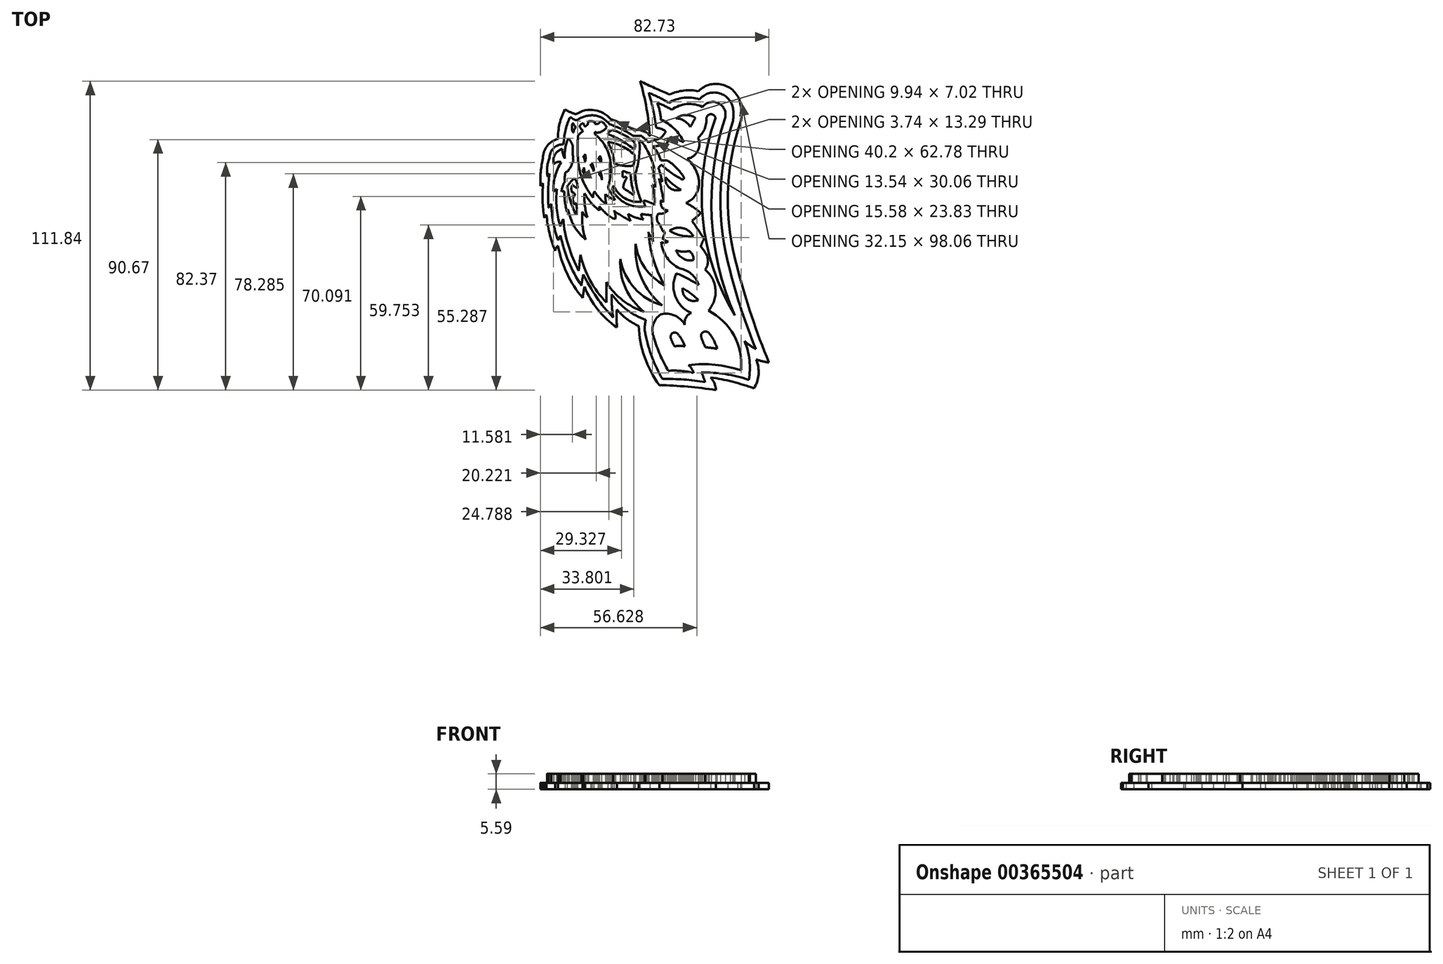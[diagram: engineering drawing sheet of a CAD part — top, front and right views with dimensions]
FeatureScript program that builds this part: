
annotation { "Feature Type Name" : "Feature", "Feature Type Description" : "" }
export const myFeature = defineFeature(function(context is Context, id is Id, definition is map)
    precondition{}
    {
        {
            var Q0;
            Q0=qCreatedBy(makeId("Top.planeOp"),FACE);
            var sketch = newSketch(context, id + "F0", { "sketchPlane" : qUnion([Q0])});
            skLineSegment(sketch, "E0", {"start": v(-9.68, 4.6) * mm, "end": v(-12.98, 4.6) * mm});
            skLineSegment(sketch, "E1", {"start": v(-7.81, 9.13) * mm, "end": v(-5.14, 8.87) * mm});
            skLineSegment(sketch, "E2", {"start": v(-0.46, 12.2) * mm, "end": v(0.77, 11.72) * mm});
            skLineSegment(sketch, "E3", {"start": v(5.28, 13.32) * mm, "end": v(5.62, 12.76) * mm});
            skArc(sketch, "E4", {"start": v(10.1, 12.03) * mm, "mid": v(7.78, 13.04) * mm, "end": v(5.28, 13.32) * mm});
            skArc(sketch, "E5", {"start": v(5.62, 12.76) * mm, "mid": v(2.55, 12.78) * mm, "end": v(-0.46, 12.2) * mm});
            skArc(sketch, "E6", {"start": v(0.77, 11.72) * mm, "mid": v(-3.65, 10.85) * mm, "end": v(-7.81, 9.13) * mm});
            skArc(sketch, "E7", {"start": v(-5.14, 8.87) * mm, "mid": v(-9.36, 7.3) * mm, "end": v(-12.98, 4.6) * mm});
            skArc(sketch, "E8", {"start": v(-9.68, 4.6) * mm, "mid": v(-12.64, 1.92) * mm, "end": v(-14.53, -1.6) * mm});
            skArc(sketch, "E9", {"start": v(-5.85, 2.3) * mm, "mid": v(-10.68, 1.43) * mm, "end": v(-14.53, -1.6) * mm});
            skArc(sketch, "E10", {"start": v(-5.85, 2.3) * mm, "mid": v(-10.66, -0.03) * mm, "end": v(-13.45, -4.58) * mm});
            skArc(sketch, "E11", {"start": v(-3.37, -0.22) * mm, "mid": v(-8.94, -1.17) * mm, "end": v(-13.45, -4.58) * mm});
            skArc(sketch, "E12", {"start": v(-3.37, -0.22) * mm, "mid": v(-7.34, -1.75) * mm, "end": v(-10.14, -4.94) * mm});
            skArc(sketch, "E13", {"start": v(-1.42, -2.32) * mm, "mid": v(-5.93, -3.13) * mm, "end": v(-10.14, -4.94) * mm});
            skArc(sketch, "E14", {"start": v(-1.42, -2.32) * mm, "mid": v(-2.2, -2.67) * mm, "end": v(-2.98, -3.05) * mm});
            skArc(sketch, "E15", {"start": v(-2.98, -3.05) * mm, "mid": v(-0.82, -2.97) * mm, "end": v(1.35, -2.86) * mm});
            skArc(sketch, "E16", {"start": v(1.55, -1.16) * mm, "mid": v(1.44, -2) * mm, "end": v(1.35, -2.86) * mm});
            skArc(sketch, "E17", {"start": v(1.55, -1.16) * mm, "mid": v(1.07, -1.21) * mm, "end": v(0.68, -1.5) * mm});
            skArc(sketch, "E18", {"start": v(1.55, 1.01) * mm, "mid": v(0.98, -0.2) * mm, "end": v(0.68, -1.5) * mm});
            skArc(sketch, "E19", {"start": v(1.55, 1.01) * mm, "mid": v(0.97, 0.86) * mm, "end": v(0.44, 0.6) * mm});
            skArc(sketch, "E20", {"start": v(2.1, 3.35) * mm, "mid": v(1.2, 2.02) * mm, "end": v(0.44, 0.6) * mm});
            skArc(sketch, "E21", {"start": v(0.68, 3.16) * mm, "mid": v(1.4, 3.13) * mm, "end": v(2.1, 3.35) * mm});
            skArc(sketch, "E22", {"start": v(2.8, 5.75) * mm, "mid": v(1.6, 4.58) * mm, "end": v(0.68, 3.16) * mm});
            skArc(sketch, "E23", {"start": v(2.8, 5.75) * mm, "mid": v(2.45, 5.77) * mm, "end": v(2.1, 5.75) * mm});
            skArc(sketch, "E24", {"start": v(4.98, 8.2) * mm, "mid": v(3.41, 7.12) * mm, "end": v(2.1, 5.75) * mm});
            skArc(sketch, "E25", {"start": v(4.98, 8.2) * mm, "mid": v(3, 8.16) * mm, "end": v(1.05, 7.73) * mm});
            skArc(sketch, "E26", {"start": v(1.94, 8.53) * mm, "mid": v(1.4, 8.23) * mm, "end": v(1.05, 7.73) * mm});
            skArc(sketch, "E27", {"start": v(1.94, 8.53) * mm, "mid": v(-0.37, 8.53) * mm, "end": v(-2.64, 8.02) * mm});
            skArc(sketch, "E28", {"start": v(2.29, 10.88) * mm, "mid": v(-0.43, 9.9) * mm, "end": v(-2.64, 8.02) * mm});
            skArc(sketch, "E29", {"start": v(2.29, 10.88) * mm, "mid": v(2.09, 10.98) * mm, "end": v(1.88, 11.07) * mm});
            skArc(sketch, "E30", {"start": v(5.25, 11.51) * mm, "mid": v(3.55, 11.41) * mm, "end": v(1.88, 11.07) * mm});
            skArc(sketch, "E31", {"start": v(5.25, 11.51) * mm, "mid": v(5.3, 11.75) * mm, "end": v(5.25, 11.98) * mm});
            skArc(sketch, "E32", {"start": v(6.95, 11.43) * mm, "mid": v(6.13, 11.8) * mm, "end": v(5.25, 11.98) * mm});
            skArc(sketch, "E33", {"start": v(8.33, 11.35) * mm, "mid": v(7.64, 11.45) * mm, "end": v(6.95, 11.43) * mm});
            skArc(sketch, "E34", {"start": v(8.55, 10.96) * mm, "mid": v(8.5, 11.2) * mm, "end": v(8.33, 11.35) * mm});
            skArc(sketch, "E35", {"start": v(8.55, 10.96) * mm, "mid": v(9.41, 10.45) * mm, "end": v(10.33, 10.05) * mm});
            skArc(sketch, "E36", {"start": v(12.82, 10.15) * mm, "mid": v(11.58, 10.13) * mm, "end": v(10.33, 10.05) * mm});
            skArc(sketch, "E37", {"start": v(12.82, 10.15) * mm, "mid": v(13.46, 10.44) * mm, "end": v(14, 10.88) * mm});
            skArc(sketch, "E38", {"start": v(14, 10.88) * mm, "mid": v(12.37, 11.37) * mm, "end": v(10.67, 11.43) * mm});
            skArc(sketch, "E39", {"start": v(12.27, 11.86) * mm, "mid": v(11.45, 11.74) * mm, "end": v(10.67, 11.43) * mm});
            skArc(sketch, "E40", {"start": v(10.1, 12.03) * mm, "mid": v(10.1, 12.7) * mm, "end": v(9.75, 13.25) * mm});
            skArc(sketch, "E41", {"start": v(12.27, 11.86) * mm, "mid": v(11.3, 13.08) * mm, "end": v(9.75, 13.25) * mm});
            skArc(sketch, "E42", {"start": v(16.51, 10.14) * mm, "mid": v(15.71, 10.28) * mm, "end": v(14.93, 10.05) * mm});
            skArc(sketch, "E43", {"start": v(16.17, 9.93) * mm, "mid": v(16.36, 10) * mm, "end": v(16.51, 10.14) * mm});
            skArc(sketch, "E44", {"start": v(15.52, 9.9) * mm, "mid": v(15.85, 9.7) * mm, "end": v(16.17, 9.93) * mm});
            skArc(sketch, "E45", {"start": v(14.93, 10.05) * mm, "mid": v(15.22, 9.95) * mm, "end": v(15.52, 9.9) * mm});
            skArc(sketch, "E46", {"start": v(6.07, 11.05) * mm, "mid": v(3.67, 10.5) * mm, "end": v(1.42, 9.55) * mm});
            skArc(sketch, "E47", {"start": v(7.46, 9.83) * mm, "mid": v(6.81, 10.5) * mm, "end": v(6.07, 11.05) * mm});
            skArc(sketch, "E48", {"start": v(5.83, 9.35) * mm, "mid": v(6.7, 9.44) * mm, "end": v(7.46, 9.83) * mm});
            skArc(sketch, "E49", {"start": v(6.3, 10.05) * mm, "mid": v(6, 9.74) * mm, "end": v(5.83, 9.35) * mm});
            skArc(sketch, "E50", {"start": v(6.3, 10.05) * mm, "mid": v(6.26, 10.17) * mm, "end": v(6.18, 10.26) * mm});
            skArc(sketch, "E51", {"start": v(6.18, 10.26) * mm, "mid": v(5.66, 10.36) * mm, "end": v(5.14, 10.26) * mm});
            skArc(sketch, "E52", {"start": v(4.58, 9.85) * mm, "mid": v(4.98, 9.89) * mm, "end": v(5.14, 10.26) * mm});
            skArc(sketch, "E53", {"start": v(4.58, 9.85) * mm, "mid": v(4.31, 10.05) * mm, "end": v(3.98, 10.11) * mm});
            skArc(sketch, "E54", {"start": v(3.98, 10.11) * mm, "mid": v(3.54, 10.03) * mm, "end": v(3.14, 9.85) * mm});
            skArc(sketch, "E55", {"start": v(3.35, 9.58) * mm, "mid": v(3.26, 9.72) * mm, "end": v(3.14, 9.85) * mm});
            skArc(sketch, "E56", {"start": v(1.42, 9.55) * mm, "mid": v(2.38, 9.47) * mm, "end": v(3.35, 9.58) * mm});
            skArc(sketch, "E57", {"start": v(10.38, 9.25) * mm, "mid": v(7.14, 8.5) * mm, "end": v(4.28, 6.8) * mm});
            skArc(sketch, "E58", {"start": v(14.46, 9.25) * mm, "mid": v(12.42, 9.35) * mm, "end": v(10.38, 9.25) * mm});
            skArc(sketch, "E59", {"start": v(15.21, 8.4) * mm, "mid": v(14.88, 8.86) * mm, "end": v(14.46, 9.25) * mm});
            skArc(sketch, "E60", {"start": v(16.06, 9.01) * mm, "mid": v(15.59, 8.77) * mm, "end": v(15.21, 8.4) * mm});
            skArc(sketch, "E61", {"start": v(16.54, 8.4) * mm, "mid": v(16.35, 8.74) * mm, "end": v(16.06, 9.01) * mm});
            skArc(sketch, "E62", {"start": v(16.54, 8.4) * mm, "mid": v(16.21, 8.27) * mm, "end": v(15.92, 8.08) * mm});
            skArc(sketch, "E63", {"start": v(16.29, 7.63) * mm, "mid": v(16.12, 7.87) * mm, "end": v(15.92, 8.08) * mm});
            skArc(sketch, "E64", {"start": v(16.8, 7.55) * mm, "mid": v(16.55, 7.62) * mm, "end": v(16.29, 7.63) * mm});
            skArc(sketch, "E65", {"start": v(16.71, 6.51) * mm, "mid": v(16.84, 7.03) * mm, "end": v(16.8, 7.55) * mm});
            skArc(sketch, "E66", {"start": v(16.38, 6.52) * mm, "mid": v(16.55, 6.5) * mm, "end": v(16.71, 6.51) * mm});
            skArc(sketch, "E67", {"start": v(16.38, 6.52) * mm, "mid": v(16.39, 6.2) * mm, "end": v(16.43, 5.9) * mm});
            skArc(sketch, "E68", {"start": v(16.8, 5.4) * mm, "mid": v(16.65, 5.68) * mm, "end": v(16.43, 5.9) * mm});
            skArc(sketch, "E69", {"start": v(15.82, 4.56) * mm, "mid": v(16.37, 4.92) * mm, "end": v(16.8, 5.4) * mm});
            skArc(sketch, "E70", {"start": v(14.95, 6.1) * mm, "mid": v(15.2, 5.23) * mm, "end": v(15.82, 4.56) * mm});
            skArc(sketch, "E71", {"start": v(15.03, 6.33) * mm, "mid": v(14.95, 6.24) * mm, "end": v(14.95, 6.1) * mm});
            skArc(sketch, "E72", {"start": v(15.03, 6.33) * mm, "mid": v(15.02, 6.48) * mm, "end": v(14.88, 6.51) * mm});
            skArc(sketch, "E73", {"start": v(14.88, 6.51) * mm, "mid": v(14.73, 6.48) * mm, "end": v(14.61, 6.38) * mm});
            skArc(sketch, "E74", {"start": v(9.25, 3.89) * mm, "mid": v(12.22, 4.51) * mm, "end": v(14.61, 6.38) * mm});
            skArc(sketch, "E75", {"start": v(5.98, 4.3) * mm, "mid": v(7.6, 3.98) * mm, "end": v(9.25, 3.89) * mm});
            skArc(sketch, "E76", {"start": v(5.98, 4.3) * mm, "mid": v(5.63, 4.2) * mm, "end": v(5.3, 4.04) * mm});
            skArc(sketch, "E77", {"start": v(3.85, 3.19) * mm, "mid": v(4.59, 3.6) * mm, "end": v(5.3, 4.04) * mm});
            skArc(sketch, "E78", {"start": v(4.81, 4.79) * mm, "mid": v(4.27, 4.02) * mm, "end": v(3.85, 3.19) * mm});
            skArc(sketch, "E79", {"start": v(4.81, 4.79) * mm, "mid": v(4, 4.75) * mm, "end": v(3.19, 4.62) * mm});
            skArc(sketch, "E80", {"start": v(5.3, 6.55) * mm, "mid": v(4.13, 5.7) * mm, "end": v(3.19, 4.62) * mm});
            skArc(sketch, "E81", {"start": v(5.3, 6.55) * mm, "mid": v(4.81, 6.76) * mm, "end": v(4.28, 6.8) * mm});
            skArc(sketch, "E82", {"start": v(7.73, 8.16) * mm, "mid": v(8.25, 8.34) * mm, "end": v(8.74, 8.56) * mm});
            skArc(sketch, "E83", {"start": v(8.74, 8.56) * mm, "mid": v(8.94, 8.35) * mm, "end": v(9.23, 8.31) * mm});
            skArc(sketch, "E84", {"start": v(7.73, 8.16) * mm, "mid": v(8.49, 8.18) * mm, "end": v(9.23, 8.31) * mm});
            skArc(sketch, "E85", {"start": v(10.14, 8.12) * mm, "mid": v(10.6, 8.2) * mm, "end": v(11.03, 8.42) * mm});
            skArc(sketch, "E86", {"start": v(11.03, 8.42) * mm, "mid": v(11.18, 8.22) * mm, "end": v(11.42, 8.12) * mm});
            skArc(sketch, "E87", {"start": v(10.14, 8.12) * mm, "mid": v(10.78, 8.02) * mm, "end": v(11.42, 8.12) * mm});
            skArc(sketch, "E88", {"start": v(7.17, 5.33) * mm, "mid": v(7.9, 5.4) * mm, "end": v(8.6, 5.6) * mm});
            skArc(sketch, "E89", {"start": v(8.17, 5.86) * mm, "mid": v(8.38, 5.72) * mm, "end": v(8.6, 5.6) * mm});
            skArc(sketch, "E90", {"start": v(7.17, 5.33) * mm, "mid": v(7.72, 5.51) * mm, "end": v(8.17, 5.86) * mm});
            skArc(sketch, "E91", {"start": v(9.96, 5.53) * mm, "mid": v(10.4, 5.7) * mm, "end": v(10.77, 5.98) * mm});
            skArc(sketch, "E92", {"start": v(10.77, 5.98) * mm, "mid": v(10.9, 5.75) * mm, "end": v(11.15, 5.66) * mm});
            skArc(sketch, "E93", {"start": v(9.96, 5.53) * mm, "mid": v(10.57, 5.48) * mm, "end": v(11.15, 5.66) * mm});
            skArc(sketch, "E94", {"start": v(8.6, 6.68) * mm, "mid": v(9.14, 6.93) * mm, "end": v(9.65, 7.2) * mm});
            skArc(sketch, "E95", {"start": v(9.65, 7.2) * mm, "mid": v(9.74, 7.05) * mm, "end": v(9.88, 6.95) * mm});
            skArc(sketch, "E96", {"start": v(8.6, 6.68) * mm, "mid": v(9.26, 6.73) * mm, "end": v(9.88, 6.95) * mm});
            skArc(sketch, "E97", {"start": v(5.52, 3.63) * mm, "mid": v(3.3, 1.34) * mm, "end": v(2.8, -1.81) * mm});
            skArc(sketch, "E98", {"start": v(3.7, -1.49) * mm, "mid": v(3.25, -1.64) * mm, "end": v(2.8, -1.81) * mm});
            skArc(sketch, "E99", {"start": v(3.64, -2.08) * mm, "mid": v(3.72, -1.79) * mm, "end": v(3.7, -1.49) * mm});
            skArc(sketch, "E100", {"start": v(3.08, -3.32) * mm, "mid": v(3.39, -2.71) * mm, "end": v(3.64, -2.08) * mm});
            skArc(sketch, "E101", {"start": v(3.08, -3.32) * mm, "mid": v(4.74, -3.29) * mm, "end": v(6.35, -2.9) * mm});
            skArc(sketch, "E102", {"start": v(5.9, -3.45) * mm, "mid": v(6.2, -3.23) * mm, "end": v(6.35, -2.9) * mm});
            skArc(sketch, "E103", {"start": v(5.9, -3.45) * mm, "mid": v(7.63, -3.3) * mm, "end": v(9.31, -2.9) * mm});
            skArc(sketch, "E104", {"start": v(9.1, -3.27) * mm, "mid": v(9.24, -3.1) * mm, "end": v(9.31, -2.9) * mm});
            skArc(sketch, "E105", {"start": v(9.1, -3.27) * mm, "mid": v(11.43, -2.43) * mm, "end": v(13.54, -1.16) * mm});
            skArc(sketch, "E106", {"start": v(13.54, -1.16) * mm, "mid": v(13.58, -1) * mm, "end": v(13.54, -0.84) * mm});
            skArc(sketch, "E107", {"start": v(8.15, -0.14) * mm, "mid": v(10.81, -0.75) * mm, "end": v(13.54, -0.84) * mm});
            skArc(sketch, "E108", {"start": v(8.15, -0.14) * mm, "mid": v(5.82, -0.44) * mm, "end": v(3.58, -1.16) * mm});
            skArc(sketch, "E109", {"start": v(6.23, 3.41) * mm, "mid": v(4.15, 1.56) * mm, "end": v(3.58, -1.16) * mm});
            skArc(sketch, "E110", {"start": v(6.23, 3.41) * mm, "mid": v(5.89, 3.57) * mm, "end": v(5.52, 3.63) * mm});
            skArc(sketch, "E111", {"start": v(4.7, 0.16) * mm, "mid": v(5.28, 0.98) * mm, "end": v(5.8, 1.83) * mm});
            skArc(sketch, "E112", {"start": v(4.93, 0) * mm, "mid": v(4.86, 0.15) * mm, "end": v(4.7, 0.16) * mm});
            skArc(sketch, "E113", {"start": v(8.24, 0.59) * mm, "mid": v(6.56, 0.46) * mm, "end": v(4.93, 0) * mm});
            skArc(sketch, "E114", {"start": v(8.6, 1.67) * mm, "mid": v(8.37, 1.15) * mm, "end": v(8.24, 0.59) * mm});
            skArc(sketch, "E115", {"start": v(8.6, 1.67) * mm, "mid": v(8.6, 1.81) * mm, "end": v(8.55, 1.94) * mm});
            skArc(sketch, "E116", {"start": v(8.55, 1.94) * mm, "mid": v(8.1, 1.96) * mm, "end": v(7.66, 1.92) * mm});
            skArc(sketch, "E117", {"start": v(7.66, 1.92) * mm, "mid": v(7.63, 1.7) * mm, "end": v(7.7, 1.47) * mm});
            skArc(sketch, "E118", {"start": v(7.33, 1.33) * mm, "mid": v(7.55, 1.31) * mm, "end": v(7.7, 1.47) * mm});
            skArc(sketch, "E119", {"start": v(7.33, 1.33) * mm, "mid": v(6.6, 1.7) * mm, "end": v(5.8, 1.83) * mm});
            skArc(sketch, "E120", {"start": v(9.88, 3.3) * mm, "mid": v(11.73, 3.65) * mm, "end": v(13.45, 4.39) * mm});
            skArc(sketch, "E121", {"start": v(11.33, 0) * mm, "mid": v(12.7, 2.04) * mm, "end": v(13.45, 4.39) * mm});
            skArc(sketch, "E122", {"start": v(9.52, 0.16) * mm, "mid": v(10.42, -0.02) * mm, "end": v(11.33, 0) * mm});
            skArc(sketch, "E123", {"start": v(9.88, 3.3) * mm, "mid": v(9.5, 1.76) * mm, "end": v(9.52, 0.16) * mm});
            skArc(sketch, "E124", {"start": v(12.2, 0) * mm, "mid": v(13.62, 2.1) * mm, "end": v(14.72, 4.39) * mm});
            skArc(sketch, "E125", {"start": v(15.39, 3.63) * mm, "mid": v(15.11, 4.06) * mm, "end": v(14.72, 4.39) * mm});
            skArc(sketch, "E126", {"start": v(13.45, 0.07) * mm, "mid": v(14.61, 1.75) * mm, "end": v(15.39, 3.63) * mm});
            skArc(sketch, "E127", {"start": v(12.2, 0) * mm, "mid": v(12.83, -0.13) * mm, "end": v(13.45, 0.07) * mm});
            skArc(sketch, "E128", {"start": v(13.02, 11.85) * mm, "mid": v(12.36, 13.32) * mm, "end": v(10.87, 13.95) * mm});
            skArc(sketch, "E129", {"start": v(10.87, 13.95) * mm, "mid": v(9.33, 14.32) * mm, "end": v(7.74, 14.28) * mm});
            skArc(sketch, "E130", {"start": v(8.16, 13.95) * mm, "mid": v(7.98, 14.16) * mm, "end": v(7.74, 14.28) * mm});
            skArc(sketch, "E131", {"start": v(8.16, 13.95) * mm, "mid": v(5.37, 14.2) * mm, "end": v(2.56, 14.1) * mm});
            skArc(sketch, "E132", {"start": v(3.2, 13.67) * mm, "mid": v(2.91, 13.93) * mm, "end": v(2.56, 14.1) * mm});
            skArc(sketch, "E133", {"start": v(3.2, 13.67) * mm, "mid": v(0.16, 13.34) * mm, "end": v(-2.78, 12.53) * mm});
            skArc(sketch, "E134", {"start": v(-1.98, 12.13) * mm, "mid": v(-2.37, 12.36) * mm, "end": v(-2.78, 12.53) * mm});
            skArc(sketch, "E135", {"start": v(-1.98, 12.13) * mm, "mid": v(-6.26, 10.84) * mm, "end": v(-10.2, 8.72) * mm});
            skArc(sketch, "E136", {"start": v(-8.38, 8.4) * mm, "mid": v(-9.3, 8.57) * mm, "end": v(-10.2, 8.72) * mm});
            skArc(sketch, "E137", {"start": v(-8.38, 8.4) * mm, "mid": v(-12.13, 6.22) * mm, "end": v(-15.5, 3.49) * mm});
            skArc(sketch, "E138", {"start": v(-11.68, 3.7) * mm, "mid": v(-13.6, 3.7) * mm, "end": v(-15.5, 3.49) * mm});
            skArc(sketch, "E139", {"start": v(-11.68, 3.7) * mm, "mid": v(-14.21, 1.23) * mm, "end": v(-15.86, -1.9) * mm});
            skArc(sketch, "E140", {"start": v(-24.58, -9.74) * mm, "mid": v(-24.27, -7.67) * mm, "end": v(-24.25, -5.57) * mm});
            skArc(sketch, "E141", {"start": v(-24.58, -9.74) * mm, "mid": v(-23.88, -9.42) * mm, "end": v(-23.3, -8.93) * mm});
            skArc(sketch, "E142", {"start": v(-24.17, -17.55) * mm, "mid": v(-23.26, -13.28) * mm, "end": v(-23.3, -8.93) * mm});
            skArc(sketch, "E143", {"start": v(-24.17, -17.55) * mm, "mid": v(-18.43, -16.4) * mm, "end": v(-14.35, -12.2) * mm});
            skArc(sketch, "E144", {"start": v(-14.35, -12.2) * mm, "mid": v(-10.86, -13.35) * mm, "end": v(-7.61, -11.64) * mm});
            skArc(sketch, "E145", {"start": v(-7.61, -11.64) * mm, "mid": v(-6.2, -12.12) * mm, "end": v(-4.78, -11.64) * mm});
            skArc(sketch, "E146", {"start": v(-4.78, -11.64) * mm, "mid": v(-4.29, -11.32) * mm, "end": v(-3.85, -10.94) * mm});
            skArc(sketch, "E147", {"start": v(-2.55, -11.5) * mm, "mid": v(-3.17, -11.15) * mm, "end": v(-3.85, -10.94) * mm});
            skArc(sketch, "E148", {"start": v(-2.55, -11.5) * mm, "mid": v(-1.05, -10.5) * mm, "end": v(0.45, -9.5) * mm});
            skArc(sketch, "E149", {"start": v(0.45, -9.5) * mm, "mid": v(1.07, -10.24) * mm, "end": v(1.74, -10.94) * mm});
            skArc(sketch, "E150", {"start": v(1.74, -10.94) * mm, "mid": v(2.64, -9.77) * mm, "end": v(3.37, -8.49) * mm});
            skArc(sketch, "E151", {"start": v(3.37, -8.49) * mm, "mid": v(4.6, -10) * mm, "end": v(6.43, -10.67) * mm});
            skArc(sketch, "E152", {"start": v(6.43, -10.67) * mm, "mid": v(8.75, -10.13) * mm, "end": v(10.65, -8.7) * mm});
            skArc(sketch, "E153", {"start": v(10.65, -8.7) * mm, "mid": v(11.92, -10.44) * mm, "end": v(14.08, -10.47) * mm});
            skArc(sketch, "E154", {"start": v(14.08, -10.47) * mm, "mid": v(15.54, -11.55) * mm, "end": v(17.34, -11.86) * mm});
            skArc(sketch, "E155", {"start": v(17.34, -13.36) * mm, "mid": v(17.98, -12.6) * mm, "end": v(17.34, -11.86) * mm});
            skArc(sketch, "E156", {"start": v(17.34, -13.36) * mm, "mid": v(0.74, -11.26) * mm, "end": v(-15.14, -16.54) * mm});
            skArc(sketch, "E157", {"start": v(17.28, -14.9) * mm, "mid": v(0.92, -12.72) * mm, "end": v(-15.14, -16.54) * mm});
            skArc(sketch, "E158", {"start": v(17.28, -14.9) * mm, "mid": v(19.78, -13.86) * mm, "end": v(19.16, -11.23) * mm});
            skArc(sketch, "E159", {"start": v(19.16, -11.23) * mm, "mid": v(19.65, -8.63) * mm, "end": v(18.7, -6.17) * mm});
            skArc(sketch, "E160", {"start": v(17.07, -4.37) * mm, "mid": v(17.1, -4.36) * mm, "end": v(17.13, -4.36) * mm});
            skArc(sketch, "E161", {"start": v(13.39, -8.11) * mm, "mid": v(15.58, -6.59) * mm, "end": v(17.07, -4.37) * mm});
            skArc(sketch, "E162", {"start": v(13.39, -8.11) * mm, "mid": v(13.82, -7.08) * mm, "end": v(14.23, -6.03) * mm});
            skArc(sketch, "E163", {"start": v(14.23, -6.03) * mm, "mid": v(13.74, -5.6) * mm, "end": v(13.13, -5.37) * mm});
            skArc(sketch, "E164", {"start": v(12.66, -3.05) * mm, "mid": v(12.84, -4.22) * mm, "end": v(13.13, -5.37) * mm});
            skArc(sketch, "E165", {"start": v(10.39, -4.36) * mm, "mid": v(11.6, -3.85) * mm, "end": v(12.66, -3.05) * mm});
            skArc(sketch, "E166", {"start": v(10.39, -4.36) * mm, "mid": v(10.36, -4.86) * mm, "end": v(10.39, -5.37) * mm});
            skArc(sketch, "E167", {"start": v(7.66, -8.11) * mm, "mid": v(9.19, -6.9) * mm, "end": v(10.39, -5.37) * mm});
            skArc(sketch, "E168", {"start": v(7.37, -7.66) * mm, "mid": v(7.28, -8.04) * mm, "end": v(7.66, -8.11) * mm});
            skArc(sketch, "E169", {"start": v(9.64, -4.5) * mm, "mid": v(8.39, -6) * mm, "end": v(7.37, -7.66) * mm});
            skArc(sketch, "E170", {"start": v(9.64, -4.5) * mm, "mid": v(9.43, -4.21) * mm, "end": v(9.16, -3.97) * mm});
            skArc(sketch, "E171", {"start": v(6.85, -4.6) * mm, "mid": v(8.01, -4.32) * mm, "end": v(9.16, -3.97) * mm});
            skArc(sketch, "E172", {"start": v(7.37, -4.05) * mm, "mid": v(7.07, -4.3) * mm, "end": v(6.85, -4.6) * mm});
            skArc(sketch, "E173", {"start": v(3.6, -4.84) * mm, "mid": v(5.5, -4.48) * mm, "end": v(7.37, -4.05) * mm});
            skArc(sketch, "E174", {"start": v(3.82, -4.37) * mm, "mid": v(3.66, -4.58) * mm, "end": v(3.6, -4.84) * mm});
            skArc(sketch, "E175", {"start": v(3.82, -4.37) * mm, "mid": v(3.27, -4.36) * mm, "end": v(2.73, -4.5) * mm});
            skArc(sketch, "E176", {"start": v(2.73, -4.5) * mm, "mid": v(2.32, -4.94) * mm, "end": v(2.15, -5.5) * mm});
            skArc(sketch, "E177", {"start": v(1.65, -3.97) * mm, "mid": v(1.68, -4.8) * mm, "end": v(2.15, -5.5) * mm});
            skArc(sketch, "E178", {"start": v(1.65, -3.97) * mm, "mid": v(0.81, -3.7) * mm, "end": v(0, -4.05) * mm});
            skArc(sketch, "E179", {"start": v(-1.39, -4.73) * mm, "mid": v(-0.68, -4.41) * mm, "end": v(0, -4.05) * mm});
            skArc(sketch, "E180", {"start": v(-1.39, -5.02) * mm, "mid": v(-1.36, -4.87) * mm, "end": v(-1.39, -4.73) * mm});
            skArc(sketch, "E181", {"start": v(-2.42, -4.6) * mm, "mid": v(-1.93, -4.87) * mm, "end": v(-1.39, -5.02) * mm});
            skArc(sketch, "E182", {"start": v(-2.42, -4.6) * mm, "mid": v(-2.77, -5.05) * mm, "end": v(-3, -5.56) * mm});
            skArc(sketch, "E183", {"start": v(-3.1, -4.43) * mm, "mid": v(-3.16, -5) * mm, "end": v(-3, -5.56) * mm});
            skArc(sketch, "E184", {"start": v(-3.1, -4.43) * mm, "mid": v(-5.64, -5.37) * mm, "end": v(-7.38, -7.45) * mm});
            skArc(sketch, "E185", {"start": v(-10.1, -10.6) * mm, "mid": v(-8.33, -9.38) * mm, "end": v(-7.38, -7.45) * mm});
            skArc(sketch, "E186", {"start": v(-10.1, -10.6) * mm, "mid": v(-9.1, -8.79) * mm, "end": v(-8.2, -6.91) * mm});
            skArc(sketch, "E187", {"start": v(-8.2, -6.91) * mm, "mid": v(-11.98, -6.74) * mm, "end": v(-14.72, -9.36) * mm});
            skArc(sketch, "E188", {"start": v(-14.72, -9.36) * mm, "mid": v(-15.51, -8.48) * mm, "end": v(-16.68, -8.3) * mm});
            skArc(sketch, "E189", {"start": v(-16.68, -8.3) * mm, "mid": v(-15.15, -6.62) * mm, "end": v(-14.95, -4.36) * mm});
            skArc(sketch, "E190", {"start": v(-14.95, -4.36) * mm, "mid": v(-16.66, -3.1) * mm, "end": v(-18.77, -3.22) * mm});
            skArc(sketch, "E191", {"start": v(-18.77, -3.22) * mm, "mid": v(-21.58, -4.23) * mm, "end": v(-24.25, -5.57) * mm});
            skArc(sketch, "E192", {"start": v(-18.29, -7.24) * mm, "mid": v(-18.03, -6.33) * mm, "end": v(-18.92, -6.02) * mm});
            skArc(sketch, "E193", {"start": v(-18.1, -12.31) * mm, "mid": v(-17.86, -11.37) * mm, "end": v(-18.78, -11.03) * mm});
            skArc(sketch, "E194", {"start": v(-18.78, -11.03) * mm, "mid": v(-19.6, -11.32) * mm, "end": v(-20.38, -11.68) * mm});
            skArc(sketch, "E195", {"start": v(-20.64, -13.62) * mm, "mid": v(-20.48, -12.65) * mm, "end": v(-20.38, -11.68) * mm});
            skArc(sketch, "E196", {"start": v(-20.64, -13.62) * mm, "mid": v(-19.3, -13.1) * mm, "end": v(-18.1, -12.31) * mm});
            skArc(sketch, "E197", {"start": v(-20.22, -8.34) * mm, "mid": v(-19.21, -7.87) * mm, "end": v(-18.29, -7.24) * mm});
            skArc(sketch, "E198", {"start": v(-20.22, -8.34) * mm, "mid": v(-20.16, -7.47) * mm, "end": v(-20.22, -6.61) * mm});
            skArc(sketch, "E199", {"start": v(-18.92, -6.02) * mm, "mid": v(-19.6, -6.27) * mm, "end": v(-20.22, -6.61) * mm});
            skArc(sketch, "E200", {"start": v(-10.64, -7.94) * mm, "mid": v(-12.38, -8.67) * mm, "end": v(-12.6, -10.54) * mm});
            skArc(sketch, "E201", {"start": v(-12.6, -10.54) * mm, "mid": v(-11.54, -9.3) * mm, "end": v(-10.64, -7.94) * mm});
            skArc(sketch, "E202", {"start": v(-4.4, -6.86) * mm, "mid": v(-5.75, -7.98) * mm, "end": v(-6.04, -9.7) * mm});
            skArc(sketch, "E203", {"start": v(-4.4, -6.86) * mm, "mid": v(-4.64, -7.92) * mm, "end": v(-4.52, -9) * mm});
            skArc(sketch, "E204", {"start": v(-6.04, -9.7) * mm, "mid": v(-5.17, -9.59) * mm, "end": v(-4.52, -9) * mm});
            skArc(sketch, "E205", {"start": v(-1.19, -5.8) * mm, "mid": v(-1.97, -7.67) * mm, "end": v(-2.08, -9.7) * mm});
            skArc(sketch, "E206", {"start": v(-2.08, -9.7) * mm, "mid": v(-0.77, -7.95) * mm, "end": v(-1.19, -5.8) * mm});
            skArc(sketch, "E207", {"start": v(7.61, -5.11) * mm, "mid": v(5.87, -5.82) * mm, "end": v(5.56, -7.68) * mm});
            skArc(sketch, "E208", {"start": v(7.61, -5.11) * mm, "mid": v(6.48, -6.3) * mm, "end": v(5.56, -7.68) * mm});
            skArc(sketch, "E209", {"start": v(15.87, -9.22) * mm, "mid": v(16.89, -8.22) * mm, "end": v(17.3, -6.86) * mm});
            skArc(sketch, "E210", {"start": v(17.4, -10.1) * mm, "mid": v(16.65, -9.63) * mm, "end": v(15.87, -9.22) * mm});
            skArc(sketch, "E211", {"start": v(17.4, -10.1) * mm, "mid": v(17.84, -8.46) * mm, "end": v(17.3, -6.86) * mm});
            skArc(sketch, "E212", {"start": v(17.07, -4.37) * mm, "mid": v(18.49, -4.19) * mm, "end": v(19.85, -3.77) * mm});
            skArc(sketch, "E213", {"start": v(18.7, -6.17) * mm, "mid": v(19.35, -5) * mm, "end": v(19.85, -3.77) * mm});
            skArc(sketch, "E214", {"start": v(13.02, 11.85) * mm, "mid": v(13.04, 11.74) * mm, "end": v(13.06, 11.63) * mm});
            skArc(sketch, "E215", {"start": v(17.29, 10.7) * mm, "mid": v(15.22, 11.35) * mm, "end": v(13.06, 11.63) * mm});
            skArc(sketch, "E216", {"start": v(17.33, 10.26) * mm, "mid": v(17.44, 10.49) * mm, "end": v(17.29, 10.7) * mm});
            skArc(sketch, "E217", {"start": v(17.33, 10.26) * mm, "mid": v(17.12, 9.92) * mm, "end": v(17, 9.53) * mm});
            skArc(sketch, "E218", {"start": v(17, 9.53) * mm, "mid": v(17.04, 9.33) * mm, "end": v(17.18, 9.17) * mm});
            skArc(sketch, "E219", {"start": v(17.77, 6.48) * mm, "mid": v(17.7, 7.88) * mm, "end": v(17.18, 9.17) * mm});
            skArc(sketch, "E220", {"start": v(16.33, 4.1) * mm, "mid": v(17.29, 5.15) * mm, "end": v(17.77, 6.48) * mm});
            skArc(sketch, "E221", {"start": v(14.4, 0.14) * mm, "mid": v(15.5, 2.06) * mm, "end": v(16.33, 4.1) * mm});
            skArc(sketch, "E222", {"start": v(14.4, -1.22) * mm, "mid": v(14.4, -0.54) * mm, "end": v(14.4, 0.14) * mm});
            skArc(sketch, "E223", {"start": v(14.4, -1.22) * mm, "mid": v(13.9, -1.76) * mm, "end": v(13.4, -2.31) * mm});
            skArc(sketch, "E224", {"start": v(13.4, -2.31) * mm, "mid": v(13.71, -3.32) * mm, "end": v(14.03, -4.34) * mm});
            skArc(sketch, "E225", {"start": v(14.03, -4.34) * mm, "mid": v(14.47, -4.72) * mm, "end": v(14.93, -5.07) * mm});
            skArc(sketch, "E226", {"start": v(14.93, -5.07) * mm, "mid": v(15.07, -5.1) * mm, "end": v(15.2, -5.07) * mm});
            skArc(sketch, "E227", {"start": v(15.2, -5.07) * mm, "mid": v(15.59, -4.37) * mm, "end": v(15.75, -3.6) * mm});
            skArc(sketch, "E228", {"start": v(15.75, -3.6) * mm, "mid": v(18.66, -3.11) * mm, "end": v(21.51, -2.36) * mm});
            skArc(sketch, "E229", {"start": v(19.87, -5.7) * mm, "mid": v(20.74, -4.05) * mm, "end": v(21.51, -2.36) * mm});
            skArc(sketch, "E230", {"start": v(20.45, -10.71) * mm, "mid": v(20.7, -8.14) * mm, "end": v(19.87, -5.7) * mm});
            skArc(sketch, "E231", {"start": v(19.16, -16.2) * mm, "mid": v(21.47, -13.85) * mm, "end": v(20.45, -10.71) * mm});
            skArc(sketch, "E232", {"start": v(16.74, -16.2) * mm, "mid": v(17.95, -16.3) * mm, "end": v(19.16, -16.2) * mm});
            skArc(sketch, "E233", {"start": v(16.74, -16.2) * mm, "mid": v(4.47, -14.17) * mm, "end": v(-7.86, -15.76) * mm});
            skArc(sketch, "E234", {"start": v(-7.86, -15.76) * mm, "mid": v(-14.34, -17.65) * mm, "end": v(-20.67, -19.99) * mm});
            skArc(sketch, "E235", {"start": v(-19.37, -18.13) * mm, "mid": v(-20.07, -19.03) * mm, "end": v(-20.67, -19.99) * mm});
            skArc(sketch, "E236", {"start": v(-25.73, -18.82) * mm, "mid": v(-22.5, -18.95) * mm, "end": v(-19.37, -18.13) * mm});
            skArc(sketch, "E237", {"start": v(-25.73, -18.82) * mm, "mid": v(-24.8, -14.96) * mm, "end": v(-24.52, -11) * mm});
            skArc(sketch, "E238", {"start": v(-26.1, -11.63) * mm, "mid": v(-25.29, -11.37) * mm, "end": v(-24.52, -11) * mm});
            skArc(sketch, "E239", {"start": v(-26.1, -11.63) * mm, "mid": v(-25.7, -8.14) * mm, "end": v(-25.59, -4.62) * mm});
            skArc(sketch, "E240", {"start": v(-18.2, -1.81) * mm, "mid": v(-22.01, -2.9) * mm, "end": v(-25.59, -4.62) * mm});
            skArc(sketch, "E241", {"start": v(-15.86, -1.9) * mm, "mid": v(-17.03, -1.71) * mm, "end": v(-18.2, -1.81) * mm});
            skArc(sketch, "E242", {"start": v(-14.16, 2.89) * mm, "mid": v(-15.64, 2.9) * mm, "end": v(-17.12, 2.87) * mm});
            skArc(sketch, "E243", {"start": v(-14.16, 2.89) * mm, "mid": v(-15.72, 1.25) * mm, "end": v(-16.86, -0.7) * mm});
            skArc(sketch, "E244", {"start": v(-16.86, -0.7) * mm, "mid": v(-21.99, -1.68) * mm, "end": v(-26.62, -4.1) * mm});
            skArc(sketch, "E245", {"start": v(-27.42, -13.43) * mm, "mid": v(-26.86, -8.78) * mm, "end": v(-26.62, -4.1) * mm});
            skArc(sketch, "E246", {"start": v(-27.42, -13.43) * mm, "mid": v(-26.3, -13.17) * mm, "end": v(-25.33, -12.54) * mm});
            skArc(sketch, "E247", {"start": v(-27.15, -19.7) * mm, "mid": v(-26.06, -16.17) * mm, "end": v(-25.33, -12.54) * mm});
            skArc(sketch, "E248", {"start": v(-27.15, -19.7) * mm, "mid": v(-24.8, -20.43) * mm, "end": v(-22.39, -20.03) * mm});
            skArc(sketch, "E249", {"start": v(-22.39, -20.03) * mm, "mid": v(-22.68, -21.08) * mm, "end": v(-22.9, -22.15) * mm});
            skArc(sketch, "E250", {"start": v(-7.43, -16.97) * mm, "mid": v(-15.25, -19.3) * mm, "end": v(-22.9, -22.15) * mm});
            skArc(sketch, "E251", {"start": v(16.66, -17.48) * mm, "mid": v(4.66, -15.37) * mm, "end": v(-7.43, -16.97) * mm});
            skArc(sketch, "E252", {"start": v(16.66, -17.48) * mm, "mid": v(18.1, -17.64) * mm, "end": v(19.54, -17.48) * mm});
            skArc(sketch, "E253", {"start": v(19.54, -17.48) * mm, "mid": v(22.8, -14.7) * mm, "end": v(21.78, -10.54) * mm});
            skArc(sketch, "E254", {"start": v(21.78, -10.54) * mm, "mid": v(21.87, -8.13) * mm, "end": v(21.25, -5.8) * mm});
            skArc(sketch, "E255", {"start": v(23.41, -0.97) * mm, "mid": v(22.29, -3.37) * mm, "end": v(21.25, -5.8) * mm});
            skArc(sketch, "E256", {"start": v(14.39, -2.56) * mm, "mid": v(18.94, -2) * mm, "end": v(23.41, -0.97) * mm});
            skArc(sketch, "E257", {"start": v(14.39, -2.56) * mm, "mid": v(15.26, -1.42) * mm, "end": v(15.33, 0) * mm});
            skArc(sketch, "E258", {"start": v(15.33, 0) * mm, "mid": v(16.38, 1.86) * mm, "end": v(17.15, 3.85) * mm});
            skArc(sketch, "E259", {"start": v(17.15, 3.85) * mm, "mid": v(18.66, 6.56) * mm, "end": v(17.98, 9.6) * mm});
            skArc(sketch, "E260", {"start": v(18.75, 11.41) * mm, "mid": v(18.32, 10.52) * mm, "end": v(17.98, 9.6) * mm});
            skArc(sketch, "E261", {"start": v(18.75, 11.41) * mm, "mid": v(16.4, 12.3) * mm, "end": v(13.9, 12.55) * mm});
            skArc(sketch, "E262", {"start": v(13.9, 12.55) * mm, "mid": v(12.76, 14.35) * mm, "end": v(10.74, 15.02) * mm});
            skArc(sketch, "E263", {"start": v(10.74, 15.02) * mm, "mid": v(8.46, 15.4) * mm, "end": v(6.14, 15.43) * mm});
            skArc(sketch, "E264", {"start": v(6.63, 15.02) * mm, "mid": v(6.43, 15.28) * mm, "end": v(6.14, 15.43) * mm});
            skArc(sketch, "E265", {"start": v(6.63, 15.02) * mm, "mid": v(3.78, 15.1) * mm, "end": v(0.94, 14.81) * mm});
            skArc(sketch, "E266", {"start": v(1.45, 14.45) * mm, "mid": v(1.22, 14.68) * mm, "end": v(0.94, 14.81) * mm});
            skArc(sketch, "E267", {"start": v(1.45, 14.45) * mm, "mid": v(-1.6, 13.97) * mm, "end": v(-4.52, 13) * mm});
            skArc(sketch, "E268", {"start": v(-3.7, 12.55) * mm, "mid": v(-4.05, 12.89) * mm, "end": v(-4.52, 13) * mm});
            skArc(sketch, "E269", {"start": v(-3.7, 12.55) * mm, "mid": v(-8.24, 11.07) * mm, "end": v(-12.25, 8.5) * mm});
            skArc(sketch, "E270", {"start": v(-10.42, 8.18) * mm, "mid": v(-11.33, 8.37) * mm, "end": v(-12.25, 8.5) * mm});
            skArc(sketch, "E271", {"start": v(-10.42, 8.18) * mm, "mid": v(-14.16, 6.02) * mm, "end": v(-17.12, 2.87) * mm});
            skLineSegment(sketch, "E272", {"start": v(-4.94, 16.73) * mm, "end": v(-17.06, 19.36) * mm});
            skSolve(sketch);
        }
        {
            var Q0;
            Q0=makeQuery(id+"F0.imprint","IMPRINT",FACE,{"disambiguationData":[TD([[makeQuery(id+"F0.imprint","IMPRINT",EDGE,{"derivedFrom":sQuery(id+"F0.wireOp",EDGE,"E128")}),-1.0]])]});
            var Q1;
            Q1=makeQuery(id+"F0.imprint","IMPRINT",FACE,{"disambiguationData":[TD([[makeQuery(id+"F0.imprint","IMPRINT",EDGE,{"derivedFrom":sQuery(id+"F0.wireOp",EDGE,"E193")}),1.0]])]});
            var Q2;
            Q2=makeQuery(id+"F0.imprint","IMPRINT",FACE,{"disambiguationData":[TD([[makeQuery(id+"F0.imprint","IMPRINT",EDGE,{"derivedFrom":sQuery(id+"F0.wireOp",EDGE,"E192")}),1.0]])]});
            var Q3;
            Q3=makeQuery(id+"F0.imprint","IMPRINT",FACE,{"disambiguationData":[TD([[makeQuery(id+"F0.imprint","IMPRINT",EDGE,{"derivedFrom":sQuery(id+"F0.wireOp",EDGE,"E200")}),1.0]])]});
            var Q4;
            Q4=makeQuery(id+"F0.imprint","IMPRINT",FACE,{"disambiguationData":[TD([[makeQuery(id+"F0.imprint","IMPRINT",EDGE,{"derivedFrom":sQuery(id+"F0.wireOp",EDGE,"E202")}),1.0]])]});
            var Q5;
            Q5=makeQuery(id+"F0.imprint","IMPRINT",FACE,{"disambiguationData":[TD([[makeQuery(id+"F0.imprint","IMPRINT",EDGE,{"derivedFrom":sQuery(id+"F0.wireOp",EDGE,"E205")}),1.0]])]});
            var Q6;
            Q6=makeQuery(id+"F0.imprint","IMPRINT",FACE,{"disambiguationData":[TD([[makeQuery(id+"F0.imprint","IMPRINT",EDGE,{"derivedFrom":sQuery(id+"F0.wireOp",EDGE,"E209")}),-1.0]])]});
            var Q7;
            Q7=makeQuery(id+"F0.imprint","IMPRINT",FACE,{"disambiguationData":[TD([[makeQuery(id+"F0.imprint","IMPRINT",EDGE,{"derivedFrom":sQuery(id+"F0.wireOp",EDGE,"E111")}),-1.0]])]});
            var Q8;
            Q8=makeQuery(id+"F0.imprint","IMPRINT",FACE,{"disambiguationData":[TD([[makeQuery(id+"F0.imprint","IMPRINT",EDGE,{"derivedFrom":sQuery(id+"F0.wireOp",EDGE,"E0")}),1.0]])]});
            var Q9;
            Q9=makeQuery(id+"F0.imprint","IMPRINT",FACE,{"disambiguationData":[TD([[makeQuery(id+"F0.imprint","IMPRINT",EDGE,{"derivedFrom":sQuery(id+"F0.wireOp",EDGE,"E94")}),-1.0]])]});
            var Q10;
            Q10=makeQuery(id+"F0.imprint","IMPRINT",FACE,{"disambiguationData":[TD([[makeQuery(id+"F0.imprint","IMPRINT",EDGE,{"derivedFrom":sQuery(id+"F0.wireOp",EDGE,"E85")}),-1.0]])]});
            var Q11;
            Q11=makeQuery(id+"F0.imprint","IMPRINT",FACE,{"disambiguationData":[TD([[makeQuery(id+"F0.imprint","IMPRINT",EDGE,{"derivedFrom":sQuery(id+"F0.wireOp",EDGE,"E42")}),1.0]])]});
            var Q12;
            Q12=makeQuery(id+"F0.imprint","IMPRINT",FACE,{"disambiguationData":[TD([[makeQuery(id+"F0.imprint","IMPRINT",EDGE,{"derivedFrom":sQuery(id+"F0.wireOp",EDGE,"E0")}),-1.0]])]});
            var Q13;
            Q13=makeQuery(id+"F0.imprint","IMPRINT",FACE,{"disambiguationData":[TD([[makeQuery(id+"F0.imprint","IMPRINT",EDGE,{"derivedFrom":sQuery(id+"F0.wireOp",EDGE,"E140")}),-1.0]])]});
            var Q14;
            Q14=makeQuery(id+"F0.imprint","IMPRINT",FACE,{"disambiguationData":[TD([[makeQuery(id+"F0.imprint","IMPRINT",EDGE,{"derivedFrom":sQuery(id+"F0.wireOp",EDGE,"E97")}),1.0]])]});
            var Q15;
            Q15=makeQuery(id+"F0.imprint","IMPRINT",FACE,{"disambiguationData":[TD([[makeQuery(id+"F0.imprint","IMPRINT",EDGE,{"derivedFrom":sQuery(id+"F0.wireOp",EDGE,"E57")}),1.0]])]});
            var Q16;
            Q16=makeQuery(id+"F0.imprint","IMPRINT",FACE,{"disambiguationData":[TD([[makeQuery(id+"F0.imprint","IMPRINT",EDGE,{"derivedFrom":sQuery(id+"F0.wireOp",EDGE,"E207")}),1.0]])]});
            var Q17;
            Q17=makeQuery(id+"F0.imprint","IMPRINT",FACE,{"disambiguationData":[TD([[makeQuery(id+"F0.imprint","IMPRINT",EDGE,{"derivedFrom":sQuery(id+"F0.wireOp",EDGE,"E91")}),-1.0]])]});
            var Q18;
            Q18=makeQuery(id+"F0.imprint","IMPRINT",FACE,{"disambiguationData":[TD([[makeQuery(id+"F0.imprint","IMPRINT",EDGE,{"derivedFrom":sQuery(id+"F0.wireOp",EDGE,"E88")}),1.0]])]});
            var Q19;
            Q19=makeQuery(id+"F0.imprint","IMPRINT",FACE,{"disambiguationData":[TD([[makeQuery(id+"F0.imprint","IMPRINT",EDGE,{"derivedFrom":sQuery(id+"F0.wireOp",EDGE,"E82")}),-1.0]])]});
            extrude(context, id + "F1", {"entities" : qUnion([Q0, Q1, Q2, Q3, Q4, Q5, Q6, Q7, Q8, Q9, Q10, Q11, Q12, Q13, Q14, Q15, Q16, Q17, Q18, Q19]), "depth" : 1.02 * mm});
        }
        {
            var Q0;
            Q0=makeQuery(id+"F0.imprint","IMPRINT",FACE,{"disambiguationData":[TD([[makeQuery(id+"F0.imprint","IMPRINT",EDGE,{"derivedFrom":sQuery(id+"F0.wireOp",EDGE,"E128")}),-1.0]])]});
            var Q1;
            Q1=makeQuery(id+"F0.imprint","IMPRINT",FACE,{"disambiguationData":[TD([[makeQuery(id+"F0.imprint","IMPRINT",EDGE,{"derivedFrom":sQuery(id+"F0.wireOp",EDGE,"E0")}),-1.0]])]});
            var Q2;
            Q2=makeQuery(id+"F0.imprint","IMPRINT",FACE,{"disambiguationData":[TD([[makeQuery(id+"F0.imprint","IMPRINT",EDGE,{"derivedFrom":sQuery(id+"F0.wireOp",EDGE,"E57")}),1.0]])]});
            var Q3;
            Q3=makeQuery(id+"F0.imprint","IMPRINT",FACE,{"disambiguationData":[TD([[makeQuery(id+"F0.imprint","IMPRINT",EDGE,{"derivedFrom":sQuery(id+"F0.wireOp",EDGE,"E111")}),-1.0]])]});
            var Q4;
            Q4=makeQuery(id+"F0.imprint","IMPRINT",FACE,{"disambiguationData":[TD([[makeQuery(id+"F0.imprint","IMPRINT",EDGE,{"derivedFrom":sQuery(id+"F0.wireOp",EDGE,"E97")}),1.0]])]});
            var Q5;
            Q5=makeQuery(id+"F0.imprint","IMPRINT",FACE,{"disambiguationData":[TD([[makeQuery(id+"F0.imprint","IMPRINT",EDGE,{"derivedFrom":sQuery(id+"F0.wireOp",EDGE,"E140")}),-1.0]])]});
            var Q6;
            Q6=makeQuery(id+"F0.imprint","IMPRINT",FACE,{"disambiguationData":[TD([[makeQuery(id+"F0.imprint","IMPRINT",EDGE,{"derivedFrom":sQuery(id+"F0.wireOp",EDGE,"E42")}),1.0]])]});
            extrude(context, id + "F2", {"entities" : qUnion([Q0, Q1, Q2, Q3, Q4, Q5, Q6]), "operationType" : NewBodyOperationType.ADD, "depth" : 1.04 * mm});
        }
        {
            var Q0;
            {var subQ0=sQuery(id+"F0.wireOp",EDGE,"E127");var subQ1=sQuery(id+"F0.wireOp",EDGE,"E126");var subQ2=sQuery(id+"F0.wireOp",EDGE,"E125");var subQ3=sQuery(id+"F0.wireOp",EDGE,"E124");var subQ4=sQuery(id+"F0.wireOp",EDGE,"E123");var subQ5=sQuery(id+"F0.wireOp",EDGE,"E120");var subQ6=sQuery(id+"F0.wireOp",EDGE,"E56");var subQ7=sQuery(id+"F0.wireOp",EDGE,"E55");var subQ8=sQuery(id+"F0.wireOp",EDGE,"E54");var subQ9=sQuery(id+"F0.wireOp",EDGE,"E53");var subQ10=sQuery(id+"F0.wireOp",EDGE,"E52");var subQ11=sQuery(id+"F0.wireOp",EDGE,"E51");var subQ12=sQuery(id+"F0.wireOp",EDGE,"E50");var subQ13=sQuery(id+"F0.wireOp",EDGE,"E49");var subQ14=sQuery(id+"F0.wireOp",EDGE,"E48");var subQ15=sQuery(id+"F0.wireOp",EDGE,"E47");var subQ16=sQuery(id+"F0.wireOp",EDGE,"E122");var subQ17=sQuery(id+"F0.wireOp",EDGE,"E121");var subQ18=sQuery(id+"F0.wireOp",EDGE,"E46");Q0=makeQuery(id+"F2.boolean.opBoolean","SPLIT",FACE,{"disambiguationData":[TD([makeQuery(id+"F1.opExtrude","SWEPT_FACE",FACE,{"disambiguationData":[OSD([subQ18])]})])],"derivedFrom":makeQuery(id+"F1.opExtrude","CAP_FACE",FACE,{"disambiguationData":[OSD([subQ18,subQ15,subQ14,subQ13,subQ12,subQ11,subQ10,subQ9,subQ8,subQ7,subQ6,subQ5,subQ17,subQ16,subQ4,subQ3,subQ2,subQ1,subQ0,sQuery(id+"F0.wireOp",EDGE,"E242"),sQuery(id+"F0.wireOp",EDGE,"E243"),sQuery(id+"F0.wireOp",EDGE,"E244"),sQuery(id+"F0.wireOp",EDGE,"E245"),sQuery(id+"F0.wireOp",EDGE,"E246"),sQuery(id+"F0.wireOp",EDGE,"E247"),sQuery(id+"F0.wireOp",EDGE,"E248"),sQuery(id+"F0.wireOp",EDGE,"E249"),sQuery(id+"F0.wireOp",EDGE,"E250"),sQuery(id+"F0.wireOp",EDGE,"E251"),sQuery(id+"F0.wireOp",EDGE,"E252"),sQuery(id+"F0.wireOp",EDGE,"E253"),sQuery(id+"F0.wireOp",EDGE,"E254"),sQuery(id+"F0.wireOp",EDGE,"E255"),sQuery(id+"F0.wireOp",EDGE,"E256"),sQuery(id+"F0.wireOp",EDGE,"E257"),sQuery(id+"F0.wireOp",EDGE,"E258"),sQuery(id+"F0.wireOp",EDGE,"E259"),sQuery(id+"F0.wireOp",EDGE,"E260"),sQuery(id+"F0.wireOp",EDGE,"E261"),sQuery(id+"F0.wireOp",EDGE,"E262"),sQuery(id+"F0.wireOp",EDGE,"E263"),sQuery(id+"F0.wireOp",EDGE,"E264"),sQuery(id+"F0.wireOp",EDGE,"E265"),sQuery(id+"F0.wireOp",EDGE,"E266"),sQuery(id+"F0.wireOp",EDGE,"E267"),sQuery(id+"F0.wireOp",EDGE,"E268"),sQuery(id+"F0.wireOp",EDGE,"E269"),sQuery(id+"F0.wireOp",EDGE,"E270"),sQuery(id+"F0.wireOp",EDGE,"E271")])],"isStart":false})});}
            var Q1;
            Q1=makeQuery(id+"F2.boolean.opBoolean","SPLIT",FACE,{"disambiguationData":[TD([makeQuery(id+"F2.opExtrude","SWEPT_FACE",FACE,{"disambiguationData":[OSD([sQuery(id+"F0.wireOp",EDGE,"E192")])]})])],"derivedFrom":makeQuery(id+"F1.opExtrude","CAP_FACE",FACE,{"disambiguationData":[OSD([sQuery(id+"F0.wireOp",EDGE,"E46"),sQuery(id+"F0.wireOp",EDGE,"E47"),sQuery(id+"F0.wireOp",EDGE,"E48"),sQuery(id+"F0.wireOp",EDGE,"E49"),sQuery(id+"F0.wireOp",EDGE,"E50"),sQuery(id+"F0.wireOp",EDGE,"E51"),sQuery(id+"F0.wireOp",EDGE,"E52"),sQuery(id+"F0.wireOp",EDGE,"E53"),sQuery(id+"F0.wireOp",EDGE,"E54"),sQuery(id+"F0.wireOp",EDGE,"E55"),sQuery(id+"F0.wireOp",EDGE,"E56"),sQuery(id+"F0.wireOp",EDGE,"E120"),sQuery(id+"F0.wireOp",EDGE,"E121"),sQuery(id+"F0.wireOp",EDGE,"E122"),sQuery(id+"F0.wireOp",EDGE,"E123"),sQuery(id+"F0.wireOp",EDGE,"E124"),sQuery(id+"F0.wireOp",EDGE,"E125"),sQuery(id+"F0.wireOp",EDGE,"E126"),sQuery(id+"F0.wireOp",EDGE,"E127"),sQuery(id+"F0.wireOp",EDGE,"E242"),sQuery(id+"F0.wireOp",EDGE,"E243"),sQuery(id+"F0.wireOp",EDGE,"E244"),sQuery(id+"F0.wireOp",EDGE,"E245"),sQuery(id+"F0.wireOp",EDGE,"E246"),sQuery(id+"F0.wireOp",EDGE,"E247"),sQuery(id+"F0.wireOp",EDGE,"E248"),sQuery(id+"F0.wireOp",EDGE,"E249"),sQuery(id+"F0.wireOp",EDGE,"E250"),sQuery(id+"F0.wireOp",EDGE,"E251"),sQuery(id+"F0.wireOp",EDGE,"E252"),sQuery(id+"F0.wireOp",EDGE,"E253"),sQuery(id+"F0.wireOp",EDGE,"E254"),sQuery(id+"F0.wireOp",EDGE,"E255"),sQuery(id+"F0.wireOp",EDGE,"E256"),sQuery(id+"F0.wireOp",EDGE,"E257"),sQuery(id+"F0.wireOp",EDGE,"E258"),sQuery(id+"F0.wireOp",EDGE,"E259"),sQuery(id+"F0.wireOp",EDGE,"E260"),sQuery(id+"F0.wireOp",EDGE,"E261"),sQuery(id+"F0.wireOp",EDGE,"E262"),sQuery(id+"F0.wireOp",EDGE,"E263"),sQuery(id+"F0.wireOp",EDGE,"E264"),sQuery(id+"F0.wireOp",EDGE,"E265"),sQuery(id+"F0.wireOp",EDGE,"E266"),sQuery(id+"F0.wireOp",EDGE,"E267"),sQuery(id+"F0.wireOp",EDGE,"E268"),sQuery(id+"F0.wireOp",EDGE,"E269"),sQuery(id+"F0.wireOp",EDGE,"E270"),sQuery(id+"F0.wireOp",EDGE,"E271")])],"isStart":false})});
            var Q2;
            Q2=makeQuery(id+"F2.boolean.opBoolean","SPLIT",FACE,{"disambiguationData":[TD([makeQuery(id+"F2.opExtrude","SWEPT_FACE",FACE,{"disambiguationData":[OSD([sQuery(id+"F0.wireOp",EDGE,"E193")])]})])],"derivedFrom":makeQuery(id+"F1.opExtrude","CAP_FACE",FACE,{"disambiguationData":[OSD([sQuery(id+"F0.wireOp",EDGE,"E46"),sQuery(id+"F0.wireOp",EDGE,"E47"),sQuery(id+"F0.wireOp",EDGE,"E48"),sQuery(id+"F0.wireOp",EDGE,"E49"),sQuery(id+"F0.wireOp",EDGE,"E50"),sQuery(id+"F0.wireOp",EDGE,"E51"),sQuery(id+"F0.wireOp",EDGE,"E52"),sQuery(id+"F0.wireOp",EDGE,"E53"),sQuery(id+"F0.wireOp",EDGE,"E54"),sQuery(id+"F0.wireOp",EDGE,"E55"),sQuery(id+"F0.wireOp",EDGE,"E56"),sQuery(id+"F0.wireOp",EDGE,"E120"),sQuery(id+"F0.wireOp",EDGE,"E121"),sQuery(id+"F0.wireOp",EDGE,"E122"),sQuery(id+"F0.wireOp",EDGE,"E123"),sQuery(id+"F0.wireOp",EDGE,"E124"),sQuery(id+"F0.wireOp",EDGE,"E125"),sQuery(id+"F0.wireOp",EDGE,"E126"),sQuery(id+"F0.wireOp",EDGE,"E127"),sQuery(id+"F0.wireOp",EDGE,"E242"),sQuery(id+"F0.wireOp",EDGE,"E243"),sQuery(id+"F0.wireOp",EDGE,"E244"),sQuery(id+"F0.wireOp",EDGE,"E245"),sQuery(id+"F0.wireOp",EDGE,"E246"),sQuery(id+"F0.wireOp",EDGE,"E247"),sQuery(id+"F0.wireOp",EDGE,"E248"),sQuery(id+"F0.wireOp",EDGE,"E249"),sQuery(id+"F0.wireOp",EDGE,"E250"),sQuery(id+"F0.wireOp",EDGE,"E251"),sQuery(id+"F0.wireOp",EDGE,"E252"),sQuery(id+"F0.wireOp",EDGE,"E253"),sQuery(id+"F0.wireOp",EDGE,"E254"),sQuery(id+"F0.wireOp",EDGE,"E255"),sQuery(id+"F0.wireOp",EDGE,"E256"),sQuery(id+"F0.wireOp",EDGE,"E257"),sQuery(id+"F0.wireOp",EDGE,"E258"),sQuery(id+"F0.wireOp",EDGE,"E259"),sQuery(id+"F0.wireOp",EDGE,"E260"),sQuery(id+"F0.wireOp",EDGE,"E261"),sQuery(id+"F0.wireOp",EDGE,"E262"),sQuery(id+"F0.wireOp",EDGE,"E263"),sQuery(id+"F0.wireOp",EDGE,"E264"),sQuery(id+"F0.wireOp",EDGE,"E265"),sQuery(id+"F0.wireOp",EDGE,"E266"),sQuery(id+"F0.wireOp",EDGE,"E267"),sQuery(id+"F0.wireOp",EDGE,"E268"),sQuery(id+"F0.wireOp",EDGE,"E269"),sQuery(id+"F0.wireOp",EDGE,"E270"),sQuery(id+"F0.wireOp",EDGE,"E271")])],"isStart":false})});
            var Q3;
            Q3=makeQuery(id+"F2.boolean.opBoolean","SPLIT",FACE,{"disambiguationData":[TD([makeQuery(id+"F2.opExtrude","SWEPT_FACE",FACE,{"disambiguationData":[OSD([sQuery(id+"F0.wireOp",EDGE,"E200")])]})])],"derivedFrom":makeQuery(id+"F1.opExtrude","CAP_FACE",FACE,{"disambiguationData":[OSD([sQuery(id+"F0.wireOp",EDGE,"E46"),sQuery(id+"F0.wireOp",EDGE,"E47"),sQuery(id+"F0.wireOp",EDGE,"E48"),sQuery(id+"F0.wireOp",EDGE,"E49"),sQuery(id+"F0.wireOp",EDGE,"E50"),sQuery(id+"F0.wireOp",EDGE,"E51"),sQuery(id+"F0.wireOp",EDGE,"E52"),sQuery(id+"F0.wireOp",EDGE,"E53"),sQuery(id+"F0.wireOp",EDGE,"E54"),sQuery(id+"F0.wireOp",EDGE,"E55"),sQuery(id+"F0.wireOp",EDGE,"E56"),sQuery(id+"F0.wireOp",EDGE,"E120"),sQuery(id+"F0.wireOp",EDGE,"E121"),sQuery(id+"F0.wireOp",EDGE,"E122"),sQuery(id+"F0.wireOp",EDGE,"E123"),sQuery(id+"F0.wireOp",EDGE,"E124"),sQuery(id+"F0.wireOp",EDGE,"E125"),sQuery(id+"F0.wireOp",EDGE,"E126"),sQuery(id+"F0.wireOp",EDGE,"E127"),sQuery(id+"F0.wireOp",EDGE,"E242"),sQuery(id+"F0.wireOp",EDGE,"E243"),sQuery(id+"F0.wireOp",EDGE,"E244"),sQuery(id+"F0.wireOp",EDGE,"E245"),sQuery(id+"F0.wireOp",EDGE,"E246"),sQuery(id+"F0.wireOp",EDGE,"E247"),sQuery(id+"F0.wireOp",EDGE,"E248"),sQuery(id+"F0.wireOp",EDGE,"E249"),sQuery(id+"F0.wireOp",EDGE,"E250"),sQuery(id+"F0.wireOp",EDGE,"E251"),sQuery(id+"F0.wireOp",EDGE,"E252"),sQuery(id+"F0.wireOp",EDGE,"E253"),sQuery(id+"F0.wireOp",EDGE,"E254"),sQuery(id+"F0.wireOp",EDGE,"E255"),sQuery(id+"F0.wireOp",EDGE,"E256"),sQuery(id+"F0.wireOp",EDGE,"E257"),sQuery(id+"F0.wireOp",EDGE,"E258"),sQuery(id+"F0.wireOp",EDGE,"E259"),sQuery(id+"F0.wireOp",EDGE,"E260"),sQuery(id+"F0.wireOp",EDGE,"E261"),sQuery(id+"F0.wireOp",EDGE,"E262"),sQuery(id+"F0.wireOp",EDGE,"E263"),sQuery(id+"F0.wireOp",EDGE,"E264"),sQuery(id+"F0.wireOp",EDGE,"E265"),sQuery(id+"F0.wireOp",EDGE,"E266"),sQuery(id+"F0.wireOp",EDGE,"E267"),sQuery(id+"F0.wireOp",EDGE,"E268"),sQuery(id+"F0.wireOp",EDGE,"E269"),sQuery(id+"F0.wireOp",EDGE,"E270"),sQuery(id+"F0.wireOp",EDGE,"E271")])],"isStart":false})});
            var Q4;
            Q4=makeQuery(id+"F2.boolean.opBoolean","SPLIT",FACE,{"disambiguationData":[TD([makeQuery(id+"F2.opExtrude","SWEPT_FACE",FACE,{"disambiguationData":[OSD([sQuery(id+"F0.wireOp",EDGE,"E202")])]})])],"derivedFrom":makeQuery(id+"F1.opExtrude","CAP_FACE",FACE,{"disambiguationData":[OSD([sQuery(id+"F0.wireOp",EDGE,"E46"),sQuery(id+"F0.wireOp",EDGE,"E47"),sQuery(id+"F0.wireOp",EDGE,"E48"),sQuery(id+"F0.wireOp",EDGE,"E49"),sQuery(id+"F0.wireOp",EDGE,"E50"),sQuery(id+"F0.wireOp",EDGE,"E51"),sQuery(id+"F0.wireOp",EDGE,"E52"),sQuery(id+"F0.wireOp",EDGE,"E53"),sQuery(id+"F0.wireOp",EDGE,"E54"),sQuery(id+"F0.wireOp",EDGE,"E55"),sQuery(id+"F0.wireOp",EDGE,"E56"),sQuery(id+"F0.wireOp",EDGE,"E120"),sQuery(id+"F0.wireOp",EDGE,"E121"),sQuery(id+"F0.wireOp",EDGE,"E122"),sQuery(id+"F0.wireOp",EDGE,"E123"),sQuery(id+"F0.wireOp",EDGE,"E124"),sQuery(id+"F0.wireOp",EDGE,"E125"),sQuery(id+"F0.wireOp",EDGE,"E126"),sQuery(id+"F0.wireOp",EDGE,"E127"),sQuery(id+"F0.wireOp",EDGE,"E242"),sQuery(id+"F0.wireOp",EDGE,"E243"),sQuery(id+"F0.wireOp",EDGE,"E244"),sQuery(id+"F0.wireOp",EDGE,"E245"),sQuery(id+"F0.wireOp",EDGE,"E246"),sQuery(id+"F0.wireOp",EDGE,"E247"),sQuery(id+"F0.wireOp",EDGE,"E248"),sQuery(id+"F0.wireOp",EDGE,"E249"),sQuery(id+"F0.wireOp",EDGE,"E250"),sQuery(id+"F0.wireOp",EDGE,"E251"),sQuery(id+"F0.wireOp",EDGE,"E252"),sQuery(id+"F0.wireOp",EDGE,"E253"),sQuery(id+"F0.wireOp",EDGE,"E254"),sQuery(id+"F0.wireOp",EDGE,"E255"),sQuery(id+"F0.wireOp",EDGE,"E256"),sQuery(id+"F0.wireOp",EDGE,"E257"),sQuery(id+"F0.wireOp",EDGE,"E258"),sQuery(id+"F0.wireOp",EDGE,"E259"),sQuery(id+"F0.wireOp",EDGE,"E260"),sQuery(id+"F0.wireOp",EDGE,"E261"),sQuery(id+"F0.wireOp",EDGE,"E262"),sQuery(id+"F0.wireOp",EDGE,"E263"),sQuery(id+"F0.wireOp",EDGE,"E264"),sQuery(id+"F0.wireOp",EDGE,"E265"),sQuery(id+"F0.wireOp",EDGE,"E266"),sQuery(id+"F0.wireOp",EDGE,"E267"),sQuery(id+"F0.wireOp",EDGE,"E268"),sQuery(id+"F0.wireOp",EDGE,"E269"),sQuery(id+"F0.wireOp",EDGE,"E270"),sQuery(id+"F0.wireOp",EDGE,"E271")])],"isStart":false})});
            var Q5;
            Q5=makeQuery(id+"F2.boolean.opBoolean","SPLIT",FACE,{"disambiguationData":[TD([makeQuery(id+"F2.opExtrude","SWEPT_FACE",FACE,{"disambiguationData":[OSD([sQuery(id+"F0.wireOp",EDGE,"E205")])]})])],"derivedFrom":makeQuery(id+"F1.opExtrude","CAP_FACE",FACE,{"disambiguationData":[OSD([sQuery(id+"F0.wireOp",EDGE,"E46"),sQuery(id+"F0.wireOp",EDGE,"E47"),sQuery(id+"F0.wireOp",EDGE,"E48"),sQuery(id+"F0.wireOp",EDGE,"E49"),sQuery(id+"F0.wireOp",EDGE,"E50"),sQuery(id+"F0.wireOp",EDGE,"E51"),sQuery(id+"F0.wireOp",EDGE,"E52"),sQuery(id+"F0.wireOp",EDGE,"E53"),sQuery(id+"F0.wireOp",EDGE,"E54"),sQuery(id+"F0.wireOp",EDGE,"E55"),sQuery(id+"F0.wireOp",EDGE,"E56"),sQuery(id+"F0.wireOp",EDGE,"E120"),sQuery(id+"F0.wireOp",EDGE,"E121"),sQuery(id+"F0.wireOp",EDGE,"E122"),sQuery(id+"F0.wireOp",EDGE,"E123"),sQuery(id+"F0.wireOp",EDGE,"E124"),sQuery(id+"F0.wireOp",EDGE,"E125"),sQuery(id+"F0.wireOp",EDGE,"E126"),sQuery(id+"F0.wireOp",EDGE,"E127"),sQuery(id+"F0.wireOp",EDGE,"E242"),sQuery(id+"F0.wireOp",EDGE,"E243"),sQuery(id+"F0.wireOp",EDGE,"E244"),sQuery(id+"F0.wireOp",EDGE,"E245"),sQuery(id+"F0.wireOp",EDGE,"E246"),sQuery(id+"F0.wireOp",EDGE,"E247"),sQuery(id+"F0.wireOp",EDGE,"E248"),sQuery(id+"F0.wireOp",EDGE,"E249"),sQuery(id+"F0.wireOp",EDGE,"E250"),sQuery(id+"F0.wireOp",EDGE,"E251"),sQuery(id+"F0.wireOp",EDGE,"E252"),sQuery(id+"F0.wireOp",EDGE,"E253"),sQuery(id+"F0.wireOp",EDGE,"E254"),sQuery(id+"F0.wireOp",EDGE,"E255"),sQuery(id+"F0.wireOp",EDGE,"E256"),sQuery(id+"F0.wireOp",EDGE,"E257"),sQuery(id+"F0.wireOp",EDGE,"E258"),sQuery(id+"F0.wireOp",EDGE,"E259"),sQuery(id+"F0.wireOp",EDGE,"E260"),sQuery(id+"F0.wireOp",EDGE,"E261"),sQuery(id+"F0.wireOp",EDGE,"E262"),sQuery(id+"F0.wireOp",EDGE,"E263"),sQuery(id+"F0.wireOp",EDGE,"E264"),sQuery(id+"F0.wireOp",EDGE,"E265"),sQuery(id+"F0.wireOp",EDGE,"E266"),sQuery(id+"F0.wireOp",EDGE,"E267"),sQuery(id+"F0.wireOp",EDGE,"E268"),sQuery(id+"F0.wireOp",EDGE,"E269"),sQuery(id+"F0.wireOp",EDGE,"E270"),sQuery(id+"F0.wireOp",EDGE,"E271")])],"isStart":false})});
            var Q6;
            Q6=makeQuery(id+"F2.boolean.opBoolean","SPLIT",FACE,{"disambiguationData":[TD([makeQuery(id+"F2.opExtrude","SWEPT_FACE",FACE,{"disambiguationData":[OSD([sQuery(id+"F0.wireOp",EDGE,"E207")])]})])],"derivedFrom":makeQuery(id+"F1.opExtrude","CAP_FACE",FACE,{"disambiguationData":[OSD([sQuery(id+"F0.wireOp",EDGE,"E46"),sQuery(id+"F0.wireOp",EDGE,"E47"),sQuery(id+"F0.wireOp",EDGE,"E48"),sQuery(id+"F0.wireOp",EDGE,"E49"),sQuery(id+"F0.wireOp",EDGE,"E50"),sQuery(id+"F0.wireOp",EDGE,"E51"),sQuery(id+"F0.wireOp",EDGE,"E52"),sQuery(id+"F0.wireOp",EDGE,"E53"),sQuery(id+"F0.wireOp",EDGE,"E54"),sQuery(id+"F0.wireOp",EDGE,"E55"),sQuery(id+"F0.wireOp",EDGE,"E56"),sQuery(id+"F0.wireOp",EDGE,"E120"),sQuery(id+"F0.wireOp",EDGE,"E121"),sQuery(id+"F0.wireOp",EDGE,"E122"),sQuery(id+"F0.wireOp",EDGE,"E123"),sQuery(id+"F0.wireOp",EDGE,"E124"),sQuery(id+"F0.wireOp",EDGE,"E125"),sQuery(id+"F0.wireOp",EDGE,"E126"),sQuery(id+"F0.wireOp",EDGE,"E127"),sQuery(id+"F0.wireOp",EDGE,"E242"),sQuery(id+"F0.wireOp",EDGE,"E243"),sQuery(id+"F0.wireOp",EDGE,"E244"),sQuery(id+"F0.wireOp",EDGE,"E245"),sQuery(id+"F0.wireOp",EDGE,"E246"),sQuery(id+"F0.wireOp",EDGE,"E247"),sQuery(id+"F0.wireOp",EDGE,"E248"),sQuery(id+"F0.wireOp",EDGE,"E249"),sQuery(id+"F0.wireOp",EDGE,"E250"),sQuery(id+"F0.wireOp",EDGE,"E251"),sQuery(id+"F0.wireOp",EDGE,"E252"),sQuery(id+"F0.wireOp",EDGE,"E253"),sQuery(id+"F0.wireOp",EDGE,"E254"),sQuery(id+"F0.wireOp",EDGE,"E255"),sQuery(id+"F0.wireOp",EDGE,"E256"),sQuery(id+"F0.wireOp",EDGE,"E257"),sQuery(id+"F0.wireOp",EDGE,"E258"),sQuery(id+"F0.wireOp",EDGE,"E259"),sQuery(id+"F0.wireOp",EDGE,"E260"),sQuery(id+"F0.wireOp",EDGE,"E261"),sQuery(id+"F0.wireOp",EDGE,"E262"),sQuery(id+"F0.wireOp",EDGE,"E263"),sQuery(id+"F0.wireOp",EDGE,"E264"),sQuery(id+"F0.wireOp",EDGE,"E265"),sQuery(id+"F0.wireOp",EDGE,"E266"),sQuery(id+"F0.wireOp",EDGE,"E267"),sQuery(id+"F0.wireOp",EDGE,"E268"),sQuery(id+"F0.wireOp",EDGE,"E269"),sQuery(id+"F0.wireOp",EDGE,"E270"),sQuery(id+"F0.wireOp",EDGE,"E271")])],"isStart":false})});
            var Q7;
            Q7=makeQuery(id+"F2.boolean.opBoolean","SPLIT",FACE,{"disambiguationData":[TD([makeQuery(id+"F2.opExtrude","SWEPT_FACE",FACE,{"disambiguationData":[OSD([sQuery(id+"F0.wireOp",EDGE,"E209")])]})])],"derivedFrom":makeQuery(id+"F1.opExtrude","CAP_FACE",FACE,{"disambiguationData":[OSD([sQuery(id+"F0.wireOp",EDGE,"E46"),sQuery(id+"F0.wireOp",EDGE,"E47"),sQuery(id+"F0.wireOp",EDGE,"E48"),sQuery(id+"F0.wireOp",EDGE,"E49"),sQuery(id+"F0.wireOp",EDGE,"E50"),sQuery(id+"F0.wireOp",EDGE,"E51"),sQuery(id+"F0.wireOp",EDGE,"E52"),sQuery(id+"F0.wireOp",EDGE,"E53"),sQuery(id+"F0.wireOp",EDGE,"E54"),sQuery(id+"F0.wireOp",EDGE,"E55"),sQuery(id+"F0.wireOp",EDGE,"E56"),sQuery(id+"F0.wireOp",EDGE,"E120"),sQuery(id+"F0.wireOp",EDGE,"E121"),sQuery(id+"F0.wireOp",EDGE,"E122"),sQuery(id+"F0.wireOp",EDGE,"E123"),sQuery(id+"F0.wireOp",EDGE,"E124"),sQuery(id+"F0.wireOp",EDGE,"E125"),sQuery(id+"F0.wireOp",EDGE,"E126"),sQuery(id+"F0.wireOp",EDGE,"E127"),sQuery(id+"F0.wireOp",EDGE,"E242"),sQuery(id+"F0.wireOp",EDGE,"E243"),sQuery(id+"F0.wireOp",EDGE,"E244"),sQuery(id+"F0.wireOp",EDGE,"E245"),sQuery(id+"F0.wireOp",EDGE,"E246"),sQuery(id+"F0.wireOp",EDGE,"E247"),sQuery(id+"F0.wireOp",EDGE,"E248"),sQuery(id+"F0.wireOp",EDGE,"E249"),sQuery(id+"F0.wireOp",EDGE,"E250"),sQuery(id+"F0.wireOp",EDGE,"E251"),sQuery(id+"F0.wireOp",EDGE,"E252"),sQuery(id+"F0.wireOp",EDGE,"E253"),sQuery(id+"F0.wireOp",EDGE,"E254"),sQuery(id+"F0.wireOp",EDGE,"E255"),sQuery(id+"F0.wireOp",EDGE,"E256"),sQuery(id+"F0.wireOp",EDGE,"E257"),sQuery(id+"F0.wireOp",EDGE,"E258"),sQuery(id+"F0.wireOp",EDGE,"E259"),sQuery(id+"F0.wireOp",EDGE,"E260"),sQuery(id+"F0.wireOp",EDGE,"E261"),sQuery(id+"F0.wireOp",EDGE,"E262"),sQuery(id+"F0.wireOp",EDGE,"E263"),sQuery(id+"F0.wireOp",EDGE,"E264"),sQuery(id+"F0.wireOp",EDGE,"E265"),sQuery(id+"F0.wireOp",EDGE,"E266"),sQuery(id+"F0.wireOp",EDGE,"E267"),sQuery(id+"F0.wireOp",EDGE,"E268"),sQuery(id+"F0.wireOp",EDGE,"E269"),sQuery(id+"F0.wireOp",EDGE,"E270"),sQuery(id+"F0.wireOp",EDGE,"E271")])],"isStart":false})});
            var Q8;
            Q8=makeQuery(id+"F2.opExtrude","CAP_FACE",FACE,{"disambiguationData":[OSD([sQuery(id+"F0.wireOp",EDGE,"E0"),sQuery(id+"F0.wireOp",EDGE,"E1"),sQuery(id+"F0.wireOp",EDGE,"E2"),sQuery(id+"F0.wireOp",EDGE,"E3"),sQuery(id+"F0.wireOp",EDGE,"E4"),sQuery(id+"F0.wireOp",EDGE,"E5"),sQuery(id+"F0.wireOp",EDGE,"E6"),sQuery(id+"F0.wireOp",EDGE,"E7"),sQuery(id+"F0.wireOp",EDGE,"E8"),sQuery(id+"F0.wireOp",EDGE,"E9"),sQuery(id+"F0.wireOp",EDGE,"E10"),sQuery(id+"F0.wireOp",EDGE,"E11"),sQuery(id+"F0.wireOp",EDGE,"E12"),sQuery(id+"F0.wireOp",EDGE,"E13"),sQuery(id+"F0.wireOp",EDGE,"E14"),sQuery(id+"F0.wireOp",EDGE,"E15"),sQuery(id+"F0.wireOp",EDGE,"E16"),sQuery(id+"F0.wireOp",EDGE,"E17"),sQuery(id+"F0.wireOp",EDGE,"E18"),sQuery(id+"F0.wireOp",EDGE,"E19"),sQuery(id+"F0.wireOp",EDGE,"E20"),sQuery(id+"F0.wireOp",EDGE,"E21"),sQuery(id+"F0.wireOp",EDGE,"E22"),sQuery(id+"F0.wireOp",EDGE,"E23"),sQuery(id+"F0.wireOp",EDGE,"E24"),sQuery(id+"F0.wireOp",EDGE,"E25"),sQuery(id+"F0.wireOp",EDGE,"E26"),sQuery(id+"F0.wireOp",EDGE,"E27"),sQuery(id+"F0.wireOp",EDGE,"E28"),sQuery(id+"F0.wireOp",EDGE,"E29"),sQuery(id+"F0.wireOp",EDGE,"E30"),sQuery(id+"F0.wireOp",EDGE,"E31"),sQuery(id+"F0.wireOp",EDGE,"E32"),sQuery(id+"F0.wireOp",EDGE,"E33"),sQuery(id+"F0.wireOp",EDGE,"E34"),sQuery(id+"F0.wireOp",EDGE,"E35"),sQuery(id+"F0.wireOp",EDGE,"E36"),sQuery(id+"F0.wireOp",EDGE,"E37"),sQuery(id+"F0.wireOp",EDGE,"E38"),sQuery(id+"F0.wireOp",EDGE,"E39"),sQuery(id+"F0.wireOp",EDGE,"E40"),sQuery(id+"F0.wireOp",EDGE,"E41")])],"isStart":false});
            extrude(context, id + "F3", {"entities" : qUnion([Q0, Q1, Q2, Q3, Q4, Q5, Q6, Q7]), "endBoundEntityFace" : qUnion([Q8]), "depth" : 1.52 * mm});
        }
        {
            var Q0;
            Q0=makeQuery(id+"F1.opExtrude","SWEPT_BODY",BODY,{"disambiguationData":[OSD([sQuery(id+"F0.wireOp",EDGE,"E46"),sQuery(id+"F0.wireOp",EDGE,"E47"),sQuery(id+"F0.wireOp",EDGE,"E48"),sQuery(id+"F0.wireOp",EDGE,"E49"),sQuery(id+"F0.wireOp",EDGE,"E50"),sQuery(id+"F0.wireOp",EDGE,"E51"),sQuery(id+"F0.wireOp",EDGE,"E52"),sQuery(id+"F0.wireOp",EDGE,"E53"),sQuery(id+"F0.wireOp",EDGE,"E54"),sQuery(id+"F0.wireOp",EDGE,"E55"),sQuery(id+"F0.wireOp",EDGE,"E56"),sQuery(id+"F0.wireOp",EDGE,"E120"),sQuery(id+"F0.wireOp",EDGE,"E121"),sQuery(id+"F0.wireOp",EDGE,"E122"),sQuery(id+"F0.wireOp",EDGE,"E123"),sQuery(id+"F0.wireOp",EDGE,"E124"),sQuery(id+"F0.wireOp",EDGE,"E125"),sQuery(id+"F0.wireOp",EDGE,"E126"),sQuery(id+"F0.wireOp",EDGE,"E127"),sQuery(id+"F0.wireOp",EDGE,"E242"),sQuery(id+"F0.wireOp",EDGE,"E243"),sQuery(id+"F0.wireOp",EDGE,"E244"),sQuery(id+"F0.wireOp",EDGE,"E245"),sQuery(id+"F0.wireOp",EDGE,"E246"),sQuery(id+"F0.wireOp",EDGE,"E247"),sQuery(id+"F0.wireOp",EDGE,"E248"),sQuery(id+"F0.wireOp",EDGE,"E249"),sQuery(id+"F0.wireOp",EDGE,"E250"),sQuery(id+"F0.wireOp",EDGE,"E251"),sQuery(id+"F0.wireOp",EDGE,"E252"),sQuery(id+"F0.wireOp",EDGE,"E253"),sQuery(id+"F0.wireOp",EDGE,"E254"),sQuery(id+"F0.wireOp",EDGE,"E255"),sQuery(id+"F0.wireOp",EDGE,"E256"),sQuery(id+"F0.wireOp",EDGE,"E257"),sQuery(id+"F0.wireOp",EDGE,"E258"),sQuery(id+"F0.wireOp",EDGE,"E259"),sQuery(id+"F0.wireOp",EDGE,"E260"),sQuery(id+"F0.wireOp",EDGE,"E261"),sQuery(id+"F0.wireOp",EDGE,"E262"),sQuery(id+"F0.wireOp",EDGE,"E263"),sQuery(id+"F0.wireOp",EDGE,"E264"),sQuery(id+"F0.wireOp",EDGE,"E265"),sQuery(id+"F0.wireOp",EDGE,"E266"),sQuery(id+"F0.wireOp",EDGE,"E267"),sQuery(id+"F0.wireOp",EDGE,"E268"),sQuery(id+"F0.wireOp",EDGE,"E269"),sQuery(id+"F0.wireOp",EDGE,"E270"),sQuery(id+"F0.wireOp",EDGE,"E271")])]});
            var Q1;
            {var subQ0=sQuery(id+"F0.wireOp",EDGE,"E271");var subQ1=sQuery(id+"F0.wireOp",EDGE,"E270");var subQ2=sQuery(id+"F0.wireOp",EDGE,"E269");var subQ3=sQuery(id+"F0.wireOp",EDGE,"E268");var subQ4=sQuery(id+"F0.wireOp",EDGE,"E267");var subQ5=sQuery(id+"F0.wireOp",EDGE,"E266");var subQ6=sQuery(id+"F0.wireOp",EDGE,"E265");var subQ7=sQuery(id+"F0.wireOp",EDGE,"E264");var subQ8=sQuery(id+"F0.wireOp",EDGE,"E263");var subQ9=sQuery(id+"F0.wireOp",EDGE,"E262");var subQ10=sQuery(id+"F0.wireOp",EDGE,"E261");var subQ11=sQuery(id+"F0.wireOp",EDGE,"E260");var subQ12=sQuery(id+"F0.wireOp",EDGE,"E259");var subQ13=sQuery(id+"F0.wireOp",EDGE,"E258");var subQ14=sQuery(id+"F0.wireOp",EDGE,"E257");var subQ15=sQuery(id+"F0.wireOp",EDGE,"E256");var subQ16=sQuery(id+"F0.wireOp",EDGE,"E255");var subQ17=sQuery(id+"F0.wireOp",EDGE,"E254");var subQ18=sQuery(id+"F0.wireOp",EDGE,"E253");var subQ19=sQuery(id+"F0.wireOp",EDGE,"E252");var subQ20=sQuery(id+"F0.wireOp",EDGE,"E251");var subQ21=sQuery(id+"F0.wireOp",EDGE,"E250");var subQ22=sQuery(id+"F0.wireOp",EDGE,"E249");var subQ23=sQuery(id+"F0.wireOp",EDGE,"E248");var subQ24=sQuery(id+"F0.wireOp",EDGE,"E247");var subQ25=sQuery(id+"F0.wireOp",EDGE,"E246");var subQ26=sQuery(id+"F0.wireOp",EDGE,"E245");var subQ27=sQuery(id+"F0.wireOp",EDGE,"E244");var subQ28=sQuery(id+"F0.wireOp",EDGE,"E243");var subQ29=sQuery(id+"F0.wireOp",EDGE,"E242");var subQ30=sQuery(id+"F0.wireOp",EDGE,"E127");var subQ31=sQuery(id+"F0.wireOp",EDGE,"E126");var subQ32=sQuery(id+"F0.wireOp",EDGE,"E125");var subQ33=sQuery(id+"F0.wireOp",EDGE,"E124");var subQ34=sQuery(id+"F0.wireOp",EDGE,"E123");var subQ35=sQuery(id+"F0.wireOp",EDGE,"E122");var subQ36=sQuery(id+"F0.wireOp",EDGE,"E121");var subQ37=sQuery(id+"F0.wireOp",EDGE,"E120");var subQ38=sQuery(id+"F0.wireOp",EDGE,"E56");var subQ39=sQuery(id+"F0.wireOp",EDGE,"E55");var subQ40=sQuery(id+"F0.wireOp",EDGE,"E54");var subQ41=sQuery(id+"F0.wireOp",EDGE,"E53");var subQ42=sQuery(id+"F0.wireOp",EDGE,"E52");var subQ43=sQuery(id+"F0.wireOp",EDGE,"E51");var subQ44=sQuery(id+"F0.wireOp",EDGE,"E50");var subQ45=sQuery(id+"F0.wireOp",EDGE,"E49");var subQ46=sQuery(id+"F0.wireOp",EDGE,"E48");var subQ47=sQuery(id+"F0.wireOp",EDGE,"E47");var subQ48=sQuery(id+"F0.wireOp",EDGE,"E46");Q1=makeQuery(id+"F3.opExtrude","SWEPT_BODY",BODY,{"disambiguationData":[OSD([subQ48,subQ47,subQ46,subQ45,subQ44,subQ43,subQ42,subQ41,subQ40,subQ39,subQ38,subQ37,subQ36,subQ35,subQ34,subQ33,subQ32,subQ31,subQ30,subQ29,subQ28,subQ27,subQ26,subQ25,subQ24,subQ23,subQ22,subQ21,subQ20,subQ19,subQ18,subQ17,subQ16,subQ15,subQ14,subQ13,subQ12,subQ11,subQ10,subQ9,subQ8,subQ7,subQ6,subQ5,subQ4,subQ3,subQ2,subQ1,subQ0]),TDD([makeQuery(id+"F2.boolean.opBoolean","SPLIT",FACE,{"disambiguationData":[TD([makeQuery(id+"F2.opExtrude","SWEPT_FACE",FACE,{"disambiguationData":[OSD([sQuery(id+"F0.wireOp",EDGE,"E200")])]})])],"derivedFrom":makeQuery(id+"F1.opExtrude","CAP_FACE",FACE,{"disambiguationData":[OSD([subQ48,subQ47,subQ46,subQ45,subQ44,subQ43,subQ42,subQ41,subQ40,subQ39,subQ38,subQ37,subQ36,subQ35,subQ34,subQ33,subQ32,subQ31,subQ30,subQ29,subQ28,subQ27,subQ26,subQ25,subQ24,subQ23,subQ22,subQ21,subQ20,subQ19,subQ18,subQ17,subQ16,subQ15,subQ14,subQ13,subQ12,subQ11,subQ10,subQ9,subQ8,subQ7,subQ6,subQ5,subQ4,subQ3,subQ2,subQ1,subQ0])],"isStart":false})})])]});}
            var Q2;
            {var subQ0=sQuery(id+"F0.wireOp",EDGE,"E271");var subQ1=sQuery(id+"F0.wireOp",EDGE,"E270");var subQ2=sQuery(id+"F0.wireOp",EDGE,"E269");var subQ3=sQuery(id+"F0.wireOp",EDGE,"E268");var subQ4=sQuery(id+"F0.wireOp",EDGE,"E267");var subQ5=sQuery(id+"F0.wireOp",EDGE,"E266");var subQ6=sQuery(id+"F0.wireOp",EDGE,"E265");var subQ7=sQuery(id+"F0.wireOp",EDGE,"E264");var subQ8=sQuery(id+"F0.wireOp",EDGE,"E263");var subQ9=sQuery(id+"F0.wireOp",EDGE,"E262");var subQ10=sQuery(id+"F0.wireOp",EDGE,"E261");var subQ11=sQuery(id+"F0.wireOp",EDGE,"E260");var subQ12=sQuery(id+"F0.wireOp",EDGE,"E259");var subQ13=sQuery(id+"F0.wireOp",EDGE,"E258");var subQ14=sQuery(id+"F0.wireOp",EDGE,"E257");var subQ15=sQuery(id+"F0.wireOp",EDGE,"E256");var subQ16=sQuery(id+"F0.wireOp",EDGE,"E255");var subQ17=sQuery(id+"F0.wireOp",EDGE,"E254");var subQ18=sQuery(id+"F0.wireOp",EDGE,"E253");var subQ19=sQuery(id+"F0.wireOp",EDGE,"E252");var subQ20=sQuery(id+"F0.wireOp",EDGE,"E251");var subQ21=sQuery(id+"F0.wireOp",EDGE,"E250");var subQ22=sQuery(id+"F0.wireOp",EDGE,"E249");var subQ23=sQuery(id+"F0.wireOp",EDGE,"E248");var subQ24=sQuery(id+"F0.wireOp",EDGE,"E247");var subQ25=sQuery(id+"F0.wireOp",EDGE,"E246");var subQ26=sQuery(id+"F0.wireOp",EDGE,"E245");var subQ27=sQuery(id+"F0.wireOp",EDGE,"E244");var subQ28=sQuery(id+"F0.wireOp",EDGE,"E243");var subQ29=sQuery(id+"F0.wireOp",EDGE,"E242");var subQ30=sQuery(id+"F0.wireOp",EDGE,"E127");var subQ31=sQuery(id+"F0.wireOp",EDGE,"E126");var subQ32=sQuery(id+"F0.wireOp",EDGE,"E125");var subQ33=sQuery(id+"F0.wireOp",EDGE,"E124");var subQ34=sQuery(id+"F0.wireOp",EDGE,"E123");var subQ35=sQuery(id+"F0.wireOp",EDGE,"E122");var subQ36=sQuery(id+"F0.wireOp",EDGE,"E121");var subQ37=sQuery(id+"F0.wireOp",EDGE,"E120");var subQ38=sQuery(id+"F0.wireOp",EDGE,"E56");var subQ39=sQuery(id+"F0.wireOp",EDGE,"E55");var subQ40=sQuery(id+"F0.wireOp",EDGE,"E54");var subQ41=sQuery(id+"F0.wireOp",EDGE,"E53");var subQ42=sQuery(id+"F0.wireOp",EDGE,"E52");var subQ43=sQuery(id+"F0.wireOp",EDGE,"E51");var subQ44=sQuery(id+"F0.wireOp",EDGE,"E50");var subQ45=sQuery(id+"F0.wireOp",EDGE,"E49");var subQ46=sQuery(id+"F0.wireOp",EDGE,"E48");var subQ47=sQuery(id+"F0.wireOp",EDGE,"E47");var subQ48=sQuery(id+"F0.wireOp",EDGE,"E46");Q2=makeQuery(id+"F3.opExtrude","SWEPT_BODY",BODY,{"disambiguationData":[OSD([subQ48,subQ47,subQ46,subQ45,subQ44,subQ43,subQ42,subQ41,subQ40,subQ39,subQ38,subQ37,subQ36,subQ35,subQ34,subQ33,subQ32,subQ31,subQ30,subQ29,subQ28,subQ27,subQ26,subQ25,subQ24,subQ23,subQ22,subQ21,subQ20,subQ19,subQ18,subQ17,subQ16,subQ15,subQ14,subQ13,subQ12,subQ11,subQ10,subQ9,subQ8,subQ7,subQ6,subQ5,subQ4,subQ3,subQ2,subQ1,subQ0]),TDD([makeQuery(id+"F2.boolean.opBoolean","SPLIT",FACE,{"disambiguationData":[TD([makeQuery(id+"F2.opExtrude","SWEPT_FACE",FACE,{"disambiguationData":[OSD([sQuery(id+"F0.wireOp",EDGE,"E205")])]})])],"derivedFrom":makeQuery(id+"F1.opExtrude","CAP_FACE",FACE,{"disambiguationData":[OSD([subQ48,subQ47,subQ46,subQ45,subQ44,subQ43,subQ42,subQ41,subQ40,subQ39,subQ38,subQ37,subQ36,subQ35,subQ34,subQ33,subQ32,subQ31,subQ30,subQ29,subQ28,subQ27,subQ26,subQ25,subQ24,subQ23,subQ22,subQ21,subQ20,subQ19,subQ18,subQ17,subQ16,subQ15,subQ14,subQ13,subQ12,subQ11,subQ10,subQ9,subQ8,subQ7,subQ6,subQ5,subQ4,subQ3,subQ2,subQ1,subQ0])],"isStart":false})})])]});}
            var Q3;
            {var subQ0=sQuery(id+"F0.wireOp",EDGE,"E271");var subQ1=sQuery(id+"F0.wireOp",EDGE,"E270");var subQ2=sQuery(id+"F0.wireOp",EDGE,"E269");var subQ3=sQuery(id+"F0.wireOp",EDGE,"E268");var subQ4=sQuery(id+"F0.wireOp",EDGE,"E267");var subQ5=sQuery(id+"F0.wireOp",EDGE,"E266");var subQ6=sQuery(id+"F0.wireOp",EDGE,"E265");var subQ7=sQuery(id+"F0.wireOp",EDGE,"E264");var subQ8=sQuery(id+"F0.wireOp",EDGE,"E263");var subQ9=sQuery(id+"F0.wireOp",EDGE,"E262");var subQ10=sQuery(id+"F0.wireOp",EDGE,"E261");var subQ11=sQuery(id+"F0.wireOp",EDGE,"E260");var subQ12=sQuery(id+"F0.wireOp",EDGE,"E259");var subQ13=sQuery(id+"F0.wireOp",EDGE,"E258");var subQ14=sQuery(id+"F0.wireOp",EDGE,"E257");var subQ15=sQuery(id+"F0.wireOp",EDGE,"E256");var subQ16=sQuery(id+"F0.wireOp",EDGE,"E255");var subQ17=sQuery(id+"F0.wireOp",EDGE,"E254");var subQ18=sQuery(id+"F0.wireOp",EDGE,"E253");var subQ19=sQuery(id+"F0.wireOp",EDGE,"E252");var subQ20=sQuery(id+"F0.wireOp",EDGE,"E251");var subQ21=sQuery(id+"F0.wireOp",EDGE,"E250");var subQ22=sQuery(id+"F0.wireOp",EDGE,"E249");var subQ23=sQuery(id+"F0.wireOp",EDGE,"E248");var subQ24=sQuery(id+"F0.wireOp",EDGE,"E247");var subQ25=sQuery(id+"F0.wireOp",EDGE,"E246");var subQ26=sQuery(id+"F0.wireOp",EDGE,"E245");var subQ27=sQuery(id+"F0.wireOp",EDGE,"E244");var subQ28=sQuery(id+"F0.wireOp",EDGE,"E243");var subQ29=sQuery(id+"F0.wireOp",EDGE,"E242");var subQ30=sQuery(id+"F0.wireOp",EDGE,"E127");var subQ31=sQuery(id+"F0.wireOp",EDGE,"E126");var subQ32=sQuery(id+"F0.wireOp",EDGE,"E125");var subQ33=sQuery(id+"F0.wireOp",EDGE,"E124");var subQ34=sQuery(id+"F0.wireOp",EDGE,"E123");var subQ35=sQuery(id+"F0.wireOp",EDGE,"E122");var subQ36=sQuery(id+"F0.wireOp",EDGE,"E121");var subQ37=sQuery(id+"F0.wireOp",EDGE,"E120");var subQ38=sQuery(id+"F0.wireOp",EDGE,"E56");var subQ39=sQuery(id+"F0.wireOp",EDGE,"E55");var subQ40=sQuery(id+"F0.wireOp",EDGE,"E54");var subQ41=sQuery(id+"F0.wireOp",EDGE,"E53");var subQ42=sQuery(id+"F0.wireOp",EDGE,"E52");var subQ43=sQuery(id+"F0.wireOp",EDGE,"E51");var subQ44=sQuery(id+"F0.wireOp",EDGE,"E50");var subQ45=sQuery(id+"F0.wireOp",EDGE,"E49");var subQ46=sQuery(id+"F0.wireOp",EDGE,"E48");var subQ47=sQuery(id+"F0.wireOp",EDGE,"E47");var subQ48=sQuery(id+"F0.wireOp",EDGE,"E46");Q3=makeQuery(id+"F3.opExtrude","SWEPT_BODY",BODY,{"disambiguationData":[OSD([subQ48,subQ47,subQ46,subQ45,subQ44,subQ43,subQ42,subQ41,subQ40,subQ39,subQ38,subQ37,subQ36,subQ35,subQ34,subQ33,subQ32,subQ31,subQ30,subQ29,subQ28,subQ27,subQ26,subQ25,subQ24,subQ23,subQ22,subQ21,subQ20,subQ19,subQ18,subQ17,subQ16,subQ15,subQ14,subQ13,subQ12,subQ11,subQ10,subQ9,subQ8,subQ7,subQ6,subQ5,subQ4,subQ3,subQ2,subQ1,subQ0]),TDD([makeQuery(id+"F2.boolean.opBoolean","SPLIT",FACE,{"disambiguationData":[TD([makeQuery(id+"F2.opExtrude","SWEPT_FACE",FACE,{"disambiguationData":[OSD([sQuery(id+"F0.wireOp",EDGE,"E207")])]})])],"derivedFrom":makeQuery(id+"F1.opExtrude","CAP_FACE",FACE,{"disambiguationData":[OSD([subQ48,subQ47,subQ46,subQ45,subQ44,subQ43,subQ42,subQ41,subQ40,subQ39,subQ38,subQ37,subQ36,subQ35,subQ34,subQ33,subQ32,subQ31,subQ30,subQ29,subQ28,subQ27,subQ26,subQ25,subQ24,subQ23,subQ22,subQ21,subQ20,subQ19,subQ18,subQ17,subQ16,subQ15,subQ14,subQ13,subQ12,subQ11,subQ10,subQ9,subQ8,subQ7,subQ6,subQ5,subQ4,subQ3,subQ2,subQ1,subQ0])],"isStart":false})})])]});}
            var Q4;
            {var subQ0=sQuery(id+"F0.wireOp",EDGE,"E271");var subQ1=sQuery(id+"F0.wireOp",EDGE,"E270");var subQ2=sQuery(id+"F0.wireOp",EDGE,"E269");var subQ3=sQuery(id+"F0.wireOp",EDGE,"E268");var subQ4=sQuery(id+"F0.wireOp",EDGE,"E267");var subQ5=sQuery(id+"F0.wireOp",EDGE,"E266");var subQ6=sQuery(id+"F0.wireOp",EDGE,"E265");var subQ7=sQuery(id+"F0.wireOp",EDGE,"E264");var subQ8=sQuery(id+"F0.wireOp",EDGE,"E263");var subQ9=sQuery(id+"F0.wireOp",EDGE,"E262");var subQ10=sQuery(id+"F0.wireOp",EDGE,"E261");var subQ11=sQuery(id+"F0.wireOp",EDGE,"E260");var subQ12=sQuery(id+"F0.wireOp",EDGE,"E259");var subQ13=sQuery(id+"F0.wireOp",EDGE,"E258");var subQ14=sQuery(id+"F0.wireOp",EDGE,"E257");var subQ15=sQuery(id+"F0.wireOp",EDGE,"E256");var subQ16=sQuery(id+"F0.wireOp",EDGE,"E255");var subQ17=sQuery(id+"F0.wireOp",EDGE,"E254");var subQ18=sQuery(id+"F0.wireOp",EDGE,"E253");var subQ19=sQuery(id+"F0.wireOp",EDGE,"E252");var subQ20=sQuery(id+"F0.wireOp",EDGE,"E251");var subQ21=sQuery(id+"F0.wireOp",EDGE,"E250");var subQ22=sQuery(id+"F0.wireOp",EDGE,"E249");var subQ23=sQuery(id+"F0.wireOp",EDGE,"E248");var subQ24=sQuery(id+"F0.wireOp",EDGE,"E247");var subQ25=sQuery(id+"F0.wireOp",EDGE,"E246");var subQ26=sQuery(id+"F0.wireOp",EDGE,"E245");var subQ27=sQuery(id+"F0.wireOp",EDGE,"E244");var subQ28=sQuery(id+"F0.wireOp",EDGE,"E243");var subQ29=sQuery(id+"F0.wireOp",EDGE,"E242");var subQ30=sQuery(id+"F0.wireOp",EDGE,"E127");var subQ31=sQuery(id+"F0.wireOp",EDGE,"E126");var subQ32=sQuery(id+"F0.wireOp",EDGE,"E125");var subQ33=sQuery(id+"F0.wireOp",EDGE,"E124");var subQ34=sQuery(id+"F0.wireOp",EDGE,"E123");var subQ35=sQuery(id+"F0.wireOp",EDGE,"E122");var subQ36=sQuery(id+"F0.wireOp",EDGE,"E121");var subQ37=sQuery(id+"F0.wireOp",EDGE,"E120");var subQ38=sQuery(id+"F0.wireOp",EDGE,"E56");var subQ39=sQuery(id+"F0.wireOp",EDGE,"E55");var subQ40=sQuery(id+"F0.wireOp",EDGE,"E54");var subQ41=sQuery(id+"F0.wireOp",EDGE,"E53");var subQ42=sQuery(id+"F0.wireOp",EDGE,"E52");var subQ43=sQuery(id+"F0.wireOp",EDGE,"E51");var subQ44=sQuery(id+"F0.wireOp",EDGE,"E50");var subQ45=sQuery(id+"F0.wireOp",EDGE,"E49");var subQ46=sQuery(id+"F0.wireOp",EDGE,"E48");var subQ47=sQuery(id+"F0.wireOp",EDGE,"E47");var subQ48=sQuery(id+"F0.wireOp",EDGE,"E46");Q4=makeQuery(id+"F3.opExtrude","SWEPT_BODY",BODY,{"disambiguationData":[OSD([subQ48,subQ47,subQ46,subQ45,subQ44,subQ43,subQ42,subQ41,subQ40,subQ39,subQ38,subQ37,subQ36,subQ35,subQ34,subQ33,subQ32,subQ31,subQ30,subQ29,subQ28,subQ27,subQ26,subQ25,subQ24,subQ23,subQ22,subQ21,subQ20,subQ19,subQ18,subQ17,subQ16,subQ15,subQ14,subQ13,subQ12,subQ11,subQ10,subQ9,subQ8,subQ7,subQ6,subQ5,subQ4,subQ3,subQ2,subQ1,subQ0]),TDD([makeQuery(id+"F2.boolean.opBoolean","SPLIT",FACE,{"disambiguationData":[TD([makeQuery(id+"F2.opExtrude","SWEPT_FACE",FACE,{"disambiguationData":[OSD([sQuery(id+"F0.wireOp",EDGE,"E82")])]})])],"derivedFrom":makeQuery(id+"F1.opExtrude","CAP_FACE",FACE,{"disambiguationData":[OSD([subQ48,subQ47,subQ46,subQ45,subQ44,subQ43,subQ42,subQ41,subQ40,subQ39,subQ38,subQ37,subQ36,subQ35,subQ34,subQ33,subQ32,subQ31,subQ30,subQ29,subQ28,subQ27,subQ26,subQ25,subQ24,subQ23,subQ22,subQ21,subQ20,subQ19,subQ18,subQ17,subQ16,subQ15,subQ14,subQ13,subQ12,subQ11,subQ10,subQ9,subQ8,subQ7,subQ6,subQ5,subQ4,subQ3,subQ2,subQ1,subQ0])],"isStart":false})})])]});}
            var Q5;
            {var subQ0=sQuery(id+"F0.wireOp",EDGE,"E271");var subQ1=sQuery(id+"F0.wireOp",EDGE,"E270");var subQ2=sQuery(id+"F0.wireOp",EDGE,"E269");var subQ3=sQuery(id+"F0.wireOp",EDGE,"E268");var subQ4=sQuery(id+"F0.wireOp",EDGE,"E267");var subQ5=sQuery(id+"F0.wireOp",EDGE,"E266");var subQ6=sQuery(id+"F0.wireOp",EDGE,"E265");var subQ7=sQuery(id+"F0.wireOp",EDGE,"E264");var subQ8=sQuery(id+"F0.wireOp",EDGE,"E263");var subQ9=sQuery(id+"F0.wireOp",EDGE,"E262");var subQ10=sQuery(id+"F0.wireOp",EDGE,"E261");var subQ11=sQuery(id+"F0.wireOp",EDGE,"E260");var subQ12=sQuery(id+"F0.wireOp",EDGE,"E259");var subQ13=sQuery(id+"F0.wireOp",EDGE,"E258");var subQ14=sQuery(id+"F0.wireOp",EDGE,"E257");var subQ15=sQuery(id+"F0.wireOp",EDGE,"E256");var subQ16=sQuery(id+"F0.wireOp",EDGE,"E255");var subQ17=sQuery(id+"F0.wireOp",EDGE,"E254");var subQ18=sQuery(id+"F0.wireOp",EDGE,"E253");var subQ19=sQuery(id+"F0.wireOp",EDGE,"E252");var subQ20=sQuery(id+"F0.wireOp",EDGE,"E251");var subQ21=sQuery(id+"F0.wireOp",EDGE,"E250");var subQ22=sQuery(id+"F0.wireOp",EDGE,"E249");var subQ23=sQuery(id+"F0.wireOp",EDGE,"E248");var subQ24=sQuery(id+"F0.wireOp",EDGE,"E247");var subQ25=sQuery(id+"F0.wireOp",EDGE,"E246");var subQ26=sQuery(id+"F0.wireOp",EDGE,"E245");var subQ27=sQuery(id+"F0.wireOp",EDGE,"E244");var subQ28=sQuery(id+"F0.wireOp",EDGE,"E243");var subQ29=sQuery(id+"F0.wireOp",EDGE,"E242");var subQ30=sQuery(id+"F0.wireOp",EDGE,"E127");var subQ31=sQuery(id+"F0.wireOp",EDGE,"E126");var subQ32=sQuery(id+"F0.wireOp",EDGE,"E125");var subQ33=sQuery(id+"F0.wireOp",EDGE,"E124");var subQ34=sQuery(id+"F0.wireOp",EDGE,"E123");var subQ35=sQuery(id+"F0.wireOp",EDGE,"E122");var subQ36=sQuery(id+"F0.wireOp",EDGE,"E121");var subQ37=sQuery(id+"F0.wireOp",EDGE,"E120");var subQ38=sQuery(id+"F0.wireOp",EDGE,"E56");var subQ39=sQuery(id+"F0.wireOp",EDGE,"E55");var subQ40=sQuery(id+"F0.wireOp",EDGE,"E54");var subQ41=sQuery(id+"F0.wireOp",EDGE,"E53");var subQ42=sQuery(id+"F0.wireOp",EDGE,"E52");var subQ43=sQuery(id+"F0.wireOp",EDGE,"E51");var subQ44=sQuery(id+"F0.wireOp",EDGE,"E50");var subQ45=sQuery(id+"F0.wireOp",EDGE,"E49");var subQ46=sQuery(id+"F0.wireOp",EDGE,"E48");var subQ47=sQuery(id+"F0.wireOp",EDGE,"E47");var subQ48=sQuery(id+"F0.wireOp",EDGE,"E46");Q5=makeQuery(id+"F3.opExtrude","SWEPT_BODY",BODY,{"disambiguationData":[OSD([subQ48,subQ47,subQ46,subQ45,subQ44,subQ43,subQ42,subQ41,subQ40,subQ39,subQ38,subQ37,subQ36,subQ35,subQ34,subQ33,subQ32,subQ31,subQ30,subQ29,subQ28,subQ27,subQ26,subQ25,subQ24,subQ23,subQ22,subQ21,subQ20,subQ19,subQ18,subQ17,subQ16,subQ15,subQ14,subQ13,subQ12,subQ11,subQ10,subQ9,subQ8,subQ7,subQ6,subQ5,subQ4,subQ3,subQ2,subQ1,subQ0]),TDD([makeQuery(id+"F2.boolean.opBoolean","SPLIT",FACE,{"disambiguationData":[TD([makeQuery(id+"F2.opExtrude","SWEPT_FACE",FACE,{"disambiguationData":[OSD([sQuery(id+"F0.wireOp",EDGE,"E85")])]})])],"derivedFrom":makeQuery(id+"F1.opExtrude","CAP_FACE",FACE,{"disambiguationData":[OSD([subQ48,subQ47,subQ46,subQ45,subQ44,subQ43,subQ42,subQ41,subQ40,subQ39,subQ38,subQ37,subQ36,subQ35,subQ34,subQ33,subQ32,subQ31,subQ30,subQ29,subQ28,subQ27,subQ26,subQ25,subQ24,subQ23,subQ22,subQ21,subQ20,subQ19,subQ18,subQ17,subQ16,subQ15,subQ14,subQ13,subQ12,subQ11,subQ10,subQ9,subQ8,subQ7,subQ6,subQ5,subQ4,subQ3,subQ2,subQ1,subQ0])],"isStart":false})})])]});}
            var Q6;
            {var subQ0=sQuery(id+"F0.wireOp",EDGE,"E271");var subQ1=sQuery(id+"F0.wireOp",EDGE,"E270");var subQ2=sQuery(id+"F0.wireOp",EDGE,"E269");var subQ3=sQuery(id+"F0.wireOp",EDGE,"E268");var subQ4=sQuery(id+"F0.wireOp",EDGE,"E267");var subQ5=sQuery(id+"F0.wireOp",EDGE,"E266");var subQ6=sQuery(id+"F0.wireOp",EDGE,"E265");var subQ7=sQuery(id+"F0.wireOp",EDGE,"E264");var subQ8=sQuery(id+"F0.wireOp",EDGE,"E263");var subQ9=sQuery(id+"F0.wireOp",EDGE,"E262");var subQ10=sQuery(id+"F0.wireOp",EDGE,"E261");var subQ11=sQuery(id+"F0.wireOp",EDGE,"E260");var subQ12=sQuery(id+"F0.wireOp",EDGE,"E259");var subQ13=sQuery(id+"F0.wireOp",EDGE,"E258");var subQ14=sQuery(id+"F0.wireOp",EDGE,"E257");var subQ15=sQuery(id+"F0.wireOp",EDGE,"E256");var subQ16=sQuery(id+"F0.wireOp",EDGE,"E255");var subQ17=sQuery(id+"F0.wireOp",EDGE,"E254");var subQ18=sQuery(id+"F0.wireOp",EDGE,"E253");var subQ19=sQuery(id+"F0.wireOp",EDGE,"E252");var subQ20=sQuery(id+"F0.wireOp",EDGE,"E251");var subQ21=sQuery(id+"F0.wireOp",EDGE,"E250");var subQ22=sQuery(id+"F0.wireOp",EDGE,"E249");var subQ23=sQuery(id+"F0.wireOp",EDGE,"E248");var subQ24=sQuery(id+"F0.wireOp",EDGE,"E247");var subQ25=sQuery(id+"F0.wireOp",EDGE,"E246");var subQ26=sQuery(id+"F0.wireOp",EDGE,"E245");var subQ27=sQuery(id+"F0.wireOp",EDGE,"E244");var subQ28=sQuery(id+"F0.wireOp",EDGE,"E243");var subQ29=sQuery(id+"F0.wireOp",EDGE,"E242");var subQ30=sQuery(id+"F0.wireOp",EDGE,"E127");var subQ31=sQuery(id+"F0.wireOp",EDGE,"E126");var subQ32=sQuery(id+"F0.wireOp",EDGE,"E125");var subQ33=sQuery(id+"F0.wireOp",EDGE,"E124");var subQ34=sQuery(id+"F0.wireOp",EDGE,"E123");var subQ35=sQuery(id+"F0.wireOp",EDGE,"E122");var subQ36=sQuery(id+"F0.wireOp",EDGE,"E121");var subQ37=sQuery(id+"F0.wireOp",EDGE,"E120");var subQ38=sQuery(id+"F0.wireOp",EDGE,"E56");var subQ39=sQuery(id+"F0.wireOp",EDGE,"E55");var subQ40=sQuery(id+"F0.wireOp",EDGE,"E54");var subQ41=sQuery(id+"F0.wireOp",EDGE,"E53");var subQ42=sQuery(id+"F0.wireOp",EDGE,"E52");var subQ43=sQuery(id+"F0.wireOp",EDGE,"E51");var subQ44=sQuery(id+"F0.wireOp",EDGE,"E50");var subQ45=sQuery(id+"F0.wireOp",EDGE,"E49");var subQ46=sQuery(id+"F0.wireOp",EDGE,"E48");var subQ47=sQuery(id+"F0.wireOp",EDGE,"E47");var subQ48=sQuery(id+"F0.wireOp",EDGE,"E46");Q6=makeQuery(id+"F3.opExtrude","SWEPT_BODY",BODY,{"disambiguationData":[OSD([subQ48,subQ47,subQ46,subQ45,subQ44,subQ43,subQ42,subQ41,subQ40,subQ39,subQ38,subQ37,subQ36,subQ35,subQ34,subQ33,subQ32,subQ31,subQ30,subQ29,subQ28,subQ27,subQ26,subQ25,subQ24,subQ23,subQ22,subQ21,subQ20,subQ19,subQ18,subQ17,subQ16,subQ15,subQ14,subQ13,subQ12,subQ11,subQ10,subQ9,subQ8,subQ7,subQ6,subQ5,subQ4,subQ3,subQ2,subQ1,subQ0]),TDD([makeQuery(id+"F2.boolean.opBoolean","SPLIT",FACE,{"disambiguationData":[TD([makeQuery(id+"F2.opExtrude","SWEPT_FACE",FACE,{"disambiguationData":[OSD([sQuery(id+"F0.wireOp",EDGE,"E88")])]})])],"derivedFrom":makeQuery(id+"F1.opExtrude","CAP_FACE",FACE,{"disambiguationData":[OSD([subQ48,subQ47,subQ46,subQ45,subQ44,subQ43,subQ42,subQ41,subQ40,subQ39,subQ38,subQ37,subQ36,subQ35,subQ34,subQ33,subQ32,subQ31,subQ30,subQ29,subQ28,subQ27,subQ26,subQ25,subQ24,subQ23,subQ22,subQ21,subQ20,subQ19,subQ18,subQ17,subQ16,subQ15,subQ14,subQ13,subQ12,subQ11,subQ10,subQ9,subQ8,subQ7,subQ6,subQ5,subQ4,subQ3,subQ2,subQ1,subQ0])],"isStart":false})})])]});}
            var Q7;
            {var subQ0=sQuery(id+"F0.wireOp",EDGE,"E271");var subQ1=sQuery(id+"F0.wireOp",EDGE,"E270");var subQ2=sQuery(id+"F0.wireOp",EDGE,"E269");var subQ3=sQuery(id+"F0.wireOp",EDGE,"E268");var subQ4=sQuery(id+"F0.wireOp",EDGE,"E267");var subQ5=sQuery(id+"F0.wireOp",EDGE,"E266");var subQ6=sQuery(id+"F0.wireOp",EDGE,"E265");var subQ7=sQuery(id+"F0.wireOp",EDGE,"E264");var subQ8=sQuery(id+"F0.wireOp",EDGE,"E263");var subQ9=sQuery(id+"F0.wireOp",EDGE,"E262");var subQ10=sQuery(id+"F0.wireOp",EDGE,"E261");var subQ11=sQuery(id+"F0.wireOp",EDGE,"E260");var subQ12=sQuery(id+"F0.wireOp",EDGE,"E259");var subQ13=sQuery(id+"F0.wireOp",EDGE,"E258");var subQ14=sQuery(id+"F0.wireOp",EDGE,"E257");var subQ15=sQuery(id+"F0.wireOp",EDGE,"E256");var subQ16=sQuery(id+"F0.wireOp",EDGE,"E255");var subQ17=sQuery(id+"F0.wireOp",EDGE,"E254");var subQ18=sQuery(id+"F0.wireOp",EDGE,"E253");var subQ19=sQuery(id+"F0.wireOp",EDGE,"E252");var subQ20=sQuery(id+"F0.wireOp",EDGE,"E251");var subQ21=sQuery(id+"F0.wireOp",EDGE,"E250");var subQ22=sQuery(id+"F0.wireOp",EDGE,"E249");var subQ23=sQuery(id+"F0.wireOp",EDGE,"E248");var subQ24=sQuery(id+"F0.wireOp",EDGE,"E247");var subQ25=sQuery(id+"F0.wireOp",EDGE,"E246");var subQ26=sQuery(id+"F0.wireOp",EDGE,"E245");var subQ27=sQuery(id+"F0.wireOp",EDGE,"E244");var subQ28=sQuery(id+"F0.wireOp",EDGE,"E243");var subQ29=sQuery(id+"F0.wireOp",EDGE,"E242");var subQ30=sQuery(id+"F0.wireOp",EDGE,"E127");var subQ31=sQuery(id+"F0.wireOp",EDGE,"E126");var subQ32=sQuery(id+"F0.wireOp",EDGE,"E125");var subQ33=sQuery(id+"F0.wireOp",EDGE,"E124");var subQ34=sQuery(id+"F0.wireOp",EDGE,"E123");var subQ35=sQuery(id+"F0.wireOp",EDGE,"E122");var subQ36=sQuery(id+"F0.wireOp",EDGE,"E121");var subQ37=sQuery(id+"F0.wireOp",EDGE,"E120");var subQ38=sQuery(id+"F0.wireOp",EDGE,"E56");var subQ39=sQuery(id+"F0.wireOp",EDGE,"E55");var subQ40=sQuery(id+"F0.wireOp",EDGE,"E54");var subQ41=sQuery(id+"F0.wireOp",EDGE,"E53");var subQ42=sQuery(id+"F0.wireOp",EDGE,"E52");var subQ43=sQuery(id+"F0.wireOp",EDGE,"E51");var subQ44=sQuery(id+"F0.wireOp",EDGE,"E50");var subQ45=sQuery(id+"F0.wireOp",EDGE,"E49");var subQ46=sQuery(id+"F0.wireOp",EDGE,"E48");var subQ47=sQuery(id+"F0.wireOp",EDGE,"E47");var subQ48=sQuery(id+"F0.wireOp",EDGE,"E46");Q7=makeQuery(id+"F3.opExtrude","SWEPT_BODY",BODY,{"disambiguationData":[OSD([subQ48,subQ47,subQ46,subQ45,subQ44,subQ43,subQ42,subQ41,subQ40,subQ39,subQ38,subQ37,subQ36,subQ35,subQ34,subQ33,subQ32,subQ31,subQ30,subQ29,subQ28,subQ27,subQ26,subQ25,subQ24,subQ23,subQ22,subQ21,subQ20,subQ19,subQ18,subQ17,subQ16,subQ15,subQ14,subQ13,subQ12,subQ11,subQ10,subQ9,subQ8,subQ7,subQ6,subQ5,subQ4,subQ3,subQ2,subQ1,subQ0]),TDD([makeQuery(id+"F2.boolean.opBoolean","SPLIT",FACE,{"disambiguationData":[TD([makeQuery(id+"F2.opExtrude","SWEPT_FACE",FACE,{"disambiguationData":[OSD([sQuery(id+"F0.wireOp",EDGE,"E91")])]})])],"derivedFrom":makeQuery(id+"F1.opExtrude","CAP_FACE",FACE,{"disambiguationData":[OSD([subQ48,subQ47,subQ46,subQ45,subQ44,subQ43,subQ42,subQ41,subQ40,subQ39,subQ38,subQ37,subQ36,subQ35,subQ34,subQ33,subQ32,subQ31,subQ30,subQ29,subQ28,subQ27,subQ26,subQ25,subQ24,subQ23,subQ22,subQ21,subQ20,subQ19,subQ18,subQ17,subQ16,subQ15,subQ14,subQ13,subQ12,subQ11,subQ10,subQ9,subQ8,subQ7,subQ6,subQ5,subQ4,subQ3,subQ2,subQ1,subQ0])],"isStart":false})})])]});}
            var Q8;
            {var subQ0=sQuery(id+"F0.wireOp",EDGE,"E271");var subQ1=sQuery(id+"F0.wireOp",EDGE,"E270");var subQ2=sQuery(id+"F0.wireOp",EDGE,"E269");var subQ3=sQuery(id+"F0.wireOp",EDGE,"E268");var subQ4=sQuery(id+"F0.wireOp",EDGE,"E267");var subQ5=sQuery(id+"F0.wireOp",EDGE,"E266");var subQ6=sQuery(id+"F0.wireOp",EDGE,"E265");var subQ7=sQuery(id+"F0.wireOp",EDGE,"E264");var subQ8=sQuery(id+"F0.wireOp",EDGE,"E263");var subQ9=sQuery(id+"F0.wireOp",EDGE,"E262");var subQ10=sQuery(id+"F0.wireOp",EDGE,"E261");var subQ11=sQuery(id+"F0.wireOp",EDGE,"E260");var subQ12=sQuery(id+"F0.wireOp",EDGE,"E259");var subQ13=sQuery(id+"F0.wireOp",EDGE,"E258");var subQ14=sQuery(id+"F0.wireOp",EDGE,"E257");var subQ15=sQuery(id+"F0.wireOp",EDGE,"E256");var subQ16=sQuery(id+"F0.wireOp",EDGE,"E255");var subQ17=sQuery(id+"F0.wireOp",EDGE,"E254");var subQ18=sQuery(id+"F0.wireOp",EDGE,"E253");var subQ19=sQuery(id+"F0.wireOp",EDGE,"E252");var subQ20=sQuery(id+"F0.wireOp",EDGE,"E251");var subQ21=sQuery(id+"F0.wireOp",EDGE,"E250");var subQ22=sQuery(id+"F0.wireOp",EDGE,"E249");var subQ23=sQuery(id+"F0.wireOp",EDGE,"E248");var subQ24=sQuery(id+"F0.wireOp",EDGE,"E247");var subQ25=sQuery(id+"F0.wireOp",EDGE,"E246");var subQ26=sQuery(id+"F0.wireOp",EDGE,"E245");var subQ27=sQuery(id+"F0.wireOp",EDGE,"E244");var subQ28=sQuery(id+"F0.wireOp",EDGE,"E243");var subQ29=sQuery(id+"F0.wireOp",EDGE,"E242");var subQ30=sQuery(id+"F0.wireOp",EDGE,"E127");var subQ31=sQuery(id+"F0.wireOp",EDGE,"E126");var subQ32=sQuery(id+"F0.wireOp",EDGE,"E125");var subQ33=sQuery(id+"F0.wireOp",EDGE,"E124");var subQ34=sQuery(id+"F0.wireOp",EDGE,"E123");var subQ35=sQuery(id+"F0.wireOp",EDGE,"E122");var subQ36=sQuery(id+"F0.wireOp",EDGE,"E121");var subQ37=sQuery(id+"F0.wireOp",EDGE,"E120");var subQ38=sQuery(id+"F0.wireOp",EDGE,"E56");var subQ39=sQuery(id+"F0.wireOp",EDGE,"E55");var subQ40=sQuery(id+"F0.wireOp",EDGE,"E54");var subQ41=sQuery(id+"F0.wireOp",EDGE,"E53");var subQ42=sQuery(id+"F0.wireOp",EDGE,"E52");var subQ43=sQuery(id+"F0.wireOp",EDGE,"E51");var subQ44=sQuery(id+"F0.wireOp",EDGE,"E50");var subQ45=sQuery(id+"F0.wireOp",EDGE,"E49");var subQ46=sQuery(id+"F0.wireOp",EDGE,"E48");var subQ47=sQuery(id+"F0.wireOp",EDGE,"E47");var subQ48=sQuery(id+"F0.wireOp",EDGE,"E46");Q8=makeQuery(id+"F3.opExtrude","SWEPT_BODY",BODY,{"disambiguationData":[OSD([subQ48,subQ47,subQ46,subQ45,subQ44,subQ43,subQ42,subQ41,subQ40,subQ39,subQ38,subQ37,subQ36,subQ35,subQ34,subQ33,subQ32,subQ31,subQ30,subQ29,subQ28,subQ27,subQ26,subQ25,subQ24,subQ23,subQ22,subQ21,subQ20,subQ19,subQ18,subQ17,subQ16,subQ15,subQ14,subQ13,subQ12,subQ11,subQ10,subQ9,subQ8,subQ7,subQ6,subQ5,subQ4,subQ3,subQ2,subQ1,subQ0]),TDD([makeQuery(id+"F2.boolean.opBoolean","SPLIT",FACE,{"disambiguationData":[TD([makeQuery(id+"F2.opExtrude","SWEPT_FACE",FACE,{"disambiguationData":[OSD([sQuery(id+"F0.wireOp",EDGE,"E94")])]})])],"derivedFrom":makeQuery(id+"F1.opExtrude","CAP_FACE",FACE,{"disambiguationData":[OSD([subQ48,subQ47,subQ46,subQ45,subQ44,subQ43,subQ42,subQ41,subQ40,subQ39,subQ38,subQ37,subQ36,subQ35,subQ34,subQ33,subQ32,subQ31,subQ30,subQ29,subQ28,subQ27,subQ26,subQ25,subQ24,subQ23,subQ22,subQ21,subQ20,subQ19,subQ18,subQ17,subQ16,subQ15,subQ14,subQ13,subQ12,subQ11,subQ10,subQ9,subQ8,subQ7,subQ6,subQ5,subQ4,subQ3,subQ2,subQ1,subQ0])],"isStart":false})})])]});}
            var Q9;
            {var subQ0=sQuery(id+"F0.wireOp",EDGE,"E271");var subQ1=sQuery(id+"F0.wireOp",EDGE,"E270");var subQ2=sQuery(id+"F0.wireOp",EDGE,"E269");var subQ3=sQuery(id+"F0.wireOp",EDGE,"E268");var subQ4=sQuery(id+"F0.wireOp",EDGE,"E267");var subQ5=sQuery(id+"F0.wireOp",EDGE,"E266");var subQ6=sQuery(id+"F0.wireOp",EDGE,"E265");var subQ7=sQuery(id+"F0.wireOp",EDGE,"E264");var subQ8=sQuery(id+"F0.wireOp",EDGE,"E263");var subQ9=sQuery(id+"F0.wireOp",EDGE,"E262");var subQ10=sQuery(id+"F0.wireOp",EDGE,"E261");var subQ11=sQuery(id+"F0.wireOp",EDGE,"E260");var subQ12=sQuery(id+"F0.wireOp",EDGE,"E259");var subQ13=sQuery(id+"F0.wireOp",EDGE,"E258");var subQ14=sQuery(id+"F0.wireOp",EDGE,"E257");var subQ15=sQuery(id+"F0.wireOp",EDGE,"E256");var subQ16=sQuery(id+"F0.wireOp",EDGE,"E255");var subQ17=sQuery(id+"F0.wireOp",EDGE,"E254");var subQ18=sQuery(id+"F0.wireOp",EDGE,"E253");var subQ19=sQuery(id+"F0.wireOp",EDGE,"E252");var subQ20=sQuery(id+"F0.wireOp",EDGE,"E251");var subQ21=sQuery(id+"F0.wireOp",EDGE,"E250");var subQ22=sQuery(id+"F0.wireOp",EDGE,"E249");var subQ23=sQuery(id+"F0.wireOp",EDGE,"E248");var subQ24=sQuery(id+"F0.wireOp",EDGE,"E247");var subQ25=sQuery(id+"F0.wireOp",EDGE,"E246");var subQ26=sQuery(id+"F0.wireOp",EDGE,"E245");var subQ27=sQuery(id+"F0.wireOp",EDGE,"E244");var subQ28=sQuery(id+"F0.wireOp",EDGE,"E243");var subQ29=sQuery(id+"F0.wireOp",EDGE,"E242");var subQ30=sQuery(id+"F0.wireOp",EDGE,"E127");var subQ31=sQuery(id+"F0.wireOp",EDGE,"E126");var subQ32=sQuery(id+"F0.wireOp",EDGE,"E125");var subQ33=sQuery(id+"F0.wireOp",EDGE,"E124");var subQ34=sQuery(id+"F0.wireOp",EDGE,"E123");var subQ35=sQuery(id+"F0.wireOp",EDGE,"E122");var subQ36=sQuery(id+"F0.wireOp",EDGE,"E121");var subQ37=sQuery(id+"F0.wireOp",EDGE,"E120");var subQ38=sQuery(id+"F0.wireOp",EDGE,"E56");var subQ39=sQuery(id+"F0.wireOp",EDGE,"E55");var subQ40=sQuery(id+"F0.wireOp",EDGE,"E54");var subQ41=sQuery(id+"F0.wireOp",EDGE,"E53");var subQ42=sQuery(id+"F0.wireOp",EDGE,"E52");var subQ43=sQuery(id+"F0.wireOp",EDGE,"E51");var subQ44=sQuery(id+"F0.wireOp",EDGE,"E50");var subQ45=sQuery(id+"F0.wireOp",EDGE,"E49");var subQ46=sQuery(id+"F0.wireOp",EDGE,"E48");var subQ47=sQuery(id+"F0.wireOp",EDGE,"E47");var subQ48=sQuery(id+"F0.wireOp",EDGE,"E46");Q9=makeQuery(id+"F3.opExtrude","SWEPT_BODY",BODY,{"disambiguationData":[OSD([subQ48,subQ47,subQ46,subQ45,subQ44,subQ43,subQ42,subQ41,subQ40,subQ39,subQ38,subQ37,subQ36,subQ35,subQ34,subQ33,subQ32,subQ31,subQ30,subQ29,subQ28,subQ27,subQ26,subQ25,subQ24,subQ23,subQ22,subQ21,subQ20,subQ19,subQ18,subQ17,subQ16,subQ15,subQ14,subQ13,subQ12,subQ11,subQ10,subQ9,subQ8,subQ7,subQ6,subQ5,subQ4,subQ3,subQ2,subQ1,subQ0]),TDD([makeQuery(id+"F2.boolean.opBoolean","SPLIT",FACE,{"disambiguationData":[TD([makeQuery(id+"F2.opExtrude","SWEPT_FACE",FACE,{"disambiguationData":[OSD([sQuery(id+"F0.wireOp",EDGE,"E202")])]})])],"derivedFrom":makeQuery(id+"F1.opExtrude","CAP_FACE",FACE,{"disambiguationData":[OSD([subQ48,subQ47,subQ46,subQ45,subQ44,subQ43,subQ42,subQ41,subQ40,subQ39,subQ38,subQ37,subQ36,subQ35,subQ34,subQ33,subQ32,subQ31,subQ30,subQ29,subQ28,subQ27,subQ26,subQ25,subQ24,subQ23,subQ22,subQ21,subQ20,subQ19,subQ18,subQ17,subQ16,subQ15,subQ14,subQ13,subQ12,subQ11,subQ10,subQ9,subQ8,subQ7,subQ6,subQ5,subQ4,subQ3,subQ2,subQ1,subQ0])],"isStart":false})})])]});}
            var Q10;
            {var subQ0=sQuery(id+"F0.wireOp",EDGE,"E271");var subQ1=sQuery(id+"F0.wireOp",EDGE,"E270");var subQ2=sQuery(id+"F0.wireOp",EDGE,"E269");var subQ3=sQuery(id+"F0.wireOp",EDGE,"E268");var subQ4=sQuery(id+"F0.wireOp",EDGE,"E267");var subQ5=sQuery(id+"F0.wireOp",EDGE,"E266");var subQ6=sQuery(id+"F0.wireOp",EDGE,"E265");var subQ7=sQuery(id+"F0.wireOp",EDGE,"E264");var subQ8=sQuery(id+"F0.wireOp",EDGE,"E263");var subQ9=sQuery(id+"F0.wireOp",EDGE,"E262");var subQ10=sQuery(id+"F0.wireOp",EDGE,"E261");var subQ11=sQuery(id+"F0.wireOp",EDGE,"E260");var subQ12=sQuery(id+"F0.wireOp",EDGE,"E259");var subQ13=sQuery(id+"F0.wireOp",EDGE,"E258");var subQ14=sQuery(id+"F0.wireOp",EDGE,"E257");var subQ15=sQuery(id+"F0.wireOp",EDGE,"E256");var subQ16=sQuery(id+"F0.wireOp",EDGE,"E255");var subQ17=sQuery(id+"F0.wireOp",EDGE,"E254");var subQ18=sQuery(id+"F0.wireOp",EDGE,"E253");var subQ19=sQuery(id+"F0.wireOp",EDGE,"E252");var subQ20=sQuery(id+"F0.wireOp",EDGE,"E251");var subQ21=sQuery(id+"F0.wireOp",EDGE,"E250");var subQ22=sQuery(id+"F0.wireOp",EDGE,"E249");var subQ23=sQuery(id+"F0.wireOp",EDGE,"E248");var subQ24=sQuery(id+"F0.wireOp",EDGE,"E247");var subQ25=sQuery(id+"F0.wireOp",EDGE,"E246");var subQ26=sQuery(id+"F0.wireOp",EDGE,"E245");var subQ27=sQuery(id+"F0.wireOp",EDGE,"E244");var subQ28=sQuery(id+"F0.wireOp",EDGE,"E243");var subQ29=sQuery(id+"F0.wireOp",EDGE,"E242");var subQ30=sQuery(id+"F0.wireOp",EDGE,"E127");var subQ31=sQuery(id+"F0.wireOp",EDGE,"E126");var subQ32=sQuery(id+"F0.wireOp",EDGE,"E125");var subQ33=sQuery(id+"F0.wireOp",EDGE,"E124");var subQ34=sQuery(id+"F0.wireOp",EDGE,"E123");var subQ35=sQuery(id+"F0.wireOp",EDGE,"E122");var subQ36=sQuery(id+"F0.wireOp",EDGE,"E121");var subQ37=sQuery(id+"F0.wireOp",EDGE,"E120");var subQ38=sQuery(id+"F0.wireOp",EDGE,"E56");var subQ39=sQuery(id+"F0.wireOp",EDGE,"E55");var subQ40=sQuery(id+"F0.wireOp",EDGE,"E54");var subQ41=sQuery(id+"F0.wireOp",EDGE,"E53");var subQ42=sQuery(id+"F0.wireOp",EDGE,"E52");var subQ43=sQuery(id+"F0.wireOp",EDGE,"E51");var subQ44=sQuery(id+"F0.wireOp",EDGE,"E50");var subQ45=sQuery(id+"F0.wireOp",EDGE,"E49");var subQ46=sQuery(id+"F0.wireOp",EDGE,"E48");var subQ47=sQuery(id+"F0.wireOp",EDGE,"E47");var subQ48=sQuery(id+"F0.wireOp",EDGE,"E46");Q10=makeQuery(id+"F3.opExtrude","SWEPT_BODY",BODY,{"disambiguationData":[OSD([subQ48,subQ47,subQ46,subQ45,subQ44,subQ43,subQ42,subQ41,subQ40,subQ39,subQ38,subQ37,subQ36,subQ35,subQ34,subQ33,subQ32,subQ31,subQ30,subQ29,subQ28,subQ27,subQ26,subQ25,subQ24,subQ23,subQ22,subQ21,subQ20,subQ19,subQ18,subQ17,subQ16,subQ15,subQ14,subQ13,subQ12,subQ11,subQ10,subQ9,subQ8,subQ7,subQ6,subQ5,subQ4,subQ3,subQ2,subQ1,subQ0]),TDD([makeQuery(id+"F2.boolean.opBoolean","SPLIT",FACE,{"disambiguationData":[TD([makeQuery(id+"F2.opExtrude","SWEPT_FACE",FACE,{"disambiguationData":[OSD([sQuery(id+"F0.wireOp",EDGE,"E209")])]})])],"derivedFrom":makeQuery(id+"F1.opExtrude","CAP_FACE",FACE,{"disambiguationData":[OSD([subQ48,subQ47,subQ46,subQ45,subQ44,subQ43,subQ42,subQ41,subQ40,subQ39,subQ38,subQ37,subQ36,subQ35,subQ34,subQ33,subQ32,subQ31,subQ30,subQ29,subQ28,subQ27,subQ26,subQ25,subQ24,subQ23,subQ22,subQ21,subQ20,subQ19,subQ18,subQ17,subQ16,subQ15,subQ14,subQ13,subQ12,subQ11,subQ10,subQ9,subQ8,subQ7,subQ6,subQ5,subQ4,subQ3,subQ2,subQ1,subQ0])],"isStart":false})})])]});}
            var Q11;
            {var subQ0=sQuery(id+"F0.wireOp",EDGE,"E271");var subQ1=sQuery(id+"F0.wireOp",EDGE,"E270");var subQ2=sQuery(id+"F0.wireOp",EDGE,"E269");var subQ3=sQuery(id+"F0.wireOp",EDGE,"E268");var subQ4=sQuery(id+"F0.wireOp",EDGE,"E267");var subQ5=sQuery(id+"F0.wireOp",EDGE,"E266");var subQ6=sQuery(id+"F0.wireOp",EDGE,"E265");var subQ7=sQuery(id+"F0.wireOp",EDGE,"E264");var subQ8=sQuery(id+"F0.wireOp",EDGE,"E263");var subQ9=sQuery(id+"F0.wireOp",EDGE,"E262");var subQ10=sQuery(id+"F0.wireOp",EDGE,"E261");var subQ11=sQuery(id+"F0.wireOp",EDGE,"E260");var subQ12=sQuery(id+"F0.wireOp",EDGE,"E259");var subQ13=sQuery(id+"F0.wireOp",EDGE,"E258");var subQ14=sQuery(id+"F0.wireOp",EDGE,"E257");var subQ15=sQuery(id+"F0.wireOp",EDGE,"E256");var subQ16=sQuery(id+"F0.wireOp",EDGE,"E255");var subQ17=sQuery(id+"F0.wireOp",EDGE,"E254");var subQ18=sQuery(id+"F0.wireOp",EDGE,"E253");var subQ19=sQuery(id+"F0.wireOp",EDGE,"E252");var subQ20=sQuery(id+"F0.wireOp",EDGE,"E251");var subQ21=sQuery(id+"F0.wireOp",EDGE,"E250");var subQ22=sQuery(id+"F0.wireOp",EDGE,"E249");var subQ23=sQuery(id+"F0.wireOp",EDGE,"E248");var subQ24=sQuery(id+"F0.wireOp",EDGE,"E247");var subQ25=sQuery(id+"F0.wireOp",EDGE,"E246");var subQ26=sQuery(id+"F0.wireOp",EDGE,"E245");var subQ27=sQuery(id+"F0.wireOp",EDGE,"E244");var subQ28=sQuery(id+"F0.wireOp",EDGE,"E243");var subQ29=sQuery(id+"F0.wireOp",EDGE,"E242");var subQ30=sQuery(id+"F0.wireOp",EDGE,"E127");var subQ31=sQuery(id+"F0.wireOp",EDGE,"E126");var subQ32=sQuery(id+"F0.wireOp",EDGE,"E125");var subQ33=sQuery(id+"F0.wireOp",EDGE,"E124");var subQ34=sQuery(id+"F0.wireOp",EDGE,"E123");var subQ35=sQuery(id+"F0.wireOp",EDGE,"E122");var subQ36=sQuery(id+"F0.wireOp",EDGE,"E121");var subQ37=sQuery(id+"F0.wireOp",EDGE,"E120");var subQ38=sQuery(id+"F0.wireOp",EDGE,"E56");var subQ39=sQuery(id+"F0.wireOp",EDGE,"E55");var subQ40=sQuery(id+"F0.wireOp",EDGE,"E54");var subQ41=sQuery(id+"F0.wireOp",EDGE,"E53");var subQ42=sQuery(id+"F0.wireOp",EDGE,"E52");var subQ43=sQuery(id+"F0.wireOp",EDGE,"E51");var subQ44=sQuery(id+"F0.wireOp",EDGE,"E50");var subQ45=sQuery(id+"F0.wireOp",EDGE,"E49");var subQ46=sQuery(id+"F0.wireOp",EDGE,"E48");var subQ47=sQuery(id+"F0.wireOp",EDGE,"E47");var subQ48=sQuery(id+"F0.wireOp",EDGE,"E46");Q11=makeQuery(id+"F3.opExtrude","SWEPT_BODY",BODY,{"disambiguationData":[OSD([subQ48,subQ47,subQ46,subQ45,subQ44,subQ43,subQ42,subQ41,subQ40,subQ39,subQ38,subQ37,subQ36,subQ35,subQ34,subQ33,subQ32,subQ31,subQ30,subQ29,subQ28,subQ27,subQ26,subQ25,subQ24,subQ23,subQ22,subQ21,subQ20,subQ19,subQ18,subQ17,subQ16,subQ15,subQ14,subQ13,subQ12,subQ11,subQ10,subQ9,subQ8,subQ7,subQ6,subQ5,subQ4,subQ3,subQ2,subQ1,subQ0]),TDD([makeQuery(id+"F2.boolean.opBoolean","SPLIT",FACE,{"disambiguationData":[TD([makeQuery(id+"F2.opExtrude","SWEPT_FACE",FACE,{"disambiguationData":[OSD([sQuery(id+"F0.wireOp",EDGE,"E192")])]})])],"derivedFrom":makeQuery(id+"F1.opExtrude","CAP_FACE",FACE,{"disambiguationData":[OSD([subQ48,subQ47,subQ46,subQ45,subQ44,subQ43,subQ42,subQ41,subQ40,subQ39,subQ38,subQ37,subQ36,subQ35,subQ34,subQ33,subQ32,subQ31,subQ30,subQ29,subQ28,subQ27,subQ26,subQ25,subQ24,subQ23,subQ22,subQ21,subQ20,subQ19,subQ18,subQ17,subQ16,subQ15,subQ14,subQ13,subQ12,subQ11,subQ10,subQ9,subQ8,subQ7,subQ6,subQ5,subQ4,subQ3,subQ2,subQ1,subQ0])],"isStart":false})})])]});}
            var Q12;
            {var subQ0=sQuery(id+"F0.wireOp",EDGE,"E271");var subQ1=sQuery(id+"F0.wireOp",EDGE,"E270");var subQ2=sQuery(id+"F0.wireOp",EDGE,"E269");var subQ3=sQuery(id+"F0.wireOp",EDGE,"E268");var subQ4=sQuery(id+"F0.wireOp",EDGE,"E267");var subQ5=sQuery(id+"F0.wireOp",EDGE,"E266");var subQ6=sQuery(id+"F0.wireOp",EDGE,"E265");var subQ7=sQuery(id+"F0.wireOp",EDGE,"E264");var subQ8=sQuery(id+"F0.wireOp",EDGE,"E263");var subQ9=sQuery(id+"F0.wireOp",EDGE,"E262");var subQ10=sQuery(id+"F0.wireOp",EDGE,"E261");var subQ11=sQuery(id+"F0.wireOp",EDGE,"E260");var subQ12=sQuery(id+"F0.wireOp",EDGE,"E259");var subQ13=sQuery(id+"F0.wireOp",EDGE,"E258");var subQ14=sQuery(id+"F0.wireOp",EDGE,"E257");var subQ15=sQuery(id+"F0.wireOp",EDGE,"E256");var subQ16=sQuery(id+"F0.wireOp",EDGE,"E255");var subQ17=sQuery(id+"F0.wireOp",EDGE,"E254");var subQ18=sQuery(id+"F0.wireOp",EDGE,"E253");var subQ19=sQuery(id+"F0.wireOp",EDGE,"E252");var subQ20=sQuery(id+"F0.wireOp",EDGE,"E251");var subQ21=sQuery(id+"F0.wireOp",EDGE,"E250");var subQ22=sQuery(id+"F0.wireOp",EDGE,"E249");var subQ23=sQuery(id+"F0.wireOp",EDGE,"E248");var subQ24=sQuery(id+"F0.wireOp",EDGE,"E247");var subQ25=sQuery(id+"F0.wireOp",EDGE,"E246");var subQ26=sQuery(id+"F0.wireOp",EDGE,"E245");var subQ27=sQuery(id+"F0.wireOp",EDGE,"E244");var subQ28=sQuery(id+"F0.wireOp",EDGE,"E243");var subQ29=sQuery(id+"F0.wireOp",EDGE,"E242");var subQ30=sQuery(id+"F0.wireOp",EDGE,"E127");var subQ31=sQuery(id+"F0.wireOp",EDGE,"E126");var subQ32=sQuery(id+"F0.wireOp",EDGE,"E125");var subQ33=sQuery(id+"F0.wireOp",EDGE,"E124");var subQ34=sQuery(id+"F0.wireOp",EDGE,"E123");var subQ35=sQuery(id+"F0.wireOp",EDGE,"E122");var subQ36=sQuery(id+"F0.wireOp",EDGE,"E121");var subQ37=sQuery(id+"F0.wireOp",EDGE,"E120");var subQ38=sQuery(id+"F0.wireOp",EDGE,"E56");var subQ39=sQuery(id+"F0.wireOp",EDGE,"E55");var subQ40=sQuery(id+"F0.wireOp",EDGE,"E54");var subQ41=sQuery(id+"F0.wireOp",EDGE,"E53");var subQ42=sQuery(id+"F0.wireOp",EDGE,"E52");var subQ43=sQuery(id+"F0.wireOp",EDGE,"E51");var subQ44=sQuery(id+"F0.wireOp",EDGE,"E50");var subQ45=sQuery(id+"F0.wireOp",EDGE,"E49");var subQ46=sQuery(id+"F0.wireOp",EDGE,"E48");var subQ47=sQuery(id+"F0.wireOp",EDGE,"E47");var subQ48=sQuery(id+"F0.wireOp",EDGE,"E46");Q12=makeQuery(id+"F3.opExtrude","SWEPT_BODY",BODY,{"disambiguationData":[OSD([subQ48,subQ47,subQ46,subQ45,subQ44,subQ43,subQ42,subQ41,subQ40,subQ39,subQ38,subQ37,subQ36,subQ35,subQ34,subQ33,subQ32,subQ31,subQ30,subQ29,subQ28,subQ27,subQ26,subQ25,subQ24,subQ23,subQ22,subQ21,subQ20,subQ19,subQ18,subQ17,subQ16,subQ15,subQ14,subQ13,subQ12,subQ11,subQ10,subQ9,subQ8,subQ7,subQ6,subQ5,subQ4,subQ3,subQ2,subQ1,subQ0]),TDD([makeQuery(id+"F2.boolean.opBoolean","SPLIT",FACE,{"disambiguationData":[TD([makeQuery(id+"F2.opExtrude","SWEPT_FACE",FACE,{"disambiguationData":[OSD([sQuery(id+"F0.wireOp",EDGE,"E193")])]})])],"derivedFrom":makeQuery(id+"F1.opExtrude","CAP_FACE",FACE,{"disambiguationData":[OSD([subQ48,subQ47,subQ46,subQ45,subQ44,subQ43,subQ42,subQ41,subQ40,subQ39,subQ38,subQ37,subQ36,subQ35,subQ34,subQ33,subQ32,subQ31,subQ30,subQ29,subQ28,subQ27,subQ26,subQ25,subQ24,subQ23,subQ22,subQ21,subQ20,subQ19,subQ18,subQ17,subQ16,subQ15,subQ14,subQ13,subQ12,subQ11,subQ10,subQ9,subQ8,subQ7,subQ6,subQ5,subQ4,subQ3,subQ2,subQ1,subQ0])],"isStart":false})})])]});}
            var Q13;
            {var subQ0=sQuery(id+"F0.wireOp",EDGE,"E127");var subQ1=sQuery(id+"F0.wireOp",EDGE,"E126");var subQ2=sQuery(id+"F0.wireOp",EDGE,"E125");var subQ3=sQuery(id+"F0.wireOp",EDGE,"E124");var subQ4=sQuery(id+"F0.wireOp",EDGE,"E123");var subQ5=sQuery(id+"F0.wireOp",EDGE,"E120");var subQ6=sQuery(id+"F0.wireOp",EDGE,"E56");var subQ7=sQuery(id+"F0.wireOp",EDGE,"E55");var subQ8=sQuery(id+"F0.wireOp",EDGE,"E54");var subQ9=sQuery(id+"F0.wireOp",EDGE,"E53");var subQ10=sQuery(id+"F0.wireOp",EDGE,"E52");var subQ11=sQuery(id+"F0.wireOp",EDGE,"E51");var subQ12=sQuery(id+"F0.wireOp",EDGE,"E50");var subQ13=sQuery(id+"F0.wireOp",EDGE,"E49");var subQ14=sQuery(id+"F0.wireOp",EDGE,"E48");var subQ15=sQuery(id+"F0.wireOp",EDGE,"E47");var subQ16=sQuery(id+"F0.wireOp",EDGE,"E122");var subQ17=sQuery(id+"F0.wireOp",EDGE,"E121");var subQ18=sQuery(id+"F0.wireOp",EDGE,"E46");var subQ19=sQuery(id+"F0.wireOp",EDGE,"E271");var subQ20=sQuery(id+"F0.wireOp",EDGE,"E270");var subQ21=sQuery(id+"F0.wireOp",EDGE,"E269");var subQ22=sQuery(id+"F0.wireOp",EDGE,"E268");var subQ23=sQuery(id+"F0.wireOp",EDGE,"E267");var subQ24=sQuery(id+"F0.wireOp",EDGE,"E266");var subQ25=sQuery(id+"F0.wireOp",EDGE,"E265");var subQ26=sQuery(id+"F0.wireOp",EDGE,"E264");var subQ27=sQuery(id+"F0.wireOp",EDGE,"E263");var subQ28=sQuery(id+"F0.wireOp",EDGE,"E262");var subQ29=sQuery(id+"F0.wireOp",EDGE,"E261");var subQ30=sQuery(id+"F0.wireOp",EDGE,"E260");var subQ31=sQuery(id+"F0.wireOp",EDGE,"E259");var subQ32=sQuery(id+"F0.wireOp",EDGE,"E258");var subQ33=sQuery(id+"F0.wireOp",EDGE,"E257");var subQ34=sQuery(id+"F0.wireOp",EDGE,"E256");var subQ35=sQuery(id+"F0.wireOp",EDGE,"E255");var subQ36=sQuery(id+"F0.wireOp",EDGE,"E254");var subQ37=sQuery(id+"F0.wireOp",EDGE,"E253");var subQ38=sQuery(id+"F0.wireOp",EDGE,"E252");var subQ39=sQuery(id+"F0.wireOp",EDGE,"E251");var subQ40=sQuery(id+"F0.wireOp",EDGE,"E250");var subQ41=sQuery(id+"F0.wireOp",EDGE,"E249");var subQ42=sQuery(id+"F0.wireOp",EDGE,"E248");var subQ43=sQuery(id+"F0.wireOp",EDGE,"E247");var subQ44=sQuery(id+"F0.wireOp",EDGE,"E246");var subQ45=sQuery(id+"F0.wireOp",EDGE,"E245");var subQ46=sQuery(id+"F0.wireOp",EDGE,"E244");var subQ47=sQuery(id+"F0.wireOp",EDGE,"E243");var subQ48=sQuery(id+"F0.wireOp",EDGE,"E242");Q13=makeQuery(id+"F3.opExtrude","SWEPT_BODY",BODY,{"disambiguationData":[OSD([subQ18,subQ15,subQ14,subQ13,subQ12,subQ11,subQ10,subQ9,subQ8,subQ7,subQ6,subQ5,subQ17,subQ16,subQ4,subQ3,subQ2,subQ1,subQ0,subQ48,subQ47,subQ46,subQ45,subQ44,subQ43,subQ42,subQ41,subQ40,subQ39,subQ38,subQ37,subQ36,subQ35,subQ34,subQ33,subQ32,subQ31,subQ30,subQ29,subQ28,subQ27,subQ26,subQ25,subQ24,subQ23,subQ22,subQ21,subQ20,subQ19]),TDD([makeQuery(id+"F2.boolean.opBoolean","SPLIT",FACE,{"disambiguationData":[TD([makeQuery(id+"F1.opExtrude","SWEPT_FACE",FACE,{"disambiguationData":[OSD([subQ18])]})])],"derivedFrom":makeQuery(id+"F1.opExtrude","CAP_FACE",FACE,{"disambiguationData":[OSD([subQ18,subQ15,subQ14,subQ13,subQ12,subQ11,subQ10,subQ9,subQ8,subQ7,subQ6,subQ5,subQ17,subQ16,subQ4,subQ3,subQ2,subQ1,subQ0,subQ48,subQ47,subQ46,subQ45,subQ44,subQ43,subQ42,subQ41,subQ40,subQ39,subQ38,subQ37,subQ36,subQ35,subQ34,subQ33,subQ32,subQ31,subQ30,subQ29,subQ28,subQ27,subQ26,subQ25,subQ24,subQ23,subQ22,subQ21,subQ20,subQ19])],"isStart":false})})])]});}
            var Q14;
            Q14=qCreatedBy(makeId("Origin.pointOp"),VERTEX);
            transform(context, id + "F4", {"entities" : qUnion([Q0, Q1, Q2, Q3, Q4, Q5, Q6, Q7, Q8, Q9, Q10, Q11, Q12, Q13]), "transformType" : TransformType.SCALE_UNIFORMLY, "scale" : 2.2, "scalePoint" : qUnion([Q14]), "makeCopy" : false});
        }
        {
            var Q0;
            Q0=qCreatedBy(makeId("Front.planeOp"),FACE);
            var sketch = newSketch(context, id + "F5", { "sketchPlane" : qUnion([Q0])});
            skLineSegment(sketch, "E273", {"start": v(0, 0) * mm, "end": v(0, 31.23) * mm});
            skSolve(sketch);
        }
        {
            var Q0;
            {var subQ0=sQuery(id+"F0.wireOp",EDGE,"E271");var subQ1=sQuery(id+"F0.wireOp",EDGE,"E270");var subQ2=sQuery(id+"F0.wireOp",EDGE,"E269");var subQ3=sQuery(id+"F0.wireOp",EDGE,"E268");var subQ4=sQuery(id+"F0.wireOp",EDGE,"E267");var subQ5=sQuery(id+"F0.wireOp",EDGE,"E266");var subQ6=sQuery(id+"F0.wireOp",EDGE,"E265");var subQ7=sQuery(id+"F0.wireOp",EDGE,"E264");var subQ8=sQuery(id+"F0.wireOp",EDGE,"E263");var subQ9=sQuery(id+"F0.wireOp",EDGE,"E262");var subQ10=sQuery(id+"F0.wireOp",EDGE,"E261");var subQ11=sQuery(id+"F0.wireOp",EDGE,"E260");var subQ12=sQuery(id+"F0.wireOp",EDGE,"E259");var subQ13=sQuery(id+"F0.wireOp",EDGE,"E258");var subQ14=sQuery(id+"F0.wireOp",EDGE,"E257");var subQ15=sQuery(id+"F0.wireOp",EDGE,"E256");var subQ16=sQuery(id+"F0.wireOp",EDGE,"E255");var subQ17=sQuery(id+"F0.wireOp",EDGE,"E254");var subQ18=sQuery(id+"F0.wireOp",EDGE,"E253");var subQ19=sQuery(id+"F0.wireOp",EDGE,"E252");var subQ20=sQuery(id+"F0.wireOp",EDGE,"E251");var subQ21=sQuery(id+"F0.wireOp",EDGE,"E250");var subQ22=sQuery(id+"F0.wireOp",EDGE,"E249");var subQ23=sQuery(id+"F0.wireOp",EDGE,"E248");var subQ24=sQuery(id+"F0.wireOp",EDGE,"E247");var subQ25=sQuery(id+"F0.wireOp",EDGE,"E246");var subQ26=sQuery(id+"F0.wireOp",EDGE,"E245");var subQ27=sQuery(id+"F0.wireOp",EDGE,"E244");var subQ28=sQuery(id+"F0.wireOp",EDGE,"E243");var subQ29=sQuery(id+"F0.wireOp",EDGE,"E242");var subQ30=sQuery(id+"F0.wireOp",EDGE,"E127");var subQ31=sQuery(id+"F0.wireOp",EDGE,"E126");var subQ32=sQuery(id+"F0.wireOp",EDGE,"E125");var subQ33=sQuery(id+"F0.wireOp",EDGE,"E124");var subQ34=sQuery(id+"F0.wireOp",EDGE,"E123");var subQ35=sQuery(id+"F0.wireOp",EDGE,"E122");var subQ36=sQuery(id+"F0.wireOp",EDGE,"E121");var subQ37=sQuery(id+"F0.wireOp",EDGE,"E120");var subQ38=sQuery(id+"F0.wireOp",EDGE,"E56");var subQ39=sQuery(id+"F0.wireOp",EDGE,"E55");var subQ40=sQuery(id+"F0.wireOp",EDGE,"E54");var subQ41=sQuery(id+"F0.wireOp",EDGE,"E53");var subQ42=sQuery(id+"F0.wireOp",EDGE,"E52");var subQ43=sQuery(id+"F0.wireOp",EDGE,"E51");var subQ44=sQuery(id+"F0.wireOp",EDGE,"E50");var subQ45=sQuery(id+"F0.wireOp",EDGE,"E49");var subQ46=sQuery(id+"F0.wireOp",EDGE,"E48");var subQ47=sQuery(id+"F0.wireOp",EDGE,"E47");var subQ48=sQuery(id+"F0.wireOp",EDGE,"E46");Q0=makeQuery(id+"F3.opExtrude","SWEPT_BODY",BODY,{"disambiguationData":[OSD([subQ48,subQ47,subQ46,subQ45,subQ44,subQ43,subQ42,subQ41,subQ40,subQ39,subQ38,subQ37,subQ36,subQ35,subQ34,subQ33,subQ32,subQ31,subQ30,subQ29,subQ28,subQ27,subQ26,subQ25,subQ24,subQ23,subQ22,subQ21,subQ20,subQ19,subQ18,subQ17,subQ16,subQ15,subQ14,subQ13,subQ12,subQ11,subQ10,subQ9,subQ8,subQ7,subQ6,subQ5,subQ4,subQ3,subQ2,subQ1,subQ0]),TDD([makeQuery(id+"F2.boolean.opBoolean","SPLIT",FACE,{"disambiguationData":[TD([makeQuery(id+"F2.opExtrude","SWEPT_FACE",FACE,{"disambiguationData":[OSD([sQuery(id+"F0.wireOp",EDGE,"E200")])]})])],"derivedFrom":makeQuery(id+"F1.opExtrude","CAP_FACE",FACE,{"disambiguationData":[OSD([subQ48,subQ47,subQ46,subQ45,subQ44,subQ43,subQ42,subQ41,subQ40,subQ39,subQ38,subQ37,subQ36,subQ35,subQ34,subQ33,subQ32,subQ31,subQ30,subQ29,subQ28,subQ27,subQ26,subQ25,subQ24,subQ23,subQ22,subQ21,subQ20,subQ19,subQ18,subQ17,subQ16,subQ15,subQ14,subQ13,subQ12,subQ11,subQ10,subQ9,subQ8,subQ7,subQ6,subQ5,subQ4,subQ3,subQ2,subQ1,subQ0])],"isStart":false})})])]});}
            var Q1;
            {var subQ0=sQuery(id+"F0.wireOp",EDGE,"E271");var subQ1=sQuery(id+"F0.wireOp",EDGE,"E270");var subQ2=sQuery(id+"F0.wireOp",EDGE,"E269");var subQ3=sQuery(id+"F0.wireOp",EDGE,"E268");var subQ4=sQuery(id+"F0.wireOp",EDGE,"E267");var subQ5=sQuery(id+"F0.wireOp",EDGE,"E266");var subQ6=sQuery(id+"F0.wireOp",EDGE,"E265");var subQ7=sQuery(id+"F0.wireOp",EDGE,"E264");var subQ8=sQuery(id+"F0.wireOp",EDGE,"E263");var subQ9=sQuery(id+"F0.wireOp",EDGE,"E262");var subQ10=sQuery(id+"F0.wireOp",EDGE,"E261");var subQ11=sQuery(id+"F0.wireOp",EDGE,"E260");var subQ12=sQuery(id+"F0.wireOp",EDGE,"E259");var subQ13=sQuery(id+"F0.wireOp",EDGE,"E258");var subQ14=sQuery(id+"F0.wireOp",EDGE,"E257");var subQ15=sQuery(id+"F0.wireOp",EDGE,"E256");var subQ16=sQuery(id+"F0.wireOp",EDGE,"E255");var subQ17=sQuery(id+"F0.wireOp",EDGE,"E254");var subQ18=sQuery(id+"F0.wireOp",EDGE,"E253");var subQ19=sQuery(id+"F0.wireOp",EDGE,"E252");var subQ20=sQuery(id+"F0.wireOp",EDGE,"E251");var subQ21=sQuery(id+"F0.wireOp",EDGE,"E250");var subQ22=sQuery(id+"F0.wireOp",EDGE,"E249");var subQ23=sQuery(id+"F0.wireOp",EDGE,"E248");var subQ24=sQuery(id+"F0.wireOp",EDGE,"E247");var subQ25=sQuery(id+"F0.wireOp",EDGE,"E246");var subQ26=sQuery(id+"F0.wireOp",EDGE,"E245");var subQ27=sQuery(id+"F0.wireOp",EDGE,"E244");var subQ28=sQuery(id+"F0.wireOp",EDGE,"E243");var subQ29=sQuery(id+"F0.wireOp",EDGE,"E242");var subQ30=sQuery(id+"F0.wireOp",EDGE,"E127");var subQ31=sQuery(id+"F0.wireOp",EDGE,"E126");var subQ32=sQuery(id+"F0.wireOp",EDGE,"E125");var subQ33=sQuery(id+"F0.wireOp",EDGE,"E124");var subQ34=sQuery(id+"F0.wireOp",EDGE,"E123");var subQ35=sQuery(id+"F0.wireOp",EDGE,"E122");var subQ36=sQuery(id+"F0.wireOp",EDGE,"E121");var subQ37=sQuery(id+"F0.wireOp",EDGE,"E120");var subQ38=sQuery(id+"F0.wireOp",EDGE,"E56");var subQ39=sQuery(id+"F0.wireOp",EDGE,"E55");var subQ40=sQuery(id+"F0.wireOp",EDGE,"E54");var subQ41=sQuery(id+"F0.wireOp",EDGE,"E53");var subQ42=sQuery(id+"F0.wireOp",EDGE,"E52");var subQ43=sQuery(id+"F0.wireOp",EDGE,"E51");var subQ44=sQuery(id+"F0.wireOp",EDGE,"E50");var subQ45=sQuery(id+"F0.wireOp",EDGE,"E49");var subQ46=sQuery(id+"F0.wireOp",EDGE,"E48");var subQ47=sQuery(id+"F0.wireOp",EDGE,"E47");var subQ48=sQuery(id+"F0.wireOp",EDGE,"E46");Q1=makeQuery(id+"F3.opExtrude","SWEPT_BODY",BODY,{"disambiguationData":[OSD([subQ48,subQ47,subQ46,subQ45,subQ44,subQ43,subQ42,subQ41,subQ40,subQ39,subQ38,subQ37,subQ36,subQ35,subQ34,subQ33,subQ32,subQ31,subQ30,subQ29,subQ28,subQ27,subQ26,subQ25,subQ24,subQ23,subQ22,subQ21,subQ20,subQ19,subQ18,subQ17,subQ16,subQ15,subQ14,subQ13,subQ12,subQ11,subQ10,subQ9,subQ8,subQ7,subQ6,subQ5,subQ4,subQ3,subQ2,subQ1,subQ0]),TDD([makeQuery(id+"F2.boolean.opBoolean","SPLIT",FACE,{"disambiguationData":[TD([makeQuery(id+"F2.opExtrude","SWEPT_FACE",FACE,{"disambiguationData":[OSD([sQuery(id+"F0.wireOp",EDGE,"E82")])]})])],"derivedFrom":makeQuery(id+"F1.opExtrude","CAP_FACE",FACE,{"disambiguationData":[OSD([subQ48,subQ47,subQ46,subQ45,subQ44,subQ43,subQ42,subQ41,subQ40,subQ39,subQ38,subQ37,subQ36,subQ35,subQ34,subQ33,subQ32,subQ31,subQ30,subQ29,subQ28,subQ27,subQ26,subQ25,subQ24,subQ23,subQ22,subQ21,subQ20,subQ19,subQ18,subQ17,subQ16,subQ15,subQ14,subQ13,subQ12,subQ11,subQ10,subQ9,subQ8,subQ7,subQ6,subQ5,subQ4,subQ3,subQ2,subQ1,subQ0])],"isStart":false})})])]});}
            var Q2;
            {var subQ0=sQuery(id+"F0.wireOp",EDGE,"E271");var subQ1=sQuery(id+"F0.wireOp",EDGE,"E270");var subQ2=sQuery(id+"F0.wireOp",EDGE,"E269");var subQ3=sQuery(id+"F0.wireOp",EDGE,"E268");var subQ4=sQuery(id+"F0.wireOp",EDGE,"E267");var subQ5=sQuery(id+"F0.wireOp",EDGE,"E266");var subQ6=sQuery(id+"F0.wireOp",EDGE,"E265");var subQ7=sQuery(id+"F0.wireOp",EDGE,"E264");var subQ8=sQuery(id+"F0.wireOp",EDGE,"E263");var subQ9=sQuery(id+"F0.wireOp",EDGE,"E262");var subQ10=sQuery(id+"F0.wireOp",EDGE,"E261");var subQ11=sQuery(id+"F0.wireOp",EDGE,"E260");var subQ12=sQuery(id+"F0.wireOp",EDGE,"E259");var subQ13=sQuery(id+"F0.wireOp",EDGE,"E258");var subQ14=sQuery(id+"F0.wireOp",EDGE,"E257");var subQ15=sQuery(id+"F0.wireOp",EDGE,"E256");var subQ16=sQuery(id+"F0.wireOp",EDGE,"E255");var subQ17=sQuery(id+"F0.wireOp",EDGE,"E254");var subQ18=sQuery(id+"F0.wireOp",EDGE,"E253");var subQ19=sQuery(id+"F0.wireOp",EDGE,"E252");var subQ20=sQuery(id+"F0.wireOp",EDGE,"E251");var subQ21=sQuery(id+"F0.wireOp",EDGE,"E250");var subQ22=sQuery(id+"F0.wireOp",EDGE,"E249");var subQ23=sQuery(id+"F0.wireOp",EDGE,"E248");var subQ24=sQuery(id+"F0.wireOp",EDGE,"E247");var subQ25=sQuery(id+"F0.wireOp",EDGE,"E246");var subQ26=sQuery(id+"F0.wireOp",EDGE,"E245");var subQ27=sQuery(id+"F0.wireOp",EDGE,"E244");var subQ28=sQuery(id+"F0.wireOp",EDGE,"E243");var subQ29=sQuery(id+"F0.wireOp",EDGE,"E242");var subQ30=sQuery(id+"F0.wireOp",EDGE,"E127");var subQ31=sQuery(id+"F0.wireOp",EDGE,"E126");var subQ32=sQuery(id+"F0.wireOp",EDGE,"E125");var subQ33=sQuery(id+"F0.wireOp",EDGE,"E124");var subQ34=sQuery(id+"F0.wireOp",EDGE,"E123");var subQ35=sQuery(id+"F0.wireOp",EDGE,"E122");var subQ36=sQuery(id+"F0.wireOp",EDGE,"E121");var subQ37=sQuery(id+"F0.wireOp",EDGE,"E120");var subQ38=sQuery(id+"F0.wireOp",EDGE,"E56");var subQ39=sQuery(id+"F0.wireOp",EDGE,"E55");var subQ40=sQuery(id+"F0.wireOp",EDGE,"E54");var subQ41=sQuery(id+"F0.wireOp",EDGE,"E53");var subQ42=sQuery(id+"F0.wireOp",EDGE,"E52");var subQ43=sQuery(id+"F0.wireOp",EDGE,"E51");var subQ44=sQuery(id+"F0.wireOp",EDGE,"E50");var subQ45=sQuery(id+"F0.wireOp",EDGE,"E49");var subQ46=sQuery(id+"F0.wireOp",EDGE,"E48");var subQ47=sQuery(id+"F0.wireOp",EDGE,"E47");var subQ48=sQuery(id+"F0.wireOp",EDGE,"E46");Q2=makeQuery(id+"F3.opExtrude","SWEPT_BODY",BODY,{"disambiguationData":[OSD([subQ48,subQ47,subQ46,subQ45,subQ44,subQ43,subQ42,subQ41,subQ40,subQ39,subQ38,subQ37,subQ36,subQ35,subQ34,subQ33,subQ32,subQ31,subQ30,subQ29,subQ28,subQ27,subQ26,subQ25,subQ24,subQ23,subQ22,subQ21,subQ20,subQ19,subQ18,subQ17,subQ16,subQ15,subQ14,subQ13,subQ12,subQ11,subQ10,subQ9,subQ8,subQ7,subQ6,subQ5,subQ4,subQ3,subQ2,subQ1,subQ0]),TDD([makeQuery(id+"F2.boolean.opBoolean","SPLIT",FACE,{"disambiguationData":[TD([makeQuery(id+"F2.opExtrude","SWEPT_FACE",FACE,{"disambiguationData":[OSD([sQuery(id+"F0.wireOp",EDGE,"E207")])]})])],"derivedFrom":makeQuery(id+"F1.opExtrude","CAP_FACE",FACE,{"disambiguationData":[OSD([subQ48,subQ47,subQ46,subQ45,subQ44,subQ43,subQ42,subQ41,subQ40,subQ39,subQ38,subQ37,subQ36,subQ35,subQ34,subQ33,subQ32,subQ31,subQ30,subQ29,subQ28,subQ27,subQ26,subQ25,subQ24,subQ23,subQ22,subQ21,subQ20,subQ19,subQ18,subQ17,subQ16,subQ15,subQ14,subQ13,subQ12,subQ11,subQ10,subQ9,subQ8,subQ7,subQ6,subQ5,subQ4,subQ3,subQ2,subQ1,subQ0])],"isStart":false})})])]});}
            var Q3;
            Q3=makeQuery(id+"F1.opExtrude","SWEPT_BODY",BODY,{"disambiguationData":[OSD([sQuery(id+"F0.wireOp",EDGE,"E46"),sQuery(id+"F0.wireOp",EDGE,"E47"),sQuery(id+"F0.wireOp",EDGE,"E48"),sQuery(id+"F0.wireOp",EDGE,"E49"),sQuery(id+"F0.wireOp",EDGE,"E50"),sQuery(id+"F0.wireOp",EDGE,"E51"),sQuery(id+"F0.wireOp",EDGE,"E52"),sQuery(id+"F0.wireOp",EDGE,"E53"),sQuery(id+"F0.wireOp",EDGE,"E54"),sQuery(id+"F0.wireOp",EDGE,"E55"),sQuery(id+"F0.wireOp",EDGE,"E56"),sQuery(id+"F0.wireOp",EDGE,"E120"),sQuery(id+"F0.wireOp",EDGE,"E121"),sQuery(id+"F0.wireOp",EDGE,"E122"),sQuery(id+"F0.wireOp",EDGE,"E123"),sQuery(id+"F0.wireOp",EDGE,"E124"),sQuery(id+"F0.wireOp",EDGE,"E125"),sQuery(id+"F0.wireOp",EDGE,"E126"),sQuery(id+"F0.wireOp",EDGE,"E127"),sQuery(id+"F0.wireOp",EDGE,"E242"),sQuery(id+"F0.wireOp",EDGE,"E243"),sQuery(id+"F0.wireOp",EDGE,"E244"),sQuery(id+"F0.wireOp",EDGE,"E245"),sQuery(id+"F0.wireOp",EDGE,"E246"),sQuery(id+"F0.wireOp",EDGE,"E247"),sQuery(id+"F0.wireOp",EDGE,"E248"),sQuery(id+"F0.wireOp",EDGE,"E249"),sQuery(id+"F0.wireOp",EDGE,"E250"),sQuery(id+"F0.wireOp",EDGE,"E251"),sQuery(id+"F0.wireOp",EDGE,"E252"),sQuery(id+"F0.wireOp",EDGE,"E253"),sQuery(id+"F0.wireOp",EDGE,"E254"),sQuery(id+"F0.wireOp",EDGE,"E255"),sQuery(id+"F0.wireOp",EDGE,"E256"),sQuery(id+"F0.wireOp",EDGE,"E257"),sQuery(id+"F0.wireOp",EDGE,"E258"),sQuery(id+"F0.wireOp",EDGE,"E259"),sQuery(id+"F0.wireOp",EDGE,"E260"),sQuery(id+"F0.wireOp",EDGE,"E261"),sQuery(id+"F0.wireOp",EDGE,"E262"),sQuery(id+"F0.wireOp",EDGE,"E263"),sQuery(id+"F0.wireOp",EDGE,"E264"),sQuery(id+"F0.wireOp",EDGE,"E265"),sQuery(id+"F0.wireOp",EDGE,"E266"),sQuery(id+"F0.wireOp",EDGE,"E267"),sQuery(id+"F0.wireOp",EDGE,"E268"),sQuery(id+"F0.wireOp",EDGE,"E269"),sQuery(id+"F0.wireOp",EDGE,"E270"),sQuery(id+"F0.wireOp",EDGE,"E271")])]});
            var Q4;
            {var subQ0=sQuery(id+"F0.wireOp",EDGE,"E271");var subQ1=sQuery(id+"F0.wireOp",EDGE,"E270");var subQ2=sQuery(id+"F0.wireOp",EDGE,"E269");var subQ3=sQuery(id+"F0.wireOp",EDGE,"E268");var subQ4=sQuery(id+"F0.wireOp",EDGE,"E267");var subQ5=sQuery(id+"F0.wireOp",EDGE,"E266");var subQ6=sQuery(id+"F0.wireOp",EDGE,"E265");var subQ7=sQuery(id+"F0.wireOp",EDGE,"E264");var subQ8=sQuery(id+"F0.wireOp",EDGE,"E263");var subQ9=sQuery(id+"F0.wireOp",EDGE,"E262");var subQ10=sQuery(id+"F0.wireOp",EDGE,"E261");var subQ11=sQuery(id+"F0.wireOp",EDGE,"E260");var subQ12=sQuery(id+"F0.wireOp",EDGE,"E259");var subQ13=sQuery(id+"F0.wireOp",EDGE,"E258");var subQ14=sQuery(id+"F0.wireOp",EDGE,"E257");var subQ15=sQuery(id+"F0.wireOp",EDGE,"E256");var subQ16=sQuery(id+"F0.wireOp",EDGE,"E255");var subQ17=sQuery(id+"F0.wireOp",EDGE,"E254");var subQ18=sQuery(id+"F0.wireOp",EDGE,"E253");var subQ19=sQuery(id+"F0.wireOp",EDGE,"E252");var subQ20=sQuery(id+"F0.wireOp",EDGE,"E251");var subQ21=sQuery(id+"F0.wireOp",EDGE,"E250");var subQ22=sQuery(id+"F0.wireOp",EDGE,"E249");var subQ23=sQuery(id+"F0.wireOp",EDGE,"E248");var subQ24=sQuery(id+"F0.wireOp",EDGE,"E247");var subQ25=sQuery(id+"F0.wireOp",EDGE,"E246");var subQ26=sQuery(id+"F0.wireOp",EDGE,"E245");var subQ27=sQuery(id+"F0.wireOp",EDGE,"E244");var subQ28=sQuery(id+"F0.wireOp",EDGE,"E243");var subQ29=sQuery(id+"F0.wireOp",EDGE,"E242");var subQ30=sQuery(id+"F0.wireOp",EDGE,"E127");var subQ31=sQuery(id+"F0.wireOp",EDGE,"E126");var subQ32=sQuery(id+"F0.wireOp",EDGE,"E125");var subQ33=sQuery(id+"F0.wireOp",EDGE,"E124");var subQ34=sQuery(id+"F0.wireOp",EDGE,"E123");var subQ35=sQuery(id+"F0.wireOp",EDGE,"E122");var subQ36=sQuery(id+"F0.wireOp",EDGE,"E121");var subQ37=sQuery(id+"F0.wireOp",EDGE,"E120");var subQ38=sQuery(id+"F0.wireOp",EDGE,"E56");var subQ39=sQuery(id+"F0.wireOp",EDGE,"E55");var subQ40=sQuery(id+"F0.wireOp",EDGE,"E54");var subQ41=sQuery(id+"F0.wireOp",EDGE,"E53");var subQ42=sQuery(id+"F0.wireOp",EDGE,"E52");var subQ43=sQuery(id+"F0.wireOp",EDGE,"E51");var subQ44=sQuery(id+"F0.wireOp",EDGE,"E50");var subQ45=sQuery(id+"F0.wireOp",EDGE,"E49");var subQ46=sQuery(id+"F0.wireOp",EDGE,"E48");var subQ47=sQuery(id+"F0.wireOp",EDGE,"E47");var subQ48=sQuery(id+"F0.wireOp",EDGE,"E46");Q4=makeQuery(id+"F3.opExtrude","SWEPT_BODY",BODY,{"disambiguationData":[OSD([subQ48,subQ47,subQ46,subQ45,subQ44,subQ43,subQ42,subQ41,subQ40,subQ39,subQ38,subQ37,subQ36,subQ35,subQ34,subQ33,subQ32,subQ31,subQ30,subQ29,subQ28,subQ27,subQ26,subQ25,subQ24,subQ23,subQ22,subQ21,subQ20,subQ19,subQ18,subQ17,subQ16,subQ15,subQ14,subQ13,subQ12,subQ11,subQ10,subQ9,subQ8,subQ7,subQ6,subQ5,subQ4,subQ3,subQ2,subQ1,subQ0]),TDD([makeQuery(id+"F2.boolean.opBoolean","SPLIT",FACE,{"disambiguationData":[TD([makeQuery(id+"F2.opExtrude","SWEPT_FACE",FACE,{"disambiguationData":[OSD([sQuery(id+"F0.wireOp",EDGE,"E85")])]})])],"derivedFrom":makeQuery(id+"F1.opExtrude","CAP_FACE",FACE,{"disambiguationData":[OSD([subQ48,subQ47,subQ46,subQ45,subQ44,subQ43,subQ42,subQ41,subQ40,subQ39,subQ38,subQ37,subQ36,subQ35,subQ34,subQ33,subQ32,subQ31,subQ30,subQ29,subQ28,subQ27,subQ26,subQ25,subQ24,subQ23,subQ22,subQ21,subQ20,subQ19,subQ18,subQ17,subQ16,subQ15,subQ14,subQ13,subQ12,subQ11,subQ10,subQ9,subQ8,subQ7,subQ6,subQ5,subQ4,subQ3,subQ2,subQ1,subQ0])],"isStart":false})})])]});}
            var Q5;
            {var subQ0=sQuery(id+"F0.wireOp",EDGE,"E271");var subQ1=sQuery(id+"F0.wireOp",EDGE,"E270");var subQ2=sQuery(id+"F0.wireOp",EDGE,"E269");var subQ3=sQuery(id+"F0.wireOp",EDGE,"E268");var subQ4=sQuery(id+"F0.wireOp",EDGE,"E267");var subQ5=sQuery(id+"F0.wireOp",EDGE,"E266");var subQ6=sQuery(id+"F0.wireOp",EDGE,"E265");var subQ7=sQuery(id+"F0.wireOp",EDGE,"E264");var subQ8=sQuery(id+"F0.wireOp",EDGE,"E263");var subQ9=sQuery(id+"F0.wireOp",EDGE,"E262");var subQ10=sQuery(id+"F0.wireOp",EDGE,"E261");var subQ11=sQuery(id+"F0.wireOp",EDGE,"E260");var subQ12=sQuery(id+"F0.wireOp",EDGE,"E259");var subQ13=sQuery(id+"F0.wireOp",EDGE,"E258");var subQ14=sQuery(id+"F0.wireOp",EDGE,"E257");var subQ15=sQuery(id+"F0.wireOp",EDGE,"E256");var subQ16=sQuery(id+"F0.wireOp",EDGE,"E255");var subQ17=sQuery(id+"F0.wireOp",EDGE,"E254");var subQ18=sQuery(id+"F0.wireOp",EDGE,"E253");var subQ19=sQuery(id+"F0.wireOp",EDGE,"E252");var subQ20=sQuery(id+"F0.wireOp",EDGE,"E251");var subQ21=sQuery(id+"F0.wireOp",EDGE,"E250");var subQ22=sQuery(id+"F0.wireOp",EDGE,"E249");var subQ23=sQuery(id+"F0.wireOp",EDGE,"E248");var subQ24=sQuery(id+"F0.wireOp",EDGE,"E247");var subQ25=sQuery(id+"F0.wireOp",EDGE,"E246");var subQ26=sQuery(id+"F0.wireOp",EDGE,"E245");var subQ27=sQuery(id+"F0.wireOp",EDGE,"E244");var subQ28=sQuery(id+"F0.wireOp",EDGE,"E243");var subQ29=sQuery(id+"F0.wireOp",EDGE,"E242");var subQ30=sQuery(id+"F0.wireOp",EDGE,"E127");var subQ31=sQuery(id+"F0.wireOp",EDGE,"E126");var subQ32=sQuery(id+"F0.wireOp",EDGE,"E125");var subQ33=sQuery(id+"F0.wireOp",EDGE,"E124");var subQ34=sQuery(id+"F0.wireOp",EDGE,"E123");var subQ35=sQuery(id+"F0.wireOp",EDGE,"E122");var subQ36=sQuery(id+"F0.wireOp",EDGE,"E121");var subQ37=sQuery(id+"F0.wireOp",EDGE,"E120");var subQ38=sQuery(id+"F0.wireOp",EDGE,"E56");var subQ39=sQuery(id+"F0.wireOp",EDGE,"E55");var subQ40=sQuery(id+"F0.wireOp",EDGE,"E54");var subQ41=sQuery(id+"F0.wireOp",EDGE,"E53");var subQ42=sQuery(id+"F0.wireOp",EDGE,"E52");var subQ43=sQuery(id+"F0.wireOp",EDGE,"E51");var subQ44=sQuery(id+"F0.wireOp",EDGE,"E50");var subQ45=sQuery(id+"F0.wireOp",EDGE,"E49");var subQ46=sQuery(id+"F0.wireOp",EDGE,"E48");var subQ47=sQuery(id+"F0.wireOp",EDGE,"E47");var subQ48=sQuery(id+"F0.wireOp",EDGE,"E46");Q5=makeQuery(id+"F3.opExtrude","SWEPT_BODY",BODY,{"disambiguationData":[OSD([subQ48,subQ47,subQ46,subQ45,subQ44,subQ43,subQ42,subQ41,subQ40,subQ39,subQ38,subQ37,subQ36,subQ35,subQ34,subQ33,subQ32,subQ31,subQ30,subQ29,subQ28,subQ27,subQ26,subQ25,subQ24,subQ23,subQ22,subQ21,subQ20,subQ19,subQ18,subQ17,subQ16,subQ15,subQ14,subQ13,subQ12,subQ11,subQ10,subQ9,subQ8,subQ7,subQ6,subQ5,subQ4,subQ3,subQ2,subQ1,subQ0]),TDD([makeQuery(id+"F2.boolean.opBoolean","SPLIT",FACE,{"disambiguationData":[TD([makeQuery(id+"F2.opExtrude","SWEPT_FACE",FACE,{"disambiguationData":[OSD([sQuery(id+"F0.wireOp",EDGE,"E88")])]})])],"derivedFrom":makeQuery(id+"F1.opExtrude","CAP_FACE",FACE,{"disambiguationData":[OSD([subQ48,subQ47,subQ46,subQ45,subQ44,subQ43,subQ42,subQ41,subQ40,subQ39,subQ38,subQ37,subQ36,subQ35,subQ34,subQ33,subQ32,subQ31,subQ30,subQ29,subQ28,subQ27,subQ26,subQ25,subQ24,subQ23,subQ22,subQ21,subQ20,subQ19,subQ18,subQ17,subQ16,subQ15,subQ14,subQ13,subQ12,subQ11,subQ10,subQ9,subQ8,subQ7,subQ6,subQ5,subQ4,subQ3,subQ2,subQ1,subQ0])],"isStart":false})})])]});}
            var Q6;
            {var subQ0=sQuery(id+"F0.wireOp",EDGE,"E271");var subQ1=sQuery(id+"F0.wireOp",EDGE,"E270");var subQ2=sQuery(id+"F0.wireOp",EDGE,"E269");var subQ3=sQuery(id+"F0.wireOp",EDGE,"E268");var subQ4=sQuery(id+"F0.wireOp",EDGE,"E267");var subQ5=sQuery(id+"F0.wireOp",EDGE,"E266");var subQ6=sQuery(id+"F0.wireOp",EDGE,"E265");var subQ7=sQuery(id+"F0.wireOp",EDGE,"E264");var subQ8=sQuery(id+"F0.wireOp",EDGE,"E263");var subQ9=sQuery(id+"F0.wireOp",EDGE,"E262");var subQ10=sQuery(id+"F0.wireOp",EDGE,"E261");var subQ11=sQuery(id+"F0.wireOp",EDGE,"E260");var subQ12=sQuery(id+"F0.wireOp",EDGE,"E259");var subQ13=sQuery(id+"F0.wireOp",EDGE,"E258");var subQ14=sQuery(id+"F0.wireOp",EDGE,"E257");var subQ15=sQuery(id+"F0.wireOp",EDGE,"E256");var subQ16=sQuery(id+"F0.wireOp",EDGE,"E255");var subQ17=sQuery(id+"F0.wireOp",EDGE,"E254");var subQ18=sQuery(id+"F0.wireOp",EDGE,"E253");var subQ19=sQuery(id+"F0.wireOp",EDGE,"E252");var subQ20=sQuery(id+"F0.wireOp",EDGE,"E251");var subQ21=sQuery(id+"F0.wireOp",EDGE,"E250");var subQ22=sQuery(id+"F0.wireOp",EDGE,"E249");var subQ23=sQuery(id+"F0.wireOp",EDGE,"E248");var subQ24=sQuery(id+"F0.wireOp",EDGE,"E247");var subQ25=sQuery(id+"F0.wireOp",EDGE,"E246");var subQ26=sQuery(id+"F0.wireOp",EDGE,"E245");var subQ27=sQuery(id+"F0.wireOp",EDGE,"E244");var subQ28=sQuery(id+"F0.wireOp",EDGE,"E243");var subQ29=sQuery(id+"F0.wireOp",EDGE,"E242");var subQ30=sQuery(id+"F0.wireOp",EDGE,"E127");var subQ31=sQuery(id+"F0.wireOp",EDGE,"E126");var subQ32=sQuery(id+"F0.wireOp",EDGE,"E125");var subQ33=sQuery(id+"F0.wireOp",EDGE,"E124");var subQ34=sQuery(id+"F0.wireOp",EDGE,"E123");var subQ35=sQuery(id+"F0.wireOp",EDGE,"E122");var subQ36=sQuery(id+"F0.wireOp",EDGE,"E121");var subQ37=sQuery(id+"F0.wireOp",EDGE,"E120");var subQ38=sQuery(id+"F0.wireOp",EDGE,"E56");var subQ39=sQuery(id+"F0.wireOp",EDGE,"E55");var subQ40=sQuery(id+"F0.wireOp",EDGE,"E54");var subQ41=sQuery(id+"F0.wireOp",EDGE,"E53");var subQ42=sQuery(id+"F0.wireOp",EDGE,"E52");var subQ43=sQuery(id+"F0.wireOp",EDGE,"E51");var subQ44=sQuery(id+"F0.wireOp",EDGE,"E50");var subQ45=sQuery(id+"F0.wireOp",EDGE,"E49");var subQ46=sQuery(id+"F0.wireOp",EDGE,"E48");var subQ47=sQuery(id+"F0.wireOp",EDGE,"E47");var subQ48=sQuery(id+"F0.wireOp",EDGE,"E46");Q6=makeQuery(id+"F3.opExtrude","SWEPT_BODY",BODY,{"disambiguationData":[OSD([subQ48,subQ47,subQ46,subQ45,subQ44,subQ43,subQ42,subQ41,subQ40,subQ39,subQ38,subQ37,subQ36,subQ35,subQ34,subQ33,subQ32,subQ31,subQ30,subQ29,subQ28,subQ27,subQ26,subQ25,subQ24,subQ23,subQ22,subQ21,subQ20,subQ19,subQ18,subQ17,subQ16,subQ15,subQ14,subQ13,subQ12,subQ11,subQ10,subQ9,subQ8,subQ7,subQ6,subQ5,subQ4,subQ3,subQ2,subQ1,subQ0]),TDD([makeQuery(id+"F2.boolean.opBoolean","SPLIT",FACE,{"disambiguationData":[TD([makeQuery(id+"F2.opExtrude","SWEPT_FACE",FACE,{"disambiguationData":[OSD([sQuery(id+"F0.wireOp",EDGE,"E91")])]})])],"derivedFrom":makeQuery(id+"F1.opExtrude","CAP_FACE",FACE,{"disambiguationData":[OSD([subQ48,subQ47,subQ46,subQ45,subQ44,subQ43,subQ42,subQ41,subQ40,subQ39,subQ38,subQ37,subQ36,subQ35,subQ34,subQ33,subQ32,subQ31,subQ30,subQ29,subQ28,subQ27,subQ26,subQ25,subQ24,subQ23,subQ22,subQ21,subQ20,subQ19,subQ18,subQ17,subQ16,subQ15,subQ14,subQ13,subQ12,subQ11,subQ10,subQ9,subQ8,subQ7,subQ6,subQ5,subQ4,subQ3,subQ2,subQ1,subQ0])],"isStart":false})})])]});}
            var Q7;
            {var subQ0=sQuery(id+"F0.wireOp",EDGE,"E271");var subQ1=sQuery(id+"F0.wireOp",EDGE,"E270");var subQ2=sQuery(id+"F0.wireOp",EDGE,"E269");var subQ3=sQuery(id+"F0.wireOp",EDGE,"E268");var subQ4=sQuery(id+"F0.wireOp",EDGE,"E267");var subQ5=sQuery(id+"F0.wireOp",EDGE,"E266");var subQ6=sQuery(id+"F0.wireOp",EDGE,"E265");var subQ7=sQuery(id+"F0.wireOp",EDGE,"E264");var subQ8=sQuery(id+"F0.wireOp",EDGE,"E263");var subQ9=sQuery(id+"F0.wireOp",EDGE,"E262");var subQ10=sQuery(id+"F0.wireOp",EDGE,"E261");var subQ11=sQuery(id+"F0.wireOp",EDGE,"E260");var subQ12=sQuery(id+"F0.wireOp",EDGE,"E259");var subQ13=sQuery(id+"F0.wireOp",EDGE,"E258");var subQ14=sQuery(id+"F0.wireOp",EDGE,"E257");var subQ15=sQuery(id+"F0.wireOp",EDGE,"E256");var subQ16=sQuery(id+"F0.wireOp",EDGE,"E255");var subQ17=sQuery(id+"F0.wireOp",EDGE,"E254");var subQ18=sQuery(id+"F0.wireOp",EDGE,"E253");var subQ19=sQuery(id+"F0.wireOp",EDGE,"E252");var subQ20=sQuery(id+"F0.wireOp",EDGE,"E251");var subQ21=sQuery(id+"F0.wireOp",EDGE,"E250");var subQ22=sQuery(id+"F0.wireOp",EDGE,"E249");var subQ23=sQuery(id+"F0.wireOp",EDGE,"E248");var subQ24=sQuery(id+"F0.wireOp",EDGE,"E247");var subQ25=sQuery(id+"F0.wireOp",EDGE,"E246");var subQ26=sQuery(id+"F0.wireOp",EDGE,"E245");var subQ27=sQuery(id+"F0.wireOp",EDGE,"E244");var subQ28=sQuery(id+"F0.wireOp",EDGE,"E243");var subQ29=sQuery(id+"F0.wireOp",EDGE,"E242");var subQ30=sQuery(id+"F0.wireOp",EDGE,"E127");var subQ31=sQuery(id+"F0.wireOp",EDGE,"E126");var subQ32=sQuery(id+"F0.wireOp",EDGE,"E125");var subQ33=sQuery(id+"F0.wireOp",EDGE,"E124");var subQ34=sQuery(id+"F0.wireOp",EDGE,"E123");var subQ35=sQuery(id+"F0.wireOp",EDGE,"E122");var subQ36=sQuery(id+"F0.wireOp",EDGE,"E121");var subQ37=sQuery(id+"F0.wireOp",EDGE,"E120");var subQ38=sQuery(id+"F0.wireOp",EDGE,"E56");var subQ39=sQuery(id+"F0.wireOp",EDGE,"E55");var subQ40=sQuery(id+"F0.wireOp",EDGE,"E54");var subQ41=sQuery(id+"F0.wireOp",EDGE,"E53");var subQ42=sQuery(id+"F0.wireOp",EDGE,"E52");var subQ43=sQuery(id+"F0.wireOp",EDGE,"E51");var subQ44=sQuery(id+"F0.wireOp",EDGE,"E50");var subQ45=sQuery(id+"F0.wireOp",EDGE,"E49");var subQ46=sQuery(id+"F0.wireOp",EDGE,"E48");var subQ47=sQuery(id+"F0.wireOp",EDGE,"E47");var subQ48=sQuery(id+"F0.wireOp",EDGE,"E46");Q7=makeQuery(id+"F3.opExtrude","SWEPT_BODY",BODY,{"disambiguationData":[OSD([subQ48,subQ47,subQ46,subQ45,subQ44,subQ43,subQ42,subQ41,subQ40,subQ39,subQ38,subQ37,subQ36,subQ35,subQ34,subQ33,subQ32,subQ31,subQ30,subQ29,subQ28,subQ27,subQ26,subQ25,subQ24,subQ23,subQ22,subQ21,subQ20,subQ19,subQ18,subQ17,subQ16,subQ15,subQ14,subQ13,subQ12,subQ11,subQ10,subQ9,subQ8,subQ7,subQ6,subQ5,subQ4,subQ3,subQ2,subQ1,subQ0]),TDD([makeQuery(id+"F2.boolean.opBoolean","SPLIT",FACE,{"disambiguationData":[TD([makeQuery(id+"F2.opExtrude","SWEPT_FACE",FACE,{"disambiguationData":[OSD([sQuery(id+"F0.wireOp",EDGE,"E94")])]})])],"derivedFrom":makeQuery(id+"F1.opExtrude","CAP_FACE",FACE,{"disambiguationData":[OSD([subQ48,subQ47,subQ46,subQ45,subQ44,subQ43,subQ42,subQ41,subQ40,subQ39,subQ38,subQ37,subQ36,subQ35,subQ34,subQ33,subQ32,subQ31,subQ30,subQ29,subQ28,subQ27,subQ26,subQ25,subQ24,subQ23,subQ22,subQ21,subQ20,subQ19,subQ18,subQ17,subQ16,subQ15,subQ14,subQ13,subQ12,subQ11,subQ10,subQ9,subQ8,subQ7,subQ6,subQ5,subQ4,subQ3,subQ2,subQ1,subQ0])],"isStart":false})})])]});}
            var Q8;
            {var subQ0=sQuery(id+"F0.wireOp",EDGE,"E271");var subQ1=sQuery(id+"F0.wireOp",EDGE,"E270");var subQ2=sQuery(id+"F0.wireOp",EDGE,"E269");var subQ3=sQuery(id+"F0.wireOp",EDGE,"E268");var subQ4=sQuery(id+"F0.wireOp",EDGE,"E267");var subQ5=sQuery(id+"F0.wireOp",EDGE,"E266");var subQ6=sQuery(id+"F0.wireOp",EDGE,"E265");var subQ7=sQuery(id+"F0.wireOp",EDGE,"E264");var subQ8=sQuery(id+"F0.wireOp",EDGE,"E263");var subQ9=sQuery(id+"F0.wireOp",EDGE,"E262");var subQ10=sQuery(id+"F0.wireOp",EDGE,"E261");var subQ11=sQuery(id+"F0.wireOp",EDGE,"E260");var subQ12=sQuery(id+"F0.wireOp",EDGE,"E259");var subQ13=sQuery(id+"F0.wireOp",EDGE,"E258");var subQ14=sQuery(id+"F0.wireOp",EDGE,"E257");var subQ15=sQuery(id+"F0.wireOp",EDGE,"E256");var subQ16=sQuery(id+"F0.wireOp",EDGE,"E255");var subQ17=sQuery(id+"F0.wireOp",EDGE,"E254");var subQ18=sQuery(id+"F0.wireOp",EDGE,"E253");var subQ19=sQuery(id+"F0.wireOp",EDGE,"E252");var subQ20=sQuery(id+"F0.wireOp",EDGE,"E251");var subQ21=sQuery(id+"F0.wireOp",EDGE,"E250");var subQ22=sQuery(id+"F0.wireOp",EDGE,"E249");var subQ23=sQuery(id+"F0.wireOp",EDGE,"E248");var subQ24=sQuery(id+"F0.wireOp",EDGE,"E247");var subQ25=sQuery(id+"F0.wireOp",EDGE,"E246");var subQ26=sQuery(id+"F0.wireOp",EDGE,"E245");var subQ27=sQuery(id+"F0.wireOp",EDGE,"E244");var subQ28=sQuery(id+"F0.wireOp",EDGE,"E243");var subQ29=sQuery(id+"F0.wireOp",EDGE,"E242");var subQ30=sQuery(id+"F0.wireOp",EDGE,"E127");var subQ31=sQuery(id+"F0.wireOp",EDGE,"E126");var subQ32=sQuery(id+"F0.wireOp",EDGE,"E125");var subQ33=sQuery(id+"F0.wireOp",EDGE,"E124");var subQ34=sQuery(id+"F0.wireOp",EDGE,"E123");var subQ35=sQuery(id+"F0.wireOp",EDGE,"E122");var subQ36=sQuery(id+"F0.wireOp",EDGE,"E121");var subQ37=sQuery(id+"F0.wireOp",EDGE,"E120");var subQ38=sQuery(id+"F0.wireOp",EDGE,"E56");var subQ39=sQuery(id+"F0.wireOp",EDGE,"E55");var subQ40=sQuery(id+"F0.wireOp",EDGE,"E54");var subQ41=sQuery(id+"F0.wireOp",EDGE,"E53");var subQ42=sQuery(id+"F0.wireOp",EDGE,"E52");var subQ43=sQuery(id+"F0.wireOp",EDGE,"E51");var subQ44=sQuery(id+"F0.wireOp",EDGE,"E50");var subQ45=sQuery(id+"F0.wireOp",EDGE,"E49");var subQ46=sQuery(id+"F0.wireOp",EDGE,"E48");var subQ47=sQuery(id+"F0.wireOp",EDGE,"E47");var subQ48=sQuery(id+"F0.wireOp",EDGE,"E46");Q8=makeQuery(id+"F3.opExtrude","SWEPT_BODY",BODY,{"disambiguationData":[OSD([subQ48,subQ47,subQ46,subQ45,subQ44,subQ43,subQ42,subQ41,subQ40,subQ39,subQ38,subQ37,subQ36,subQ35,subQ34,subQ33,subQ32,subQ31,subQ30,subQ29,subQ28,subQ27,subQ26,subQ25,subQ24,subQ23,subQ22,subQ21,subQ20,subQ19,subQ18,subQ17,subQ16,subQ15,subQ14,subQ13,subQ12,subQ11,subQ10,subQ9,subQ8,subQ7,subQ6,subQ5,subQ4,subQ3,subQ2,subQ1,subQ0]),TDD([makeQuery(id+"F2.boolean.opBoolean","SPLIT",FACE,{"disambiguationData":[TD([makeQuery(id+"F2.opExtrude","SWEPT_FACE",FACE,{"disambiguationData":[OSD([sQuery(id+"F0.wireOp",EDGE,"E202")])]})])],"derivedFrom":makeQuery(id+"F1.opExtrude","CAP_FACE",FACE,{"disambiguationData":[OSD([subQ48,subQ47,subQ46,subQ45,subQ44,subQ43,subQ42,subQ41,subQ40,subQ39,subQ38,subQ37,subQ36,subQ35,subQ34,subQ33,subQ32,subQ31,subQ30,subQ29,subQ28,subQ27,subQ26,subQ25,subQ24,subQ23,subQ22,subQ21,subQ20,subQ19,subQ18,subQ17,subQ16,subQ15,subQ14,subQ13,subQ12,subQ11,subQ10,subQ9,subQ8,subQ7,subQ6,subQ5,subQ4,subQ3,subQ2,subQ1,subQ0])],"isStart":false})})])]});}
            var Q9;
            {var subQ0=sQuery(id+"F0.wireOp",EDGE,"E271");var subQ1=sQuery(id+"F0.wireOp",EDGE,"E270");var subQ2=sQuery(id+"F0.wireOp",EDGE,"E269");var subQ3=sQuery(id+"F0.wireOp",EDGE,"E268");var subQ4=sQuery(id+"F0.wireOp",EDGE,"E267");var subQ5=sQuery(id+"F0.wireOp",EDGE,"E266");var subQ6=sQuery(id+"F0.wireOp",EDGE,"E265");var subQ7=sQuery(id+"F0.wireOp",EDGE,"E264");var subQ8=sQuery(id+"F0.wireOp",EDGE,"E263");var subQ9=sQuery(id+"F0.wireOp",EDGE,"E262");var subQ10=sQuery(id+"F0.wireOp",EDGE,"E261");var subQ11=sQuery(id+"F0.wireOp",EDGE,"E260");var subQ12=sQuery(id+"F0.wireOp",EDGE,"E259");var subQ13=sQuery(id+"F0.wireOp",EDGE,"E258");var subQ14=sQuery(id+"F0.wireOp",EDGE,"E257");var subQ15=sQuery(id+"F0.wireOp",EDGE,"E256");var subQ16=sQuery(id+"F0.wireOp",EDGE,"E255");var subQ17=sQuery(id+"F0.wireOp",EDGE,"E254");var subQ18=sQuery(id+"F0.wireOp",EDGE,"E253");var subQ19=sQuery(id+"F0.wireOp",EDGE,"E252");var subQ20=sQuery(id+"F0.wireOp",EDGE,"E251");var subQ21=sQuery(id+"F0.wireOp",EDGE,"E250");var subQ22=sQuery(id+"F0.wireOp",EDGE,"E249");var subQ23=sQuery(id+"F0.wireOp",EDGE,"E248");var subQ24=sQuery(id+"F0.wireOp",EDGE,"E247");var subQ25=sQuery(id+"F0.wireOp",EDGE,"E246");var subQ26=sQuery(id+"F0.wireOp",EDGE,"E245");var subQ27=sQuery(id+"F0.wireOp",EDGE,"E244");var subQ28=sQuery(id+"F0.wireOp",EDGE,"E243");var subQ29=sQuery(id+"F0.wireOp",EDGE,"E242");var subQ30=sQuery(id+"F0.wireOp",EDGE,"E127");var subQ31=sQuery(id+"F0.wireOp",EDGE,"E126");var subQ32=sQuery(id+"F0.wireOp",EDGE,"E125");var subQ33=sQuery(id+"F0.wireOp",EDGE,"E124");var subQ34=sQuery(id+"F0.wireOp",EDGE,"E123");var subQ35=sQuery(id+"F0.wireOp",EDGE,"E122");var subQ36=sQuery(id+"F0.wireOp",EDGE,"E121");var subQ37=sQuery(id+"F0.wireOp",EDGE,"E120");var subQ38=sQuery(id+"F0.wireOp",EDGE,"E56");var subQ39=sQuery(id+"F0.wireOp",EDGE,"E55");var subQ40=sQuery(id+"F0.wireOp",EDGE,"E54");var subQ41=sQuery(id+"F0.wireOp",EDGE,"E53");var subQ42=sQuery(id+"F0.wireOp",EDGE,"E52");var subQ43=sQuery(id+"F0.wireOp",EDGE,"E51");var subQ44=sQuery(id+"F0.wireOp",EDGE,"E50");var subQ45=sQuery(id+"F0.wireOp",EDGE,"E49");var subQ46=sQuery(id+"F0.wireOp",EDGE,"E48");var subQ47=sQuery(id+"F0.wireOp",EDGE,"E47");var subQ48=sQuery(id+"F0.wireOp",EDGE,"E46");Q9=makeQuery(id+"F3.opExtrude","SWEPT_BODY",BODY,{"disambiguationData":[OSD([subQ48,subQ47,subQ46,subQ45,subQ44,subQ43,subQ42,subQ41,subQ40,subQ39,subQ38,subQ37,subQ36,subQ35,subQ34,subQ33,subQ32,subQ31,subQ30,subQ29,subQ28,subQ27,subQ26,subQ25,subQ24,subQ23,subQ22,subQ21,subQ20,subQ19,subQ18,subQ17,subQ16,subQ15,subQ14,subQ13,subQ12,subQ11,subQ10,subQ9,subQ8,subQ7,subQ6,subQ5,subQ4,subQ3,subQ2,subQ1,subQ0]),TDD([makeQuery(id+"F2.boolean.opBoolean","SPLIT",FACE,{"disambiguationData":[TD([makeQuery(id+"F2.opExtrude","SWEPT_FACE",FACE,{"disambiguationData":[OSD([sQuery(id+"F0.wireOp",EDGE,"E209")])]})])],"derivedFrom":makeQuery(id+"F1.opExtrude","CAP_FACE",FACE,{"disambiguationData":[OSD([subQ48,subQ47,subQ46,subQ45,subQ44,subQ43,subQ42,subQ41,subQ40,subQ39,subQ38,subQ37,subQ36,subQ35,subQ34,subQ33,subQ32,subQ31,subQ30,subQ29,subQ28,subQ27,subQ26,subQ25,subQ24,subQ23,subQ22,subQ21,subQ20,subQ19,subQ18,subQ17,subQ16,subQ15,subQ14,subQ13,subQ12,subQ11,subQ10,subQ9,subQ8,subQ7,subQ6,subQ5,subQ4,subQ3,subQ2,subQ1,subQ0])],"isStart":false})})])]});}
            var Q10;
            {var subQ0=sQuery(id+"F0.wireOp",EDGE,"E271");var subQ1=sQuery(id+"F0.wireOp",EDGE,"E270");var subQ2=sQuery(id+"F0.wireOp",EDGE,"E269");var subQ3=sQuery(id+"F0.wireOp",EDGE,"E268");var subQ4=sQuery(id+"F0.wireOp",EDGE,"E267");var subQ5=sQuery(id+"F0.wireOp",EDGE,"E266");var subQ6=sQuery(id+"F0.wireOp",EDGE,"E265");var subQ7=sQuery(id+"F0.wireOp",EDGE,"E264");var subQ8=sQuery(id+"F0.wireOp",EDGE,"E263");var subQ9=sQuery(id+"F0.wireOp",EDGE,"E262");var subQ10=sQuery(id+"F0.wireOp",EDGE,"E261");var subQ11=sQuery(id+"F0.wireOp",EDGE,"E260");var subQ12=sQuery(id+"F0.wireOp",EDGE,"E259");var subQ13=sQuery(id+"F0.wireOp",EDGE,"E258");var subQ14=sQuery(id+"F0.wireOp",EDGE,"E257");var subQ15=sQuery(id+"F0.wireOp",EDGE,"E256");var subQ16=sQuery(id+"F0.wireOp",EDGE,"E255");var subQ17=sQuery(id+"F0.wireOp",EDGE,"E254");var subQ18=sQuery(id+"F0.wireOp",EDGE,"E253");var subQ19=sQuery(id+"F0.wireOp",EDGE,"E252");var subQ20=sQuery(id+"F0.wireOp",EDGE,"E251");var subQ21=sQuery(id+"F0.wireOp",EDGE,"E250");var subQ22=sQuery(id+"F0.wireOp",EDGE,"E249");var subQ23=sQuery(id+"F0.wireOp",EDGE,"E248");var subQ24=sQuery(id+"F0.wireOp",EDGE,"E247");var subQ25=sQuery(id+"F0.wireOp",EDGE,"E246");var subQ26=sQuery(id+"F0.wireOp",EDGE,"E245");var subQ27=sQuery(id+"F0.wireOp",EDGE,"E244");var subQ28=sQuery(id+"F0.wireOp",EDGE,"E243");var subQ29=sQuery(id+"F0.wireOp",EDGE,"E242");var subQ30=sQuery(id+"F0.wireOp",EDGE,"E127");var subQ31=sQuery(id+"F0.wireOp",EDGE,"E126");var subQ32=sQuery(id+"F0.wireOp",EDGE,"E125");var subQ33=sQuery(id+"F0.wireOp",EDGE,"E124");var subQ34=sQuery(id+"F0.wireOp",EDGE,"E123");var subQ35=sQuery(id+"F0.wireOp",EDGE,"E122");var subQ36=sQuery(id+"F0.wireOp",EDGE,"E121");var subQ37=sQuery(id+"F0.wireOp",EDGE,"E120");var subQ38=sQuery(id+"F0.wireOp",EDGE,"E56");var subQ39=sQuery(id+"F0.wireOp",EDGE,"E55");var subQ40=sQuery(id+"F0.wireOp",EDGE,"E54");var subQ41=sQuery(id+"F0.wireOp",EDGE,"E53");var subQ42=sQuery(id+"F0.wireOp",EDGE,"E52");var subQ43=sQuery(id+"F0.wireOp",EDGE,"E51");var subQ44=sQuery(id+"F0.wireOp",EDGE,"E50");var subQ45=sQuery(id+"F0.wireOp",EDGE,"E49");var subQ46=sQuery(id+"F0.wireOp",EDGE,"E48");var subQ47=sQuery(id+"F0.wireOp",EDGE,"E47");var subQ48=sQuery(id+"F0.wireOp",EDGE,"E46");Q10=makeQuery(id+"F3.opExtrude","SWEPT_BODY",BODY,{"disambiguationData":[OSD([subQ48,subQ47,subQ46,subQ45,subQ44,subQ43,subQ42,subQ41,subQ40,subQ39,subQ38,subQ37,subQ36,subQ35,subQ34,subQ33,subQ32,subQ31,subQ30,subQ29,subQ28,subQ27,subQ26,subQ25,subQ24,subQ23,subQ22,subQ21,subQ20,subQ19,subQ18,subQ17,subQ16,subQ15,subQ14,subQ13,subQ12,subQ11,subQ10,subQ9,subQ8,subQ7,subQ6,subQ5,subQ4,subQ3,subQ2,subQ1,subQ0]),TDD([makeQuery(id+"F2.boolean.opBoolean","SPLIT",FACE,{"disambiguationData":[TD([makeQuery(id+"F2.opExtrude","SWEPT_FACE",FACE,{"disambiguationData":[OSD([sQuery(id+"F0.wireOp",EDGE,"E192")])]})])],"derivedFrom":makeQuery(id+"F1.opExtrude","CAP_FACE",FACE,{"disambiguationData":[OSD([subQ48,subQ47,subQ46,subQ45,subQ44,subQ43,subQ42,subQ41,subQ40,subQ39,subQ38,subQ37,subQ36,subQ35,subQ34,subQ33,subQ32,subQ31,subQ30,subQ29,subQ28,subQ27,subQ26,subQ25,subQ24,subQ23,subQ22,subQ21,subQ20,subQ19,subQ18,subQ17,subQ16,subQ15,subQ14,subQ13,subQ12,subQ11,subQ10,subQ9,subQ8,subQ7,subQ6,subQ5,subQ4,subQ3,subQ2,subQ1,subQ0])],"isStart":false})})])]});}
            var Q11;
            {var subQ0=sQuery(id+"F0.wireOp",EDGE,"E271");var subQ1=sQuery(id+"F0.wireOp",EDGE,"E270");var subQ2=sQuery(id+"F0.wireOp",EDGE,"E269");var subQ3=sQuery(id+"F0.wireOp",EDGE,"E268");var subQ4=sQuery(id+"F0.wireOp",EDGE,"E267");var subQ5=sQuery(id+"F0.wireOp",EDGE,"E266");var subQ6=sQuery(id+"F0.wireOp",EDGE,"E265");var subQ7=sQuery(id+"F0.wireOp",EDGE,"E264");var subQ8=sQuery(id+"F0.wireOp",EDGE,"E263");var subQ9=sQuery(id+"F0.wireOp",EDGE,"E262");var subQ10=sQuery(id+"F0.wireOp",EDGE,"E261");var subQ11=sQuery(id+"F0.wireOp",EDGE,"E260");var subQ12=sQuery(id+"F0.wireOp",EDGE,"E259");var subQ13=sQuery(id+"F0.wireOp",EDGE,"E258");var subQ14=sQuery(id+"F0.wireOp",EDGE,"E257");var subQ15=sQuery(id+"F0.wireOp",EDGE,"E256");var subQ16=sQuery(id+"F0.wireOp",EDGE,"E255");var subQ17=sQuery(id+"F0.wireOp",EDGE,"E254");var subQ18=sQuery(id+"F0.wireOp",EDGE,"E253");var subQ19=sQuery(id+"F0.wireOp",EDGE,"E252");var subQ20=sQuery(id+"F0.wireOp",EDGE,"E251");var subQ21=sQuery(id+"F0.wireOp",EDGE,"E250");var subQ22=sQuery(id+"F0.wireOp",EDGE,"E249");var subQ23=sQuery(id+"F0.wireOp",EDGE,"E248");var subQ24=sQuery(id+"F0.wireOp",EDGE,"E247");var subQ25=sQuery(id+"F0.wireOp",EDGE,"E246");var subQ26=sQuery(id+"F0.wireOp",EDGE,"E245");var subQ27=sQuery(id+"F0.wireOp",EDGE,"E244");var subQ28=sQuery(id+"F0.wireOp",EDGE,"E243");var subQ29=sQuery(id+"F0.wireOp",EDGE,"E242");var subQ30=sQuery(id+"F0.wireOp",EDGE,"E127");var subQ31=sQuery(id+"F0.wireOp",EDGE,"E126");var subQ32=sQuery(id+"F0.wireOp",EDGE,"E125");var subQ33=sQuery(id+"F0.wireOp",EDGE,"E124");var subQ34=sQuery(id+"F0.wireOp",EDGE,"E123");var subQ35=sQuery(id+"F0.wireOp",EDGE,"E122");var subQ36=sQuery(id+"F0.wireOp",EDGE,"E121");var subQ37=sQuery(id+"F0.wireOp",EDGE,"E120");var subQ38=sQuery(id+"F0.wireOp",EDGE,"E56");var subQ39=sQuery(id+"F0.wireOp",EDGE,"E55");var subQ40=sQuery(id+"F0.wireOp",EDGE,"E54");var subQ41=sQuery(id+"F0.wireOp",EDGE,"E53");var subQ42=sQuery(id+"F0.wireOp",EDGE,"E52");var subQ43=sQuery(id+"F0.wireOp",EDGE,"E51");var subQ44=sQuery(id+"F0.wireOp",EDGE,"E50");var subQ45=sQuery(id+"F0.wireOp",EDGE,"E49");var subQ46=sQuery(id+"F0.wireOp",EDGE,"E48");var subQ47=sQuery(id+"F0.wireOp",EDGE,"E47");var subQ48=sQuery(id+"F0.wireOp",EDGE,"E46");Q11=makeQuery(id+"F3.opExtrude","SWEPT_BODY",BODY,{"disambiguationData":[OSD([subQ48,subQ47,subQ46,subQ45,subQ44,subQ43,subQ42,subQ41,subQ40,subQ39,subQ38,subQ37,subQ36,subQ35,subQ34,subQ33,subQ32,subQ31,subQ30,subQ29,subQ28,subQ27,subQ26,subQ25,subQ24,subQ23,subQ22,subQ21,subQ20,subQ19,subQ18,subQ17,subQ16,subQ15,subQ14,subQ13,subQ12,subQ11,subQ10,subQ9,subQ8,subQ7,subQ6,subQ5,subQ4,subQ3,subQ2,subQ1,subQ0]),TDD([makeQuery(id+"F2.boolean.opBoolean","SPLIT",FACE,{"disambiguationData":[TD([makeQuery(id+"F2.opExtrude","SWEPT_FACE",FACE,{"disambiguationData":[OSD([sQuery(id+"F0.wireOp",EDGE,"E193")])]})])],"derivedFrom":makeQuery(id+"F1.opExtrude","CAP_FACE",FACE,{"disambiguationData":[OSD([subQ48,subQ47,subQ46,subQ45,subQ44,subQ43,subQ42,subQ41,subQ40,subQ39,subQ38,subQ37,subQ36,subQ35,subQ34,subQ33,subQ32,subQ31,subQ30,subQ29,subQ28,subQ27,subQ26,subQ25,subQ24,subQ23,subQ22,subQ21,subQ20,subQ19,subQ18,subQ17,subQ16,subQ15,subQ14,subQ13,subQ12,subQ11,subQ10,subQ9,subQ8,subQ7,subQ6,subQ5,subQ4,subQ3,subQ2,subQ1,subQ0])],"isStart":false})})])]});}
            var Q12;
            {var subQ0=sQuery(id+"F0.wireOp",EDGE,"E127");var subQ1=sQuery(id+"F0.wireOp",EDGE,"E126");var subQ2=sQuery(id+"F0.wireOp",EDGE,"E125");var subQ3=sQuery(id+"F0.wireOp",EDGE,"E124");var subQ4=sQuery(id+"F0.wireOp",EDGE,"E123");var subQ5=sQuery(id+"F0.wireOp",EDGE,"E120");var subQ6=sQuery(id+"F0.wireOp",EDGE,"E56");var subQ7=sQuery(id+"F0.wireOp",EDGE,"E55");var subQ8=sQuery(id+"F0.wireOp",EDGE,"E54");var subQ9=sQuery(id+"F0.wireOp",EDGE,"E53");var subQ10=sQuery(id+"F0.wireOp",EDGE,"E52");var subQ11=sQuery(id+"F0.wireOp",EDGE,"E51");var subQ12=sQuery(id+"F0.wireOp",EDGE,"E50");var subQ13=sQuery(id+"F0.wireOp",EDGE,"E49");var subQ14=sQuery(id+"F0.wireOp",EDGE,"E48");var subQ15=sQuery(id+"F0.wireOp",EDGE,"E47");var subQ16=sQuery(id+"F0.wireOp",EDGE,"E122");var subQ17=sQuery(id+"F0.wireOp",EDGE,"E121");var subQ18=sQuery(id+"F0.wireOp",EDGE,"E46");var subQ19=sQuery(id+"F0.wireOp",EDGE,"E271");var subQ20=sQuery(id+"F0.wireOp",EDGE,"E270");var subQ21=sQuery(id+"F0.wireOp",EDGE,"E269");var subQ22=sQuery(id+"F0.wireOp",EDGE,"E268");var subQ23=sQuery(id+"F0.wireOp",EDGE,"E267");var subQ24=sQuery(id+"F0.wireOp",EDGE,"E266");var subQ25=sQuery(id+"F0.wireOp",EDGE,"E265");var subQ26=sQuery(id+"F0.wireOp",EDGE,"E264");var subQ27=sQuery(id+"F0.wireOp",EDGE,"E263");var subQ28=sQuery(id+"F0.wireOp",EDGE,"E262");var subQ29=sQuery(id+"F0.wireOp",EDGE,"E261");var subQ30=sQuery(id+"F0.wireOp",EDGE,"E260");var subQ31=sQuery(id+"F0.wireOp",EDGE,"E259");var subQ32=sQuery(id+"F0.wireOp",EDGE,"E258");var subQ33=sQuery(id+"F0.wireOp",EDGE,"E257");var subQ34=sQuery(id+"F0.wireOp",EDGE,"E256");var subQ35=sQuery(id+"F0.wireOp",EDGE,"E255");var subQ36=sQuery(id+"F0.wireOp",EDGE,"E254");var subQ37=sQuery(id+"F0.wireOp",EDGE,"E253");var subQ38=sQuery(id+"F0.wireOp",EDGE,"E252");var subQ39=sQuery(id+"F0.wireOp",EDGE,"E251");var subQ40=sQuery(id+"F0.wireOp",EDGE,"E250");var subQ41=sQuery(id+"F0.wireOp",EDGE,"E249");var subQ42=sQuery(id+"F0.wireOp",EDGE,"E248");var subQ43=sQuery(id+"F0.wireOp",EDGE,"E247");var subQ44=sQuery(id+"F0.wireOp",EDGE,"E246");var subQ45=sQuery(id+"F0.wireOp",EDGE,"E245");var subQ46=sQuery(id+"F0.wireOp",EDGE,"E244");var subQ47=sQuery(id+"F0.wireOp",EDGE,"E243");var subQ48=sQuery(id+"F0.wireOp",EDGE,"E242");Q12=makeQuery(id+"F3.opExtrude","SWEPT_BODY",BODY,{"disambiguationData":[OSD([subQ18,subQ15,subQ14,subQ13,subQ12,subQ11,subQ10,subQ9,subQ8,subQ7,subQ6,subQ5,subQ17,subQ16,subQ4,subQ3,subQ2,subQ1,subQ0,subQ48,subQ47,subQ46,subQ45,subQ44,subQ43,subQ42,subQ41,subQ40,subQ39,subQ38,subQ37,subQ36,subQ35,subQ34,subQ33,subQ32,subQ31,subQ30,subQ29,subQ28,subQ27,subQ26,subQ25,subQ24,subQ23,subQ22,subQ21,subQ20,subQ19]),TDD([makeQuery(id+"F2.boolean.opBoolean","SPLIT",FACE,{"disambiguationData":[TD([makeQuery(id+"F1.opExtrude","SWEPT_FACE",FACE,{"disambiguationData":[OSD([subQ18])]})])],"derivedFrom":makeQuery(id+"F1.opExtrude","CAP_FACE",FACE,{"disambiguationData":[OSD([subQ18,subQ15,subQ14,subQ13,subQ12,subQ11,subQ10,subQ9,subQ8,subQ7,subQ6,subQ5,subQ17,subQ16,subQ4,subQ3,subQ2,subQ1,subQ0,subQ48,subQ47,subQ46,subQ45,subQ44,subQ43,subQ42,subQ41,subQ40,subQ39,subQ38,subQ37,subQ36,subQ35,subQ34,subQ33,subQ32,subQ31,subQ30,subQ29,subQ28,subQ27,subQ26,subQ25,subQ24,subQ23,subQ22,subQ21,subQ20,subQ19])],"isStart":false})})])]});}
            var Q13;
            {var subQ0=sQuery(id+"F0.wireOp",EDGE,"E271");var subQ1=sQuery(id+"F0.wireOp",EDGE,"E270");var subQ2=sQuery(id+"F0.wireOp",EDGE,"E269");var subQ3=sQuery(id+"F0.wireOp",EDGE,"E268");var subQ4=sQuery(id+"F0.wireOp",EDGE,"E267");var subQ5=sQuery(id+"F0.wireOp",EDGE,"E266");var subQ6=sQuery(id+"F0.wireOp",EDGE,"E265");var subQ7=sQuery(id+"F0.wireOp",EDGE,"E264");var subQ8=sQuery(id+"F0.wireOp",EDGE,"E263");var subQ9=sQuery(id+"F0.wireOp",EDGE,"E262");var subQ10=sQuery(id+"F0.wireOp",EDGE,"E261");var subQ11=sQuery(id+"F0.wireOp",EDGE,"E260");var subQ12=sQuery(id+"F0.wireOp",EDGE,"E259");var subQ13=sQuery(id+"F0.wireOp",EDGE,"E258");var subQ14=sQuery(id+"F0.wireOp",EDGE,"E257");var subQ15=sQuery(id+"F0.wireOp",EDGE,"E256");var subQ16=sQuery(id+"F0.wireOp",EDGE,"E255");var subQ17=sQuery(id+"F0.wireOp",EDGE,"E254");var subQ18=sQuery(id+"F0.wireOp",EDGE,"E253");var subQ19=sQuery(id+"F0.wireOp",EDGE,"E252");var subQ20=sQuery(id+"F0.wireOp",EDGE,"E251");var subQ21=sQuery(id+"F0.wireOp",EDGE,"E250");var subQ22=sQuery(id+"F0.wireOp",EDGE,"E249");var subQ23=sQuery(id+"F0.wireOp",EDGE,"E248");var subQ24=sQuery(id+"F0.wireOp",EDGE,"E247");var subQ25=sQuery(id+"F0.wireOp",EDGE,"E246");var subQ26=sQuery(id+"F0.wireOp",EDGE,"E245");var subQ27=sQuery(id+"F0.wireOp",EDGE,"E244");var subQ28=sQuery(id+"F0.wireOp",EDGE,"E243");var subQ29=sQuery(id+"F0.wireOp",EDGE,"E242");var subQ30=sQuery(id+"F0.wireOp",EDGE,"E127");var subQ31=sQuery(id+"F0.wireOp",EDGE,"E126");var subQ32=sQuery(id+"F0.wireOp",EDGE,"E125");var subQ33=sQuery(id+"F0.wireOp",EDGE,"E124");var subQ34=sQuery(id+"F0.wireOp",EDGE,"E123");var subQ35=sQuery(id+"F0.wireOp",EDGE,"E122");var subQ36=sQuery(id+"F0.wireOp",EDGE,"E121");var subQ37=sQuery(id+"F0.wireOp",EDGE,"E120");var subQ38=sQuery(id+"F0.wireOp",EDGE,"E56");var subQ39=sQuery(id+"F0.wireOp",EDGE,"E55");var subQ40=sQuery(id+"F0.wireOp",EDGE,"E54");var subQ41=sQuery(id+"F0.wireOp",EDGE,"E53");var subQ42=sQuery(id+"F0.wireOp",EDGE,"E52");var subQ43=sQuery(id+"F0.wireOp",EDGE,"E51");var subQ44=sQuery(id+"F0.wireOp",EDGE,"E50");var subQ45=sQuery(id+"F0.wireOp",EDGE,"E49");var subQ46=sQuery(id+"F0.wireOp",EDGE,"E48");var subQ47=sQuery(id+"F0.wireOp",EDGE,"E47");var subQ48=sQuery(id+"F0.wireOp",EDGE,"E46");Q13=makeQuery(id+"F3.opExtrude","SWEPT_BODY",BODY,{"disambiguationData":[OSD([subQ48,subQ47,subQ46,subQ45,subQ44,subQ43,subQ42,subQ41,subQ40,subQ39,subQ38,subQ37,subQ36,subQ35,subQ34,subQ33,subQ32,subQ31,subQ30,subQ29,subQ28,subQ27,subQ26,subQ25,subQ24,subQ23,subQ22,subQ21,subQ20,subQ19,subQ18,subQ17,subQ16,subQ15,subQ14,subQ13,subQ12,subQ11,subQ10,subQ9,subQ8,subQ7,subQ6,subQ5,subQ4,subQ3,subQ2,subQ1,subQ0]),TDD([makeQuery(id+"F2.boolean.opBoolean","SPLIT",FACE,{"disambiguationData":[TD([makeQuery(id+"F2.opExtrude","SWEPT_FACE",FACE,{"disambiguationData":[OSD([sQuery(id+"F0.wireOp",EDGE,"E205")])]})])],"derivedFrom":makeQuery(id+"F1.opExtrude","CAP_FACE",FACE,{"disambiguationData":[OSD([subQ48,subQ47,subQ46,subQ45,subQ44,subQ43,subQ42,subQ41,subQ40,subQ39,subQ38,subQ37,subQ36,subQ35,subQ34,subQ33,subQ32,subQ31,subQ30,subQ29,subQ28,subQ27,subQ26,subQ25,subQ24,subQ23,subQ22,subQ21,subQ20,subQ19,subQ18,subQ17,subQ16,subQ15,subQ14,subQ13,subQ12,subQ11,subQ10,subQ9,subQ8,subQ7,subQ6,subQ5,subQ4,subQ3,subQ2,subQ1,subQ0])],"isStart":false})})])]});}
            var Q14;
            Q14=sQuery(id+"F5.wireOp",EDGE,"E273");
            transform(context, id + "F6", {"entities" : qUnion([Q0, Q1, Q2, Q3, Q4, Q5, Q6, Q7, Q8, Q9, Q10, Q11, Q12, Q13]), "transformType" : TransformType.ROTATION, "transformAxis" : qUnion([Q14]), "angle" : 90 * degree, "makeCopy" : false});
        }
        {
            var Q0;
            Q0=makeQuery(id+"F2.boolean.opBoolean","SPLIT",FACE,{"disambiguationData":[TD([makeQuery(id+"F2.opExtrude","SWEPT_FACE",FACE,{"disambiguationData":[OSD([sQuery(id+"F0.wireOp",EDGE,"E85")])]})])],"derivedFrom":makeQuery(id+"F1.opExtrude","CAP_FACE",FACE,{"disambiguationData":[OSD([sQuery(id+"F0.wireOp",EDGE,"E46"),sQuery(id+"F0.wireOp",EDGE,"E47"),sQuery(id+"F0.wireOp",EDGE,"E48"),sQuery(id+"F0.wireOp",EDGE,"E49"),sQuery(id+"F0.wireOp",EDGE,"E50"),sQuery(id+"F0.wireOp",EDGE,"E51"),sQuery(id+"F0.wireOp",EDGE,"E52"),sQuery(id+"F0.wireOp",EDGE,"E53"),sQuery(id+"F0.wireOp",EDGE,"E54"),sQuery(id+"F0.wireOp",EDGE,"E55"),sQuery(id+"F0.wireOp",EDGE,"E56"),sQuery(id+"F0.wireOp",EDGE,"E120"),sQuery(id+"F0.wireOp",EDGE,"E121"),sQuery(id+"F0.wireOp",EDGE,"E122"),sQuery(id+"F0.wireOp",EDGE,"E123"),sQuery(id+"F0.wireOp",EDGE,"E124"),sQuery(id+"F0.wireOp",EDGE,"E125"),sQuery(id+"F0.wireOp",EDGE,"E126"),sQuery(id+"F0.wireOp",EDGE,"E127"),sQuery(id+"F0.wireOp",EDGE,"E242"),sQuery(id+"F0.wireOp",EDGE,"E243"),sQuery(id+"F0.wireOp",EDGE,"E244"),sQuery(id+"F0.wireOp",EDGE,"E245"),sQuery(id+"F0.wireOp",EDGE,"E246"),sQuery(id+"F0.wireOp",EDGE,"E247"),sQuery(id+"F0.wireOp",EDGE,"E248"),sQuery(id+"F0.wireOp",EDGE,"E249"),sQuery(id+"F0.wireOp",EDGE,"E250"),sQuery(id+"F0.wireOp",EDGE,"E251"),sQuery(id+"F0.wireOp",EDGE,"E252"),sQuery(id+"F0.wireOp",EDGE,"E253"),sQuery(id+"F0.wireOp",EDGE,"E254"),sQuery(id+"F0.wireOp",EDGE,"E255"),sQuery(id+"F0.wireOp",EDGE,"E256"),sQuery(id+"F0.wireOp",EDGE,"E257"),sQuery(id+"F0.wireOp",EDGE,"E258"),sQuery(id+"F0.wireOp",EDGE,"E259"),sQuery(id+"F0.wireOp",EDGE,"E260"),sQuery(id+"F0.wireOp",EDGE,"E261"),sQuery(id+"F0.wireOp",EDGE,"E262"),sQuery(id+"F0.wireOp",EDGE,"E263"),sQuery(id+"F0.wireOp",EDGE,"E264"),sQuery(id+"F0.wireOp",EDGE,"E265"),sQuery(id+"F0.wireOp",EDGE,"E266"),sQuery(id+"F0.wireOp",EDGE,"E267"),sQuery(id+"F0.wireOp",EDGE,"E268"),sQuery(id+"F0.wireOp",EDGE,"E269"),sQuery(id+"F0.wireOp",EDGE,"E270"),sQuery(id+"F0.wireOp",EDGE,"E271")])],"isStart":false})});
            var Q1;
            Q1=makeQuery(id+"F2.boolean.opBoolean","SPLIT",FACE,{"disambiguationData":[TD([makeQuery(id+"F2.opExtrude","SWEPT_FACE",FACE,{"disambiguationData":[OSD([sQuery(id+"F0.wireOp",EDGE,"E82")])]})])],"derivedFrom":makeQuery(id+"F1.opExtrude","CAP_FACE",FACE,{"disambiguationData":[OSD([sQuery(id+"F0.wireOp",EDGE,"E46"),sQuery(id+"F0.wireOp",EDGE,"E47"),sQuery(id+"F0.wireOp",EDGE,"E48"),sQuery(id+"F0.wireOp",EDGE,"E49"),sQuery(id+"F0.wireOp",EDGE,"E50"),sQuery(id+"F0.wireOp",EDGE,"E51"),sQuery(id+"F0.wireOp",EDGE,"E52"),sQuery(id+"F0.wireOp",EDGE,"E53"),sQuery(id+"F0.wireOp",EDGE,"E54"),sQuery(id+"F0.wireOp",EDGE,"E55"),sQuery(id+"F0.wireOp",EDGE,"E56"),sQuery(id+"F0.wireOp",EDGE,"E120"),sQuery(id+"F0.wireOp",EDGE,"E121"),sQuery(id+"F0.wireOp",EDGE,"E122"),sQuery(id+"F0.wireOp",EDGE,"E123"),sQuery(id+"F0.wireOp",EDGE,"E124"),sQuery(id+"F0.wireOp",EDGE,"E125"),sQuery(id+"F0.wireOp",EDGE,"E126"),sQuery(id+"F0.wireOp",EDGE,"E127"),sQuery(id+"F0.wireOp",EDGE,"E242"),sQuery(id+"F0.wireOp",EDGE,"E243"),sQuery(id+"F0.wireOp",EDGE,"E244"),sQuery(id+"F0.wireOp",EDGE,"E245"),sQuery(id+"F0.wireOp",EDGE,"E246"),sQuery(id+"F0.wireOp",EDGE,"E247"),sQuery(id+"F0.wireOp",EDGE,"E248"),sQuery(id+"F0.wireOp",EDGE,"E249"),sQuery(id+"F0.wireOp",EDGE,"E250"),sQuery(id+"F0.wireOp",EDGE,"E251"),sQuery(id+"F0.wireOp",EDGE,"E252"),sQuery(id+"F0.wireOp",EDGE,"E253"),sQuery(id+"F0.wireOp",EDGE,"E254"),sQuery(id+"F0.wireOp",EDGE,"E255"),sQuery(id+"F0.wireOp",EDGE,"E256"),sQuery(id+"F0.wireOp",EDGE,"E257"),sQuery(id+"F0.wireOp",EDGE,"E258"),sQuery(id+"F0.wireOp",EDGE,"E259"),sQuery(id+"F0.wireOp",EDGE,"E260"),sQuery(id+"F0.wireOp",EDGE,"E261"),sQuery(id+"F0.wireOp",EDGE,"E262"),sQuery(id+"F0.wireOp",EDGE,"E263"),sQuery(id+"F0.wireOp",EDGE,"E264"),sQuery(id+"F0.wireOp",EDGE,"E265"),sQuery(id+"F0.wireOp",EDGE,"E266"),sQuery(id+"F0.wireOp",EDGE,"E267"),sQuery(id+"F0.wireOp",EDGE,"E268"),sQuery(id+"F0.wireOp",EDGE,"E269"),sQuery(id+"F0.wireOp",EDGE,"E270"),sQuery(id+"F0.wireOp",EDGE,"E271")])],"isStart":false})});
            var Q2;
            Q2=makeQuery(id+"F2.boolean.opBoolean","SPLIT",FACE,{"disambiguationData":[TD([makeQuery(id+"F2.opExtrude","SWEPT_FACE",FACE,{"disambiguationData":[OSD([sQuery(id+"F0.wireOp",EDGE,"E94")])]})])],"derivedFrom":makeQuery(id+"F1.opExtrude","CAP_FACE",FACE,{"disambiguationData":[OSD([sQuery(id+"F0.wireOp",EDGE,"E46"),sQuery(id+"F0.wireOp",EDGE,"E47"),sQuery(id+"F0.wireOp",EDGE,"E48"),sQuery(id+"F0.wireOp",EDGE,"E49"),sQuery(id+"F0.wireOp",EDGE,"E50"),sQuery(id+"F0.wireOp",EDGE,"E51"),sQuery(id+"F0.wireOp",EDGE,"E52"),sQuery(id+"F0.wireOp",EDGE,"E53"),sQuery(id+"F0.wireOp",EDGE,"E54"),sQuery(id+"F0.wireOp",EDGE,"E55"),sQuery(id+"F0.wireOp",EDGE,"E56"),sQuery(id+"F0.wireOp",EDGE,"E120"),sQuery(id+"F0.wireOp",EDGE,"E121"),sQuery(id+"F0.wireOp",EDGE,"E122"),sQuery(id+"F0.wireOp",EDGE,"E123"),sQuery(id+"F0.wireOp",EDGE,"E124"),sQuery(id+"F0.wireOp",EDGE,"E125"),sQuery(id+"F0.wireOp",EDGE,"E126"),sQuery(id+"F0.wireOp",EDGE,"E127"),sQuery(id+"F0.wireOp",EDGE,"E242"),sQuery(id+"F0.wireOp",EDGE,"E243"),sQuery(id+"F0.wireOp",EDGE,"E244"),sQuery(id+"F0.wireOp",EDGE,"E245"),sQuery(id+"F0.wireOp",EDGE,"E246"),sQuery(id+"F0.wireOp",EDGE,"E247"),sQuery(id+"F0.wireOp",EDGE,"E248"),sQuery(id+"F0.wireOp",EDGE,"E249"),sQuery(id+"F0.wireOp",EDGE,"E250"),sQuery(id+"F0.wireOp",EDGE,"E251"),sQuery(id+"F0.wireOp",EDGE,"E252"),sQuery(id+"F0.wireOp",EDGE,"E253"),sQuery(id+"F0.wireOp",EDGE,"E254"),sQuery(id+"F0.wireOp",EDGE,"E255"),sQuery(id+"F0.wireOp",EDGE,"E256"),sQuery(id+"F0.wireOp",EDGE,"E257"),sQuery(id+"F0.wireOp",EDGE,"E258"),sQuery(id+"F0.wireOp",EDGE,"E259"),sQuery(id+"F0.wireOp",EDGE,"E260"),sQuery(id+"F0.wireOp",EDGE,"E261"),sQuery(id+"F0.wireOp",EDGE,"E262"),sQuery(id+"F0.wireOp",EDGE,"E263"),sQuery(id+"F0.wireOp",EDGE,"E264"),sQuery(id+"F0.wireOp",EDGE,"E265"),sQuery(id+"F0.wireOp",EDGE,"E266"),sQuery(id+"F0.wireOp",EDGE,"E267"),sQuery(id+"F0.wireOp",EDGE,"E268"),sQuery(id+"F0.wireOp",EDGE,"E269"),sQuery(id+"F0.wireOp",EDGE,"E270"),sQuery(id+"F0.wireOp",EDGE,"E271")])],"isStart":false})});
            var Q3;
            Q3=makeQuery(id+"F2.boolean.opBoolean","SPLIT",FACE,{"disambiguationData":[TD([makeQuery(id+"F2.opExtrude","SWEPT_FACE",FACE,{"disambiguationData":[OSD([sQuery(id+"F0.wireOp",EDGE,"E88")])]})])],"derivedFrom":makeQuery(id+"F1.opExtrude","CAP_FACE",FACE,{"disambiguationData":[OSD([sQuery(id+"F0.wireOp",EDGE,"E46"),sQuery(id+"F0.wireOp",EDGE,"E47"),sQuery(id+"F0.wireOp",EDGE,"E48"),sQuery(id+"F0.wireOp",EDGE,"E49"),sQuery(id+"F0.wireOp",EDGE,"E50"),sQuery(id+"F0.wireOp",EDGE,"E51"),sQuery(id+"F0.wireOp",EDGE,"E52"),sQuery(id+"F0.wireOp",EDGE,"E53"),sQuery(id+"F0.wireOp",EDGE,"E54"),sQuery(id+"F0.wireOp",EDGE,"E55"),sQuery(id+"F0.wireOp",EDGE,"E56"),sQuery(id+"F0.wireOp",EDGE,"E120"),sQuery(id+"F0.wireOp",EDGE,"E121"),sQuery(id+"F0.wireOp",EDGE,"E122"),sQuery(id+"F0.wireOp",EDGE,"E123"),sQuery(id+"F0.wireOp",EDGE,"E124"),sQuery(id+"F0.wireOp",EDGE,"E125"),sQuery(id+"F0.wireOp",EDGE,"E126"),sQuery(id+"F0.wireOp",EDGE,"E127"),sQuery(id+"F0.wireOp",EDGE,"E242"),sQuery(id+"F0.wireOp",EDGE,"E243"),sQuery(id+"F0.wireOp",EDGE,"E244"),sQuery(id+"F0.wireOp",EDGE,"E245"),sQuery(id+"F0.wireOp",EDGE,"E246"),sQuery(id+"F0.wireOp",EDGE,"E247"),sQuery(id+"F0.wireOp",EDGE,"E248"),sQuery(id+"F0.wireOp",EDGE,"E249"),sQuery(id+"F0.wireOp",EDGE,"E250"),sQuery(id+"F0.wireOp",EDGE,"E251"),sQuery(id+"F0.wireOp",EDGE,"E252"),sQuery(id+"F0.wireOp",EDGE,"E253"),sQuery(id+"F0.wireOp",EDGE,"E254"),sQuery(id+"F0.wireOp",EDGE,"E255"),sQuery(id+"F0.wireOp",EDGE,"E256"),sQuery(id+"F0.wireOp",EDGE,"E257"),sQuery(id+"F0.wireOp",EDGE,"E258"),sQuery(id+"F0.wireOp",EDGE,"E259"),sQuery(id+"F0.wireOp",EDGE,"E260"),sQuery(id+"F0.wireOp",EDGE,"E261"),sQuery(id+"F0.wireOp",EDGE,"E262"),sQuery(id+"F0.wireOp",EDGE,"E263"),sQuery(id+"F0.wireOp",EDGE,"E264"),sQuery(id+"F0.wireOp",EDGE,"E265"),sQuery(id+"F0.wireOp",EDGE,"E266"),sQuery(id+"F0.wireOp",EDGE,"E267"),sQuery(id+"F0.wireOp",EDGE,"E268"),sQuery(id+"F0.wireOp",EDGE,"E269"),sQuery(id+"F0.wireOp",EDGE,"E270"),sQuery(id+"F0.wireOp",EDGE,"E271")])],"isStart":false})});
            var Q4;
            Q4=makeQuery(id+"F2.boolean.opBoolean","SPLIT",FACE,{"disambiguationData":[TD([makeQuery(id+"F2.opExtrude","SWEPT_FACE",FACE,{"disambiguationData":[OSD([sQuery(id+"F0.wireOp",EDGE,"E91")])]})])],"derivedFrom":makeQuery(id+"F1.opExtrude","CAP_FACE",FACE,{"disambiguationData":[OSD([sQuery(id+"F0.wireOp",EDGE,"E46"),sQuery(id+"F0.wireOp",EDGE,"E47"),sQuery(id+"F0.wireOp",EDGE,"E48"),sQuery(id+"F0.wireOp",EDGE,"E49"),sQuery(id+"F0.wireOp",EDGE,"E50"),sQuery(id+"F0.wireOp",EDGE,"E51"),sQuery(id+"F0.wireOp",EDGE,"E52"),sQuery(id+"F0.wireOp",EDGE,"E53"),sQuery(id+"F0.wireOp",EDGE,"E54"),sQuery(id+"F0.wireOp",EDGE,"E55"),sQuery(id+"F0.wireOp",EDGE,"E56"),sQuery(id+"F0.wireOp",EDGE,"E120"),sQuery(id+"F0.wireOp",EDGE,"E121"),sQuery(id+"F0.wireOp",EDGE,"E122"),sQuery(id+"F0.wireOp",EDGE,"E123"),sQuery(id+"F0.wireOp",EDGE,"E124"),sQuery(id+"F0.wireOp",EDGE,"E125"),sQuery(id+"F0.wireOp",EDGE,"E126"),sQuery(id+"F0.wireOp",EDGE,"E127"),sQuery(id+"F0.wireOp",EDGE,"E242"),sQuery(id+"F0.wireOp",EDGE,"E243"),sQuery(id+"F0.wireOp",EDGE,"E244"),sQuery(id+"F0.wireOp",EDGE,"E245"),sQuery(id+"F0.wireOp",EDGE,"E246"),sQuery(id+"F0.wireOp",EDGE,"E247"),sQuery(id+"F0.wireOp",EDGE,"E248"),sQuery(id+"F0.wireOp",EDGE,"E249"),sQuery(id+"F0.wireOp",EDGE,"E250"),sQuery(id+"F0.wireOp",EDGE,"E251"),sQuery(id+"F0.wireOp",EDGE,"E252"),sQuery(id+"F0.wireOp",EDGE,"E253"),sQuery(id+"F0.wireOp",EDGE,"E254"),sQuery(id+"F0.wireOp",EDGE,"E255"),sQuery(id+"F0.wireOp",EDGE,"E256"),sQuery(id+"F0.wireOp",EDGE,"E257"),sQuery(id+"F0.wireOp",EDGE,"E258"),sQuery(id+"F0.wireOp",EDGE,"E259"),sQuery(id+"F0.wireOp",EDGE,"E260"),sQuery(id+"F0.wireOp",EDGE,"E261"),sQuery(id+"F0.wireOp",EDGE,"E262"),sQuery(id+"F0.wireOp",EDGE,"E263"),sQuery(id+"F0.wireOp",EDGE,"E264"),sQuery(id+"F0.wireOp",EDGE,"E265"),sQuery(id+"F0.wireOp",EDGE,"E266"),sQuery(id+"F0.wireOp",EDGE,"E267"),sQuery(id+"F0.wireOp",EDGE,"E268"),sQuery(id+"F0.wireOp",EDGE,"E269"),sQuery(id+"F0.wireOp",EDGE,"E270"),sQuery(id+"F0.wireOp",EDGE,"E271")])],"isStart":false})});
            extrude(context, id + "F7", {"entities" : qUnion([Q0, Q1, Q2, Q3, Q4]), "operationType" : NewBodyOperationType.REMOVE, "oppositeDirection" : true, "depth" : 25.4 * mm});
        }
    });
